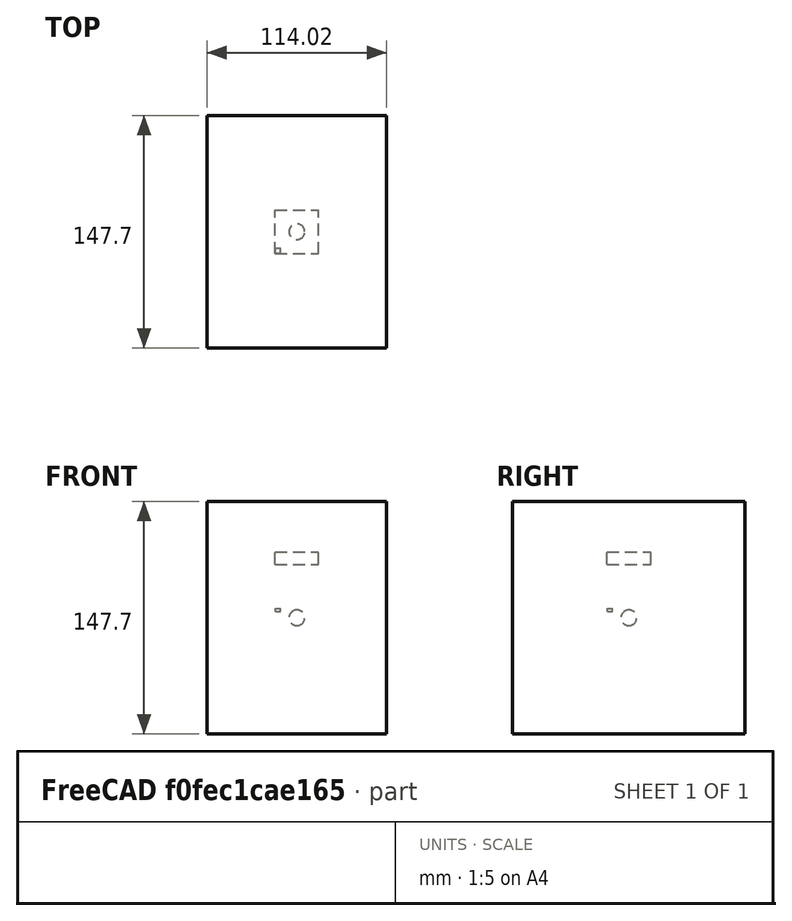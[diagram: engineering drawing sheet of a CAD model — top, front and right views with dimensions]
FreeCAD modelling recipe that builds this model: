
FCSTD DOCUMENT  (FreeCAD 0.20R29177 (Git))
Label: NoArray-borderTest-1
License: All rights reserved
objects: App::DocumentObjectGroupPython×1272, App::Link×77, App::Part×7, Part::FeaturePython×4, App::FeaturePython×1
note: 4 computed .brp shape members not serialized (recipe doc carries the construction recipe); baked Part::Feature solids carry a one-line shape summary decoded from their .brp

FEATURE [App::DocumentObjectGroupPython] HALFPI  # scripted group (container) (typed FeaturePython)
  name = HALFPI
  value = pi/2.
FEATURE [App::DocumentObjectGroupPython] PI  # scripted group (container) (typed FeaturePython)
  name = PI
  value = 1.*pi
FEATURE [App::DocumentObjectGroupPython] TWOPI  # scripted group (container) (typed FeaturePython)
  name = TWOPI
  value = 2.*pi
FEATURE [App::DocumentObjectGroupPython] Constants  # scripted group (container) (typed FeaturePython)
  Group = -> [HALFPI,PI,TWOPI]
FEATURE [App::DocumentObjectGroupPython] Variables  # scripted group (container) (typed FeaturePython)
FEATURE [App::DocumentObjectGroupPython] Quantities  # scripted group (container) (typed FeaturePython)
FEATURE [App::DocumentObjectGroupPython] Isotopes  # scripted group (container) (typed FeaturePython)
FEATURE [App::DocumentObjectGroupPython] Elements  # scripted group (container) (typed FeaturePython)
FEATURE [App::DocumentObjectGroupPython] G4_AIR  label="G4_AIR : 1.000"  # scripted group (container) (typed FeaturePython)
  n = 1
FEATURE [App::DocumentObjectGroupPython] Air  # scripted group (container) (typed FeaturePython)
  Dunit = mg/cm3
  Dvalue = 1.29
  Group = -> [G4_AIR]
  RINDEX = AirRINDEX
  conduct = 2
  density = 1
  expand = 3
  name = Air
  specific = 4
FEATURE [App::DocumentObjectGroupPython] SY  # scripted group (container) (typed FeaturePython)
  coldim = 1
  values = 100000/MeV
FEATURE [App::DocumentObjectGroupPython] RS  # scripted group (container) (typed FeaturePython)
  coldim = 1
  values = 1
FEATURE [App::DocumentObjectGroupPython] FTC  # scripted group (container) (typed FeaturePython)
  coldim = 1
  values = 21.5*ns
FEATURE [App::DocumentObjectGroupPython] STC  # scripted group (container) (typed FeaturePython)
  coldim = 1
  values = 43.8*ns
FEATURE [App::DocumentObjectGroupPython] RY1  # scripted group (container) (typed FeaturePython)
  coldim = 1
  values = 95
FEATURE [App::DocumentObjectGroupPython] RY2  # scripted group (container) (typed FeaturePython)
  coldim = 1
  values = 5
FEATURE [App::DocumentObjectGroupPython] YR  # scripted group (container) (typed FeaturePython)
  coldim = 1
  values = 0.8
FEATURE [App::DocumentObjectGroupPython] SCINTLAR  # scripted group (container) (typed FeaturePython)
  coldim = 2
  values = <blob: 2358 chars omitted>
FEATURE [App::DocumentObjectGroupPython] RINDEXLAR  # scripted group (container) (typed FeaturePython)
  coldim = 2
  values = <blob: 9384 chars omitted>
FEATURE [App::DocumentObjectGroupPython] ABSLENGTHLAR  # scripted group (container) (typed FeaturePython)
  coldim = 2
  values = 7.74901*eV 10.0*m 7.77525*eV 10.0*m 7.80167*eV 10.0*m 7.82827*eV 10.0*m 7.85506*eV 10.0*m 7.88202*eV 10.0*m 7.90917*eV 10.0*m 7.93651*eV 10.0*m 7.96404*eV 10.0*m 7.99176*eV 10.0*m 8.01968*eV 10.0*m 8.04779*eV 10.0*m 8.07609*eV 10.0*m 8.1046*eV 10.0*m 8.13331*eV 10.0*m 8.16222*eV 10.0*m 8.19134*eV 10.0*m 8.22067*eV 10.0*m 8.25021*eV 10.0*m 8.27996*eV 10.0*m 8.30993*eV 10.0*m 8.34012*eV 10.0*m 8.37052*eV 10.0*m 8.40115*eV 10.0*m 8.432*eV 10.0*m 8.46308*eV 10.0*m 8.4944*eV 10.0*m 8.52594*eV 10.0*m 8.55772*eV 10.0*m 8.58973*eV 10.0*m 8.62199*eV 10.0*m 8.65449*eV 10.0*m 8.68723*eV 10.0*m 8.72023*eV 10.0*m 8.75347*eV 10.0*m 8.78697*eV 10.0*m 8.82073*eV 10.0*m 8.85475*eV 10.0*m 8.88903*eV 10.0*m 8.92358*eV 10.0*m 8.9584*eV 10.0*m 8.99349*eV 10.0*m 9.02885*eV 10.0*m 9.0645*eV 10.0*m 9.10043*eV 10.0*m 9.13664*eV 10.0*m 9.17314*eV 10.0*m 9.20994*eV 10.0*m 9.24703*eV 10.0*m 9.28442*eV 10.0*m 9.32212*eV 10.0*m 9.36012*eV 10.0*m 9.39844*eV 10.0*m 9.43707*eV 10.0*m 9.47602*eV 10.0*m 9.51529*eV 10.0*m 9.55489*eV 10.0*m 9.59481*eV 10.0*m 9.63508*eV 10.0*m 9.67568*eV 10.0*m 9.71663*eV 10.0*m 9.75792*eV 10.0*m 9.79957*eV 10.0*m 9.84158*eV 10.0*m 9.88394*eV 10.0*m 9.92668*eV 10.0*m 9.96978*eV 10.0*m 10.0133*eV 10.0*m 10.0571*eV 10.0*m 10.1014*eV 10.0*m 10.146*eV 10.0*m 10.191*eV 10.0*m 10.2365*eV 10.0*m 10.2823*eV 10.0*m 10.3286*eV 10.0*m 10.3752*eV 10.0*m 10.4223*eV 10.0*m 10.4699*eV 10.0*m 10.5178*eV 10.0*m 10.5662*eV 10.0*m 10.6151*eV 10.0*m 10.6644*eV 10.0*m 10.7142*eV 10.0*m 10.7644*eV 10.0*m 10.8151*eV 10.0*m 10.8663*eV 10.0*m 10.9179*eV 10.0*m 10.9701*eV 10.0*m 11.0228*eV 10.0*m 11.076*eV 10.0*m 11.1296*eV 10.0*m 11.1839*eV 10.0*m 11.2386*eV 10.0*m 11.2939*eV 10.0*m 11.3497*eV 10.0*m 11.4061*eV 10.0*m 11.463*eV 10.0*m 11.5206*eV 10.0*m 11.5787*eV 10.0*m 11.6373*eV 10.0*m
FEATURE [App::DocumentObjectGroupPython] RAYLEIGHLAR  # scripted group (container) (typed FeaturePython)
  coldim = 2
  values = 7.74901*eV 90.0*cm 7.77525*eV 90.0*cm 7.80167*eV 90.0*cm 7.82827*eV 90.0*cm 7.85506*eV 90.0*cm 7.88202*eV 90.0*cm 7.90917*eV 90.0*cm 7.93651*eV 90.0*cm 7.96404*eV 90.0*cm 7.99176*eV 90.0*cm 8.01968*eV 90.0*cm 8.04779*eV 90.0*cm 8.07609*eV 90.0*cm 8.1046*eV 90.0*cm 8.13331*eV 90.0*cm 8.16222*eV 90.0*cm 8.19134*eV 90.0*cm 8.22067*eV 90.0*cm 8.25021*eV 90.0*cm 8.27996*eV 90.0*cm 8.30993*eV 90.0*cm 8.34012*eV 90.0*cm 8.37052*eV 90.0*cm 8.40115*eV 90.0*cm 8.432*eV 90.0*cm 8.46308*eV 90.0*cm 8.4944*eV 90.0*cm 8.52594*eV 90.0*cm 8.55772*eV 90.0*cm 8.58973*eV 90.0*cm 8.62199*eV 90.0*cm 8.65449*eV 90.0*cm 8.68723*eV 90.0*cm 8.72023*eV 90.0*cm 8.75347*eV 90.0*cm 8.78697*eV 90.0*cm 8.82073*eV 90.0*cm 8.85475*eV 90.0*cm 8.88903*eV 90.0*cm 8.92358*eV 90.0*cm 8.9584*eV 90.0*cm 8.99349*eV 90.0*cm 9.02885*eV 90.0*cm 9.0645*eV 90.0*cm 9.10043*eV 90.0*cm 9.13664*eV 90.0*cm 9.17314*eV 90.0*cm 9.20994*eV 90.0*cm 9.24703*eV 90.0*cm 9.28442*eV 90.0*cm 9.32212*eV 90.0*cm 9.36012*eV 90.0*cm 9.39844*eV 90.0*cm 9.43707*eV 90.0*cm 9.47602*eV 90.0*cm 9.51529*eV 90.0*cm 9.55489*eV 90.0*cm 9.59481*eV 90.0*cm 9.63508*eV 90.0*cm 9.67568*eV 90.0*cm 9.71663*eV 90.0*cm 9.75792*eV 90.0*cm 9.79957*eV 90.0*cm 9.84158*eV 90.0*cm 9.88394*eV 90.0*cm 9.92668*eV 90.0*cm 9.96978*eV 90.0*cm 10.0133*eV 90.0*cm 10.0571*eV 90.0*cm 10.1014*eV 90.0*cm 10.146*eV 90.0*cm 10.191*eV 90.0*cm 10.2365*eV 90.0*cm 10.2823*eV 90.0*cm 10.3286*eV 90.0*cm 10.3752*eV 90.0*cm 10.4223*eV 90.0*cm 10.4699*eV 90.0*cm 10.5178*eV 90.0*cm 10.5662*eV 90.0*cm 10.6151*eV 90.0*cm 10.6644*eV 90.0*cm 10.7142*eV 90.0*cm 10.7644*eV 90.0*cm 10.8151*eV 90.0*cm 10.8663*eV 90.0*cm 10.9179*eV 90.0*cm 10.9701*eV 90.0*cm 11.0228*eV 90.0*cm 11.076*eV 90.0*cm 11.1296*eV 90.0*cm 11.1839*eV 90.0*cm 11.2386*eV 90.0*cm 11.2939*eV 90.0*cm 11.3497*eV 90.0*cm 11.4061*eV 90.0*cm 11.463*eV 90.0*cm 11.5206*eV 90.0*cm 11.5787*eV 90.0*cm 11.6373*eV 90.0*cm
FEATURE [App::DocumentObjectGroupPython] REFLECTIVITY  # scripted group (container) (typed FeaturePython)
  coldim = 2
  values = 2.034*eV 0.98 2.068*eV 0.98 2.103*eV 0.98 2.139*eV 0.98 2.177*eV 0.98 2.216*eV 0.98 2.256*eV 0.98 2.298*eV 0.98 2.341*eV 0.98 2.386*eV 0.98 2.433*eV 0.98 2.481*eV 0.98 2.532*eV 0.98 2.585*eV 0.98 2.64*eV 0.98 2.697*eV 0.98 2.757*eV 0.98 2.82*eV 0.98 2.885*eV 0.98 2.954*eV 0.98 3.026*eV 0.98 3.102*eV 0.98 3.181*eV 0.98 3.265*eV 0.98 3.353*eV 0.98 3.446*eV 0.98 3.545*eV 0.98 3.649*eV 0.98 3.76*eV 0.98 3.877*eV 0.98 4.002*eV 0.98 4.136*eV 0.98 5.0*eV 0.98 6.0*eV 0.98 7.0*eV 0.98 8.0*eV 0.98 9.0*eV 0.98 9.0*eV 0.98 10.0*eV 0.98 11.0*eV 0.98 11.6*eV 0.98
FEATURE [App::DocumentObjectGroupPython] EFFICIENCY  # scripted group (container) (typed FeaturePython)
  coldim = 2
  values = 2.034*eV 1 2.068*eV 1 2.103*eV 1 2.139*eV 1 2.177*eV 1 2.216*eV 1 2.256*eV 1 2.298*eV 1 2.341*eV 1 2.386*eV 1 2.433*eV 1 2.481*eV 1 2.532*eV 1 2.585*eV 1 2.64*eV 1 2.697*eV 1 2.757*eV 1 2.82*eV 1 2.885*eV 1 2.954*eV 1 3.026*eV 1 3.102*eV 1 3.181*eV  1 3.265*eV 1 3.353*eV 1 3.446*eV 1 3.545*eV 1 3.649*eV 1 3.76*eV 1 3.877*eV 1 4.002*eV 1 4.136*eV 1 5.0*eV 1 6.0*eV 1 7.0*eV 1 8.0*eV 1 9.0*eV 1 9.0*eV 1 10.0*eV 1 11.0*eV 1 11.6*eV 1
FEATURE [App::DocumentObjectGroupPython] AirRINDEX  # scripted group (container) (typed FeaturePython)
  coldim = 2
  values = 2.034*eV 1 2.068*eV 1 2.103*eV 1 2.139*eV 1 2.177*eV 1 2.216*eV 1 2.256*eV 1 2.298*eV 1 2.341*eV 1 2.386*eV 1 2.433*eV 1 2.481*eV 1 2.532*eV 1 2.585*eV 1 2.64*eV 1 2.697*eV 1 2.757*eV 1 2.82*eV 1 2.885*eV 1 2.954*eV 1 3.026*eV 1 3.102*eV 1 3.181*eV 1 3.265*eV 1 3.353*eV 1 3.446*eV 1 3.545*eV 1 3.649*eV 1 3.76*eV 1 3.877*eV 1 4.002*eV 1 4.136*eV 1 5.0*eV 1 6.0*eV 1 7.0*eV 1 8.0*eV 1 9.0*eV 1 10.0*eV 1 11.0*eV 1 11.6*eV 1
FEATURE [App::DocumentObjectGroupPython] Matrix  # scripted group (container) (typed FeaturePython)
  Group = -> [SY,RS,FTC,STC,RY1,RY2,YR,SCINTLAR,RINDEXLAR,ABSLENGTHLAR,RAYLEIGHLAR,REFLECTIVITY,EFFICIENCY,AirRINDEX]
FEATURE [App::DocumentObjectGroupPython] ScintWrap  # scripted group (container) (typed FeaturePython)
  EFFICIENCY = EFFICIENCY
  REFLECTIVITY = REFLECTIVITY
  finish = 39
  model = 0
  type = 2
  value = 1
FEATURE [App::DocumentObjectGroupPython] Surfaces  # scripted group (container) (typed FeaturePython)
  Group = -> [ScintWrap]
FEATURE [App::DocumentObjectGroupPython] Opticals  # scripted group (container) (typed FeaturePython)
  Group = -> [Matrix,Surfaces]
FEATURE [App::DocumentObjectGroupPython] G4Isotopes  # scripted group (container) (typed FeaturePython)
FEATURE [App::DocumentObjectGroupPython] H_element  # scripted group (container) (typed FeaturePython)
  Z = 1
  atom_value = 1.008
  formula = H
  name = H_element
FEATURE [App::DocumentObjectGroupPython] He_element  # scripted group (container) (typed FeaturePython)
  Z = 2
  atom_value = 4.0026
  formula = He
  name = He_element
FEATURE [App::DocumentObjectGroupPython] Li_element  # scripted group (container) (typed FeaturePython)
  Z = 3
  atom_value = 6.94
  formula = Li
  name = Li_element
FEATURE [App::DocumentObjectGroupPython] Be_element  # scripted group (container) (typed FeaturePython)
  Z = 4
  atom_value = 9.01218
  formula = Be
  name = Be_element
FEATURE [App::DocumentObjectGroupPython] B_element  # scripted group (container) (typed FeaturePython)
  Z = 5
  atom_value = 10.81
  formula = B
  name = B_element
FEATURE [App::DocumentObjectGroupPython] C_element  # scripted group (container) (typed FeaturePython)
  Z = 6
  atom_value = 12.011
  formula = C
  name = C_element
FEATURE [App::DocumentObjectGroupPython] N_element  # scripted group (container) (typed FeaturePython)
  Z = 7
  atom_value = 14.007
  formula = N
  name = N_element
FEATURE [App::DocumentObjectGroupPython] O_element  # scripted group (container) (typed FeaturePython)
  Z = 8
  atom_value = 15.999
  formula = O
  name = O_element
FEATURE [App::DocumentObjectGroupPython] F_element  # scripted group (container) (typed FeaturePython)
  Z = 9
  atom_value = 18.9984
  formula = F
  name = F_element
FEATURE [App::DocumentObjectGroupPython] Ne_element  # scripted group (container) (typed FeaturePython)
  Z = 10
  atom_value = 20.1797
  formula = Ne
  name = Ne_element
FEATURE [App::DocumentObjectGroupPython] Na_element  # scripted group (container) (typed FeaturePython)
  Z = 11
  atom_value = 22.9898
  formula = Na
  name = Na_element
FEATURE [App::DocumentObjectGroupPython] Mg_element  # scripted group (container) (typed FeaturePython)
  Z = 12
  atom_value = 24.305
  formula = Mg
  name = Mg_element
FEATURE [App::DocumentObjectGroupPython] Al_element  # scripted group (container) (typed FeaturePython)
  Z = 13
  atom_value = 26.9815
  formula = Al
  name = Al_element
FEATURE [App::DocumentObjectGroupPython] Si_element  # scripted group (container) (typed FeaturePython)
  Z = 14
  atom_value = 28.085
  formula = Si
  name = Si_element
FEATURE [App::DocumentObjectGroupPython] P_element  # scripted group (container) (typed FeaturePython)
  Z = 15
  atom_value = 30.9738
  formula = P
  name = P_element
FEATURE [App::DocumentObjectGroupPython] S_element  # scripted group (container) (typed FeaturePython)
  Z = 16
  atom_value = 32.06
  formula = S
  name = S_element
FEATURE [App::DocumentObjectGroupPython] Cl_element  # scripted group (container) (typed FeaturePython)
  Z = 17
  atom_value = 35.45
  formula = Cl
  name = Cl_element
FEATURE [App::DocumentObjectGroupPython] Ar_element  # scripted group (container) (typed FeaturePython)
  Z = 18
  atom_value = 39.95
  formula = Ar
  name = Ar_element
FEATURE [App::DocumentObjectGroupPython] K_element  # scripted group (container) (typed FeaturePython)
  Z = 19
  atom_value = 39.0983
  formula = K
  name = K_element
FEATURE [App::DocumentObjectGroupPython] Ca_element  # scripted group (container) (typed FeaturePython)
  Z = 20
  atom_value = 40.078
  formula = Ca
  name = Ca_element
FEATURE [App::DocumentObjectGroupPython] Sc_element  # scripted group (container) (typed FeaturePython)
  Z = 21
  atom_value = 44.9559
  formula = Sc
  name = Sc_element
FEATURE [App::DocumentObjectGroupPython] Ti_element  # scripted group (container) (typed FeaturePython)
  Z = 22
  atom_value = 47.867
  formula = Ti
  name = Ti_element
FEATURE [App::DocumentObjectGroupPython] V_element  # scripted group (container) (typed FeaturePython)
  Z = 23
  atom_value = 50.9415
  formula = V
  name = V_element
FEATURE [App::DocumentObjectGroupPython] Cr_element  # scripted group (container) (typed FeaturePython)
  Z = 24
  atom_value = 51.9961
  formula = Cr
  name = Cr_element
FEATURE [App::DocumentObjectGroupPython] Mn_element  # scripted group (container) (typed FeaturePython)
  Z = 25
  atom_value = 54.938
  formula = Mn
  name = Mn_element
FEATURE [App::DocumentObjectGroupPython] Fe_element  # scripted group (container) (typed FeaturePython)
  Z = 26
  atom_value = 55.845
  formula = Fe
  name = Fe_element
FEATURE [App::DocumentObjectGroupPython] Co_element  # scripted group (container) (typed FeaturePython)
  Z = 27
  atom_value = 58.9332
  formula = Co
  name = Co_element
FEATURE [App::DocumentObjectGroupPython] Ni_element  # scripted group (container) (typed FeaturePython)
  Z = 28
  atom_value = 58.6934
  formula = Ni
  name = Ni_element
FEATURE [App::DocumentObjectGroupPython] Cu_element  # scripted group (container) (typed FeaturePython)
  Z = 29
  atom_value = 63.546
  formula = Cu
  name = Cu_element
FEATURE [App::DocumentObjectGroupPython] Zn_element  # scripted group (container) (typed FeaturePython)
  Z = 30
  atom_value = 65.38
  formula = Zn
  name = Zn_element
FEATURE [App::DocumentObjectGroupPython] Ga_element  # scripted group (container) (typed FeaturePython)
  Z = 31
  atom_value = 69.723
  formula = Ga
  name = Ga_element
FEATURE [App::DocumentObjectGroupPython] Ge_element  # scripted group (container) (typed FeaturePython)
  Z = 32
  atom_value = 72.63
  formula = Ge
  name = Ge_element
FEATURE [App::DocumentObjectGroupPython] As_element  # scripted group (container) (typed FeaturePython)
  Z = 33
  atom_value = 74.9216
  formula = As
  name = As_element
FEATURE [App::DocumentObjectGroupPython] Se_element  # scripted group (container) (typed FeaturePython)
  Z = 34
  atom_value = 78.971
  formula = Se
  name = Se_element
FEATURE [App::DocumentObjectGroupPython] Br_element  # scripted group (container) (typed FeaturePython)
  Z = 35
  atom_value = 79.904
  formula = Br
  name = Br_element
FEATURE [App::DocumentObjectGroupPython] Kr_element  # scripted group (container) (typed FeaturePython)
  Z = 36
  atom_value = 83.798
  formula = Kr
  name = Kr_element
FEATURE [App::DocumentObjectGroupPython] Rb_element  # scripted group (container) (typed FeaturePython)
  Z = 37
  atom_value = 85.4678
  formula = Rb
  name = Rb_element
FEATURE [App::DocumentObjectGroupPython] Sr_element  # scripted group (container) (typed FeaturePython)
  Z = 38
  atom_value = 87.62
  formula = Sr
  name = Sr_element
FEATURE [App::DocumentObjectGroupPython] Y_element  # scripted group (container) (typed FeaturePython)
  Z = 39
  atom_value = 88.9058
  formula = Y
  name = Y_element
FEATURE [App::DocumentObjectGroupPython] Zr_element  # scripted group (container) (typed FeaturePython)
  Z = 40
  atom_value = 91.224
  formula = Zr
  name = Zr_element
FEATURE [App::DocumentObjectGroupPython] Nb_element  # scripted group (container) (typed FeaturePython)
  Z = 41
  atom_value = 92.9064
  formula = Nb
  name = Nb_element
FEATURE [App::DocumentObjectGroupPython] Mo_element  # scripted group (container) (typed FeaturePython)
  Z = 42
  atom_value = 95.95
  formula = Mo
  name = Mo_element
FEATURE [App::DocumentObjectGroupPython] Tc_element  # scripted group (container) (typed FeaturePython)
  Z = 43
  atom_value = 97
  formula = Tc
  name = Tc_element
FEATURE [App::DocumentObjectGroupPython] Ru_element  # scripted group (container) (typed FeaturePython)
  Z = 44
  atom_value = 101.07
  formula = Ru
  name = Ru_element
FEATURE [App::DocumentObjectGroupPython] Rh_element  # scripted group (container) (typed FeaturePython)
  Z = 45
  atom_value = 102.905
  formula = Rh
  name = Rh_element
FEATURE [App::DocumentObjectGroupPython] Pd_element  # scripted group (container) (typed FeaturePython)
  Z = 46
  atom_value = 106.42
  formula = Pd
  name = Pd_element
FEATURE [App::DocumentObjectGroupPython] Ag_element  # scripted group (container) (typed FeaturePython)
  Z = 47
  atom_value = 107.868
  formula = Ag
  name = Ag_element
FEATURE [App::DocumentObjectGroupPython] Cd_element  # scripted group (container) (typed FeaturePython)
  Z = 48
  atom_value = 112.414
  formula = Cd
  name = Cd_element
FEATURE [App::DocumentObjectGroupPython] In_element  # scripted group (container) (typed FeaturePython)
  Z = 49
  atom_value = 114.818
  formula = In
  name = In_element
FEATURE [App::DocumentObjectGroupPython] Sn_element  # scripted group (container) (typed FeaturePython)
  Z = 50
  atom_value = 118.71
  formula = Sn
  name = Sn_element
FEATURE [App::DocumentObjectGroupPython] Sb_element  # scripted group (container) (typed FeaturePython)
  Z = 51
  atom_value = 121.76
  formula = Sb
  name = Sb_element
FEATURE [App::DocumentObjectGroupPython] Te_element  # scripted group (container) (typed FeaturePython)
  Z = 52
  atom_value = 127.6
  formula = Te
  name = Te_element
FEATURE [App::DocumentObjectGroupPython] I_element  # scripted group (container) (typed FeaturePython)
  Z = 53
  atom_value = 126.904
  formula = I
  name = I_element
FEATURE [App::DocumentObjectGroupPython] Xe_element  # scripted group (container) (typed FeaturePython)
  Z = 54
  atom_value = 131.293
  formula = Xe
  name = Xe_element
FEATURE [App::DocumentObjectGroupPython] Cs_element  # scripted group (container) (typed FeaturePython)
  Z = 55
  atom_value = 132.905
  formula = Cs
  name = Cs_element
FEATURE [App::DocumentObjectGroupPython] Ba_element  # scripted group (container) (typed FeaturePython)
  Z = 56
  atom_value = 137.327
  formula = Ba
  name = Ba_element
FEATURE [App::DocumentObjectGroupPython] La_element  # scripted group (container) (typed FeaturePython)
  Z = 57
  atom_value = 138.905
  formula = La
  name = La_element
FEATURE [App::DocumentObjectGroupPython] Ce_element  # scripted group (container) (typed FeaturePython)
  Z = 58
  atom_value = 140.116
  formula = Ce
  name = Ce_element
FEATURE [App::DocumentObjectGroupPython] Pr_element  # scripted group (container) (typed FeaturePython)
  Z = 59
  atom_value = 140.908
  formula = Pr
  name = Pr_element
FEATURE [App::DocumentObjectGroupPython] Nd_element  # scripted group (container) (typed FeaturePython)
  Z = 60
  atom_value = 144.242
  formula = Nd
  name = Nd_element
FEATURE [App::DocumentObjectGroupPython] Pm_element  # scripted group (container) (typed FeaturePython)
  Z = 61
  atom_value = 145
  formula = Pm
  name = Pm_element
FEATURE [App::DocumentObjectGroupPython] Sm_element  # scripted group (container) (typed FeaturePython)
  Z = 62
  atom_value = 150.36
  formula = Sm
  name = Sm_element
FEATURE [App::DocumentObjectGroupPython] Eu_element  # scripted group (container) (typed FeaturePython)
  Z = 63
  atom_value = 151.964
  formula = Eu
  name = Eu_element
FEATURE [App::DocumentObjectGroupPython] Gd_element  # scripted group (container) (typed FeaturePython)
  Z = 64
  atom_value = 157.25
  formula = Gd
  name = Gd_element
FEATURE [App::DocumentObjectGroupPython] Tb_element  # scripted group (container) (typed FeaturePython)
  Z = 65
  atom_value = 158.925
  formula = Tb
  name = Tb_element
FEATURE [App::DocumentObjectGroupPython] Dy_element  # scripted group (container) (typed FeaturePython)
  Z = 66
  atom_value = 162.5
  formula = Dy
  name = Dy_element
FEATURE [App::DocumentObjectGroupPython] Ho_element  # scripted group (container) (typed FeaturePython)
  Z = 67
  atom_value = 164.93
  formula = Ho
  name = Ho_element
FEATURE [App::DocumentObjectGroupPython] Er_element  # scripted group (container) (typed FeaturePython)
  Z = 68
  atom_value = 167.259
  formula = Er
  name = Er_element
FEATURE [App::DocumentObjectGroupPython] Tm_element  # scripted group (container) (typed FeaturePython)
  Z = 69
  atom_value = 168.934
  formula = Tm
  name = Tm_element
FEATURE [App::DocumentObjectGroupPython] Yb_element  # scripted group (container) (typed FeaturePython)
  Z = 70
  atom_value = 173.045
  formula = Yb
  name = Yb_element
FEATURE [App::DocumentObjectGroupPython] Lu_element  # scripted group (container) (typed FeaturePython)
  Z = 71
  atom_value = 174.967
  formula = Lu
  name = Lu_element
FEATURE [App::DocumentObjectGroupPython] Hf_element  # scripted group (container) (typed FeaturePython)
  Z = 72
  atom_value = 178.49
  formula = Hf
  name = Hf_element
FEATURE [App::DocumentObjectGroupPython] Ta_element  # scripted group (container) (typed FeaturePython)
  Z = 73
  atom_value = 180.948
  formula = Ta
  name = Ta_element
FEATURE [App::DocumentObjectGroupPython] W_element  # scripted group (container) (typed FeaturePython)
  Z = 74
  atom_value = 183.84
  formula = W
  name = W_element
FEATURE [App::DocumentObjectGroupPython] Re_element  # scripted group (container) (typed FeaturePython)
  Z = 75
  atom_value = 186.207
  formula = Re
  name = Re_element
FEATURE [App::DocumentObjectGroupPython] Os_element  # scripted group (container) (typed FeaturePython)
  Z = 76
  atom_value = 190.23
  formula = Os
  name = Os_element
FEATURE [App::DocumentObjectGroupPython] Ir_element  # scripted group (container) (typed FeaturePython)
  Z = 77
  atom_value = 192.217
  formula = Ir
  name = Ir_element
FEATURE [App::DocumentObjectGroupPython] Pt_element  # scripted group (container) (typed FeaturePython)
  Z = 78
  atom_value = 195.084
  formula = Pt
  name = Pt_element
FEATURE [App::DocumentObjectGroupPython] Au_element  # scripted group (container) (typed FeaturePython)
  Z = 79
  atom_value = 196.967
  formula = Au
  name = Au_element
FEATURE [App::DocumentObjectGroupPython] Hg_element  # scripted group (container) (typed FeaturePython)
  Z = 80
  atom_value = 200.592
  formula = Hg
  name = Hg_element
FEATURE [App::DocumentObjectGroupPython] Tl_element  # scripted group (container) (typed FeaturePython)
  Z = 81
  atom_value = 204.38
  formula = Tl
  name = Tl_element
FEATURE [App::DocumentObjectGroupPython] Pb_element  # scripted group (container) (typed FeaturePython)
  Z = 82
  atom_value = 207.2
  formula = Pb
  name = Pb_element
FEATURE [App::DocumentObjectGroupPython] Bi_element  # scripted group (container) (typed FeaturePython)
  Z = 83
  atom_value = 208.98
  formula = Bi
  name = Bi_element
FEATURE [App::DocumentObjectGroupPython] Po_element  # scripted group (container) (typed FeaturePython)
  Z = 84
  atom_value = 209
  formula = Po
  name = Po_element
FEATURE [App::DocumentObjectGroupPython] At_element  # scripted group (container) (typed FeaturePython)
  Z = 85
  atom_value = 210
  formula = At
  name = At_element
FEATURE [App::DocumentObjectGroupPython] Rn_element  # scripted group (container) (typed FeaturePython)
  Z = 86
  atom_value = 222
  formula = Rn
  name = Rn_element
FEATURE [App::DocumentObjectGroupPython] Fr_element  # scripted group (container) (typed FeaturePython)
  Z = 87
  atom_value = 223
  formula = Fr
  name = Fr_element
FEATURE [App::DocumentObjectGroupPython] Ra_element  # scripted group (container) (typed FeaturePython)
  Z = 88
  atom_value = 226
  formula = Ra
  name = Ra_element
FEATURE [App::DocumentObjectGroupPython] Ac_element  # scripted group (container) (typed FeaturePython)
  Z = 89
  atom_value = 227
  formula = Ac
  name = Ac_element
FEATURE [App::DocumentObjectGroupPython] Th_element  # scripted group (container) (typed FeaturePython)
  Z = 90
  atom_value = 232.038
  formula = Th
  name = Th_element
FEATURE [App::DocumentObjectGroupPython] Pa_element  # scripted group (container) (typed FeaturePython)
  Z = 91
  atom_value = 231.036
  formula = Pa
  name = Pa_element
FEATURE [App::DocumentObjectGroupPython] U_element  # scripted group (container) (typed FeaturePython)
  Z = 92
  atom_value = 238.029
  formula = U
  name = U_element
FEATURE [App::DocumentObjectGroupPython] Np_element  # scripted group (container) (typed FeaturePython)
  Z = 93
  atom_value = 237
  formula = Np
  name = Np_element
FEATURE [App::DocumentObjectGroupPython] Pu_element  # scripted group (container) (typed FeaturePython)
  Z = 94
  atom_value = 244
  formula = Pu
  name = Pu_element
FEATURE [App::DocumentObjectGroupPython] Am_element  # scripted group (container) (typed FeaturePython)
  Z = 95
  atom_value = 243
  formula = Am
  name = Am_element
FEATURE [App::DocumentObjectGroupPython] Cm_element  # scripted group (container) (typed FeaturePython)
  Z = 96
  atom_value = 247
  formula = Cm
  name = Cm_element
FEATURE [App::DocumentObjectGroupPython] Bk_element  # scripted group (container) (typed FeaturePython)
  Z = 97
  atom_value = 247
  formula = Bk
  name = Bk_element
FEATURE [App::DocumentObjectGroupPython] Cf_element  # scripted group (container) (typed FeaturePython)
  Z = 98
  atom_value = 251
  formula = Cf
  name = Cf_element
FEATURE [App::DocumentObjectGroupPython] G4Elements  # scripted group (container) (typed FeaturePython)
  Group = -> [H_element,He_element,Li_element,Be_element,B_element,C_element,N_element,O_element,F_element,Ne_element,Na_element,Mg_element,Al_element,Si_element,P_element,S_element,Cl_element,Ar_element,K_element,Ca_element,Sc_element,Ti_element,V_element,Cr_element,Mn_element,Fe_element,Co_element,Ni_element,Cu_element,Zn_element,Ga_element,Ge_element,As_element,Se_element,Br_element,Kr_element,Rb_element,+61 more]
FEATURE [App::DocumentObjectGroupPython] H_element001  label="H_element : 0.101"  # scripted group (container) (typed FeaturePython)
  n = 0.101327
FEATURE [App::DocumentObjectGroupPython] C_element001  label="C_element : 0.775"  # scripted group (container) (typed FeaturePython)
  n = 0.7755
FEATURE [App::DocumentObjectGroupPython] N_element001  label="N_element : 0.035"  # scripted group (container) (typed FeaturePython)
  n = 0.035057
FEATURE [App::DocumentObjectGroupPython] O_element001  label="O_element : 0.052"  # scripted group (container) (typed FeaturePython)
  n = 0.0523159
FEATURE [App::DocumentObjectGroupPython] F_element001  label="F_element : 0.017"  # scripted group (container) (typed FeaturePython)
  n = 0.017422
FEATURE [App::DocumentObjectGroupPython] Ca_element001  label="Ca_element : 0.018"  # scripted group (container) (typed FeaturePython)
  n = 0.018378
FEATURE [App::DocumentObjectGroupPython] G4_A_150_TISSUE  label="G4_A-150_TISSUE"  # scripted group (container) (typed FeaturePython)
  Dunit = g/cm3
  Dvalue = 1.127
  Group = -> [H_element001,C_element001,N_element001,O_element001,F_element001,Ca_element001]
  conduct = 2
  density = 1
  expand = 3
  formula = G4_A-150_TISSUE
  name = G4_A-150_TISSUE
  specific = 4
FEATURE [App::DocumentObjectGroupPython] C_element002  label="C_element : 3"  # scripted group (container) (typed FeaturePython)
  n = 3
  ref = C_element
FEATURE [App::DocumentObjectGroupPython] H_element002  label="H_element : 6"  # scripted group (container) (typed FeaturePython)
  n = 6
  ref = H_element
FEATURE [App::DocumentObjectGroupPython] O_element002  label="O_element : 1"  # scripted group (container) (typed FeaturePython)
  n = 1
  ref = O_element
FEATURE [App::DocumentObjectGroupPython] G4_ACETONE  # scripted group (container) (typed FeaturePython)
  Dunit = g/cm3
  Dvalue = 0.7899
  Group = -> [C_element002,H_element002,O_element002]
  conduct = 2
  density = 1
  expand = 3
  formula = G4_ACETONE
  name = G4_ACETONE
  specific = 4
FEATURE [App::DocumentObjectGroupPython] C_element003  label="C_element : 2"  # scripted group (container) (typed FeaturePython)
  n = 2
  ref = C_element
FEATURE [App::DocumentObjectGroupPython] H_element003  label="H_element : 2"  # scripted group (container) (typed FeaturePython)
  n = 2
  ref = H_element
FEATURE [App::DocumentObjectGroupPython] G4_ACETYLENE  # scripted group (container) (typed FeaturePython)
  Dunit = g/cm3
  Dvalue = 0.0010967
  Group = -> [C_element003,H_element003]
  conduct = 2
  density = 1
  expand = 3
  formula = G4_ACETYLENE
  name = G4_ACETYLENE
  specific = 4
FEATURE [App::DocumentObjectGroupPython] C_element004  label="C_element : 5"  # scripted group (container) (typed FeaturePython)
  n = 5
  ref = C_element
FEATURE [App::DocumentObjectGroupPython] H_element004  label="H_element : 5"  # scripted group (container) (typed FeaturePython)
  n = 5
  ref = H_element
FEATURE [App::DocumentObjectGroupPython] N_element002  label="N_element : 5"  # scripted group (container) (typed FeaturePython)
  n = 5
  ref = N_element
FEATURE [App::DocumentObjectGroupPython] G4_ADENINE  # scripted group (container) (typed FeaturePython)
  Dunit = g/cm3
  Dvalue = 1.6
  Group = -> [C_element004,H_element004,N_element002]
  conduct = 2
  density = 1
  expand = 3
  formula = G4_ADENINE
  name = G4_ADENINE
  specific = 4
FEATURE [App::DocumentObjectGroupPython] H_element005  label="H_element : 0.114"  # scripted group (container) (typed FeaturePython)
  n = 0.114
FEATURE [App::DocumentObjectGroupPython] C_element005  label="C_element : 0.598"  # scripted group (container) (typed FeaturePython)
  n = 0.598
FEATURE [App::DocumentObjectGroupPython] N_element003  label="N_element : 0.007"  # scripted group (container) (typed FeaturePython)
  n = 0.007
FEATURE [App::DocumentObjectGroupPython] O_element003  label="O_element : 0.278"  # scripted group (container) (typed FeaturePython)
  n = 0.278
FEATURE [App::DocumentObjectGroupPython] Na_element001  label="Na_element : 0.001"  # scripted group (container) (typed FeaturePython)
  n = 0.001
FEATURE [App::DocumentObjectGroupPython] S_element001  label="S_element : 0.001"  # scripted group (container) (typed FeaturePython)
  n = 0.001
FEATURE [App::DocumentObjectGroupPython] Cl_element001  label="Cl_element : 0.001"  # scripted group (container) (typed FeaturePython)
  n = 0.001
FEATURE [App::DocumentObjectGroupPython] G4_ADIPOSE_TISSUE_ICRP  # scripted group (container) (typed FeaturePython)
  Dunit = g/cm3
  Dvalue = 0.95
  Group = -> [H_element005,C_element005,N_element003,O_element003,Na_element001,S_element001,Cl_element001]
  conduct = 2
  density = 1
  expand = 3
  formula = G4_ADIPOSE_TISSUE_ICRP
  name = G4_ADIPOSE_TISSUE_ICRP
  specific = 4
FEATURE [App::DocumentObjectGroupPython] C_element006  label="C_element : 0.000"  # scripted group (container) (typed FeaturePython)
  n = 0.000124
FEATURE [App::DocumentObjectGroupPython] N_element004  label="N_element : 0.755"  # scripted group (container) (typed FeaturePython)
  n = 0.755268
FEATURE [App::DocumentObjectGroupPython] O_element004  label="O_element : 0.232"  # scripted group (container) (typed FeaturePython)
  n = 0.231781
FEATURE [App::DocumentObjectGroupPython] Ar_element001  label="Ar_element : 0.013"  # scripted group (container) (typed FeaturePython)
  n = 0.012827
FEATURE [App::DocumentObjectGroupPython] G4_AIR001  label="G4_AIR"  # scripted group (container) (typed FeaturePython)
  Dunit = g/cm3
  Dvalue = 0.00120479
  Group = -> [C_element006,N_element004,O_element004,Ar_element001]
  conduct = 2
  density = 1
  expand = 3
  formula = G4_AIR
  name = G4_AIR
  specific = 4
FEATURE [App::DocumentObjectGroupPython] C_element007  label="C_element : 006"  # scripted group (container) (typed FeaturePython)
  n = 3
  ref = C_element
FEATURE [App::DocumentObjectGroupPython] H_element006  label="H_element : 7"  # scripted group (container) (typed FeaturePython)
  n = 7
  ref = H_element
FEATURE [App::DocumentObjectGroupPython] N_element005  label="N_element : 1"  # scripted group (container) (typed FeaturePython)
  n = 1
  ref = N_element
FEATURE [App::DocumentObjectGroupPython] O_element005  label="O_element : 2"  # scripted group (container) (typed FeaturePython)
  n = 2
  ref = O_element
FEATURE [App::DocumentObjectGroupPython] G4_ALANINE  # scripted group (container) (typed FeaturePython)
  Dunit = g/cm3
  Dvalue = 1.42
  Group = -> [C_element007,H_element006,N_element005,O_element005]
  conduct = 2
  density = 1
  expand = 3
  formula = G4_ALANINE
  name = G4_ALANINE
  specific = 4
FEATURE [App::DocumentObjectGroupPython] Al_element001  label="Al_element : 2"  # scripted group (container) (typed FeaturePython)
  n = 2
  ref = Al_element
FEATURE [App::DocumentObjectGroupPython] O_element006  label="O_element : 3"  # scripted group (container) (typed FeaturePython)
  n = 3
  ref = O_element
FEATURE [App::DocumentObjectGroupPython] G4_ALUMINUM_OXIDE  # scripted group (container) (typed FeaturePython)
  Dunit = g/cm3
  Dvalue = 3.97
  Group = -> [Al_element001,O_element006]
  conduct = 2
  density = 1
  expand = 3
  formula = G4_ALUMINUM_OXIDE
  name = G4_ALUMINUM_OXIDE
  specific = 4
FEATURE [App::DocumentObjectGroupPython] H_element007  label="H_element : 0.106"  # scripted group (container) (typed FeaturePython)
  n = 0.10593
FEATURE [App::DocumentObjectGroupPython] C_element008  label="C_element : 0.789"  # scripted group (container) (typed FeaturePython)
  n = 0.788974
FEATURE [App::DocumentObjectGroupPython] O_element007  label="O_element : 0.105"  # scripted group (container) (typed FeaturePython)
  n = 0.105096
FEATURE [App::DocumentObjectGroupPython] G4_AMBER  # scripted group (container) (typed FeaturePython)
  Dunit = g/cm3
  Dvalue = 1.1
  Group = -> [H_element007,C_element008,O_element007]
  conduct = 2
  density = 1
  expand = 3
  formula = G4_AMBER
  name = G4_AMBER
  specific = 4
FEATURE [App::DocumentObjectGroupPython] N_element006  label="N_element : 006"  # scripted group (container) (typed FeaturePython)
  n = 1
  ref = N_element
FEATURE [App::DocumentObjectGroupPython] H_element008  label="H_element : 3"  # scripted group (container) (typed FeaturePython)
  n = 3
  ref = H_element
FEATURE [App::DocumentObjectGroupPython] G4_AMMONIA  # scripted group (container) (typed FeaturePython)
  Dunit = g/cm3
  Dvalue = 0.000826019
  Group = -> [N_element006,H_element008]
  conduct = 2
  density = 1
  expand = 3
  formula = G4_AMMONIA
  name = G4_AMMONIA
  specific = 4
FEATURE [App::DocumentObjectGroupPython] C_element009  label="C_element : 6"  # scripted group (container) (typed FeaturePython)
  n = 6
  ref = C_element
FEATURE [App::DocumentObjectGroupPython] H_element009  label="H_element : 008"  # scripted group (container) (typed FeaturePython)
  n = 7
  ref = H_element
FEATURE [App::DocumentObjectGroupPython] N_element007  label="N_element : 007"  # scripted group (container) (typed FeaturePython)
  n = 1
  ref = N_element
FEATURE [App::DocumentObjectGroupPython] G4_ANILINE  # scripted group (container) (typed FeaturePython)
  Dunit = g/cm3
  Dvalue = 1.0235
  Group = -> [C_element009,H_element009,N_element007]
  conduct = 2
  density = 1
  expand = 3
  formula = G4_ANILINE
  name = G4_ANILINE
  specific = 4
FEATURE [App::DocumentObjectGroupPython] C_element010  label="C_element : 14"  # scripted group (container) (typed FeaturePython)
  n = 14
  ref = C_element
FEATURE [App::DocumentObjectGroupPython] H_element010  label="H_element : 10"  # scripted group (container) (typed FeaturePython)
  n = 10
  ref = H_element
FEATURE [App::DocumentObjectGroupPython] G4_ANTHRACENE  # scripted group (container) (typed FeaturePython)
  Dunit = g/cm3
  Dvalue = 1.283
  Group = -> [C_element010,H_element010]
  conduct = 2
  density = 1
  expand = 3
  formula = G4_ANTHRACENE
  name = G4_ANTHRACENE
  specific = 4
FEATURE [App::DocumentObjectGroupPython] H_element011  label="H_element : 0.065"  # scripted group (container) (typed FeaturePython)
  n = 0.0654709
FEATURE [App::DocumentObjectGroupPython] C_element011  label="C_element : 0.537"  # scripted group (container) (typed FeaturePython)
  n = 0.536944
FEATURE [App::DocumentObjectGroupPython] N_element008  label="N_element : 0.021"  # scripted group (container) (typed FeaturePython)
  n = 0.0215
FEATURE [App::DocumentObjectGroupPython] O_element008  label="O_element : 0.032"  # scripted group (container) (typed FeaturePython)
  n = 0.032085
FEATURE [App::DocumentObjectGroupPython] F_element002  label="F_element : 0.167"  # scripted group (container) (typed FeaturePython)
  n = 0.167411
FEATURE [App::DocumentObjectGroupPython] Ca_element002  label="Ca_element : 0.177"  # scripted group (container) (typed FeaturePython)
  n = 0.176589
FEATURE [App::DocumentObjectGroupPython] G4_B_100_BONE  label="G4_B-100_BONE"  # scripted group (container) (typed FeaturePython)
  Dunit = g/cm3
  Dvalue = 1.45
  Group = -> [H_element011,C_element011,N_element008,O_element008,F_element002,Ca_element002]
  conduct = 2
  density = 1
  expand = 3
  formula = G4_B-100_BONE
  name = G4_B-100_BONE
  specific = 4
FEATURE [App::DocumentObjectGroupPython] H_element012  label="H_element : 0.057"  # scripted group (container) (typed FeaturePython)
  n = 0.057441
FEATURE [App::DocumentObjectGroupPython] C_element012  label="C_element : 0.790"  # scripted group (container) (typed FeaturePython)
  n = 0.774591
FEATURE [App::DocumentObjectGroupPython] O_element009  label="O_element : 0.168"  # scripted group (container) (typed FeaturePython)
  n = 0.167968
FEATURE [App::DocumentObjectGroupPython] G4_BAKELITE  # scripted group (container) (typed FeaturePython)
  Dunit = g/cm3
  Dvalue = 1.25
  Group = -> [H_element012,C_element012,O_element009]
  conduct = 2
  density = 1
  expand = 3
  formula = G4_BAKELITE
  name = G4_BAKELITE
  specific = 4
FEATURE [App::DocumentObjectGroupPython] Ba_element001  label="Ba_element : 1"  # scripted group (container) (typed FeaturePython)
  n = 1
  ref = Ba_element
FEATURE [App::DocumentObjectGroupPython] F_element003  label="F_element : 2"  # scripted group (container) (typed FeaturePython)
  n = 2
  ref = F_element
FEATURE [App::DocumentObjectGroupPython] G4_BARIUM_FLUORIDE  # scripted group (container) (typed FeaturePython)
  Dunit = g/cm3
  Dvalue = 4.89
  Group = -> [Ba_element001,F_element003]
  conduct = 2
  density = 1
  expand = 3
  formula = G4_BARIUM_FLUORIDE
  name = G4_BARIUM_FLUORIDE
  specific = 4
FEATURE [App::DocumentObjectGroupPython] Ba_element002  label="Ba_element : 002"  # scripted group (container) (typed FeaturePython)
  n = 1
  ref = Ba_element
FEATURE [App::DocumentObjectGroupPython] S_element002  label="S_element : 1"  # scripted group (container) (typed FeaturePython)
  n = 1
  ref = S_element
FEATURE [App::DocumentObjectGroupPython] O_element010  label="O_element : 4"  # scripted group (container) (typed FeaturePython)
  n = 4
  ref = O_element
FEATURE [App::DocumentObjectGroupPython] G4_BARIUM_SULFATE  # scripted group (container) (typed FeaturePython)
  Dunit = g/cm3
  Dvalue = 4.5
  Group = -> [Ba_element002,S_element002,O_element010]
  conduct = 2
  density = 1
  expand = 3
  formula = G4_BARIUM_SULFATE
  name = G4_BARIUM_SULFATE
  specific = 4
FEATURE [App::DocumentObjectGroupPython] C_element013  label="C_element : 007"  # scripted group (container) (typed FeaturePython)
  n = 6
  ref = C_element
FEATURE [App::DocumentObjectGroupPython] H_element013  label="H_element : 009"  # scripted group (container) (typed FeaturePython)
  n = 6
  ref = H_element
FEATURE [App::DocumentObjectGroupPython] G4_BENZENE  # scripted group (container) (typed FeaturePython)
  Dunit = g/cm3
  Dvalue = 0.87865
  Group = -> [C_element013,H_element013]
  conduct = 2
  density = 1
  expand = 3
  formula = G4_BENZENE
  name = G4_BENZENE
  specific = 4
FEATURE [App::DocumentObjectGroupPython] Be_element001  label="Be_element : 1"  # scripted group (container) (typed FeaturePython)
  n = 1
  ref = Be_element
FEATURE [App::DocumentObjectGroupPython] O_element011  label="O_element : 005"  # scripted group (container) (typed FeaturePython)
  n = 1
  ref = O_element
FEATURE [App::DocumentObjectGroupPython] G4_BERYLLIUM_OXIDE  # scripted group (container) (typed FeaturePython)
  Dunit = g/cm3
  Dvalue = 3.01
  Group = -> [Be_element001,O_element011]
  conduct = 2
  density = 1
  expand = 3
  formula = G4_BERYLLIUM_OXIDE
  name = G4_BERYLLIUM_OXIDE
  specific = 4
FEATURE [App::DocumentObjectGroupPython] Bi_element001  label="Bi_element : 4"  # scripted group (container) (typed FeaturePython)
  n = 4
  ref = Bi_element
FEATURE [App::DocumentObjectGroupPython] Ge_element001  label="Ge_element : 3"  # scripted group (container) (typed FeaturePython)
  n = 3
  ref = Ge_element
FEATURE [App::DocumentObjectGroupPython] O_element012  label="O_element : 12"  # scripted group (container) (typed FeaturePython)
  n = 12
  ref = O_element
FEATURE [App::DocumentObjectGroupPython] G4_BGO  # scripted group (container) (typed FeaturePython)
  Dunit = g/cm3
  Dvalue = 7.13
  Group = -> [Bi_element001,Ge_element001,O_element012]
  conduct = 2
  density = 1
  expand = 3
  formula = G4_BGO
  name = G4_BGO
  specific = 4
FEATURE [App::DocumentObjectGroupPython] H_element014  label="H_element : 0.102"  # scripted group (container) (typed FeaturePython)
  n = 0.102
FEATURE [App::DocumentObjectGroupPython] C_element014  label="C_element : 0.110"  # scripted group (container) (typed FeaturePython)
  n = 0.11
FEATURE [App::DocumentObjectGroupPython] N_element009  label="N_element : 0.033"  # scripted group (container) (typed FeaturePython)
  n = 0.033
FEATURE [App::DocumentObjectGroupPython] O_element013  label="O_element : 0.745"  # scripted group (container) (typed FeaturePython)
  n = 0.745
FEATURE [App::DocumentObjectGroupPython] Na_element002  label="Na_element : 0.002"  # scripted group (container) (typed FeaturePython)
  n = 0.001
FEATURE [App::DocumentObjectGroupPython] P_element001  label="P_element : 0.001"  # scripted group (container) (typed FeaturePython)
  n = 0.001
FEATURE [App::DocumentObjectGroupPython] S_element003  label="S_element : 0.002"  # scripted group (container) (typed FeaturePython)
  n = 0.002
FEATURE [App::DocumentObjectGroupPython] Cl_element002  label="Cl_element : 0.003"  # scripted group (container) (typed FeaturePython)
  n = 0.003
FEATURE [App::DocumentObjectGroupPython] K_element001  label="K_element : 0.002"  # scripted group (container) (typed FeaturePython)
  n = 0.002
FEATURE [App::DocumentObjectGroupPython] Fe_element001  label="Fe_element : 0.001"  # scripted group (container) (typed FeaturePython)
  n = 0.001
FEATURE [App::DocumentObjectGroupPython] G4_BLOOD_ICRP  # scripted group (container) (typed FeaturePython)
  Dunit = g/cm3
  Dvalue = 1.06
  Group = -> [H_element014,C_element014,N_element009,O_element013,Na_element002,P_element001,S_element003,Cl_element002,K_element001,Fe_element001]
  conduct = 2
  density = 1
  expand = 3
  formula = G4_BLOOD_ICRP
  name = G4_BLOOD_ICRP
  specific = 4
FEATURE [App::DocumentObjectGroupPython] H_element015  label="H_element : 0.064"  # scripted group (container) (typed FeaturePython)
  n = 0.064
FEATURE [App::DocumentObjectGroupPython] C_element015  label="C_element : 0.278"  # scripted group (container) (typed FeaturePython)
  n = 0.278
FEATURE [App::DocumentObjectGroupPython] N_element010  label="N_element : 0.027"  # scripted group (container) (typed FeaturePython)
  n = 0.027
FEATURE [App::DocumentObjectGroupPython] O_element014  label="O_element : 0.410"  # scripted group (container) (typed FeaturePython)
  n = 0.41
FEATURE [App::DocumentObjectGroupPython] Mg_element001  label="Mg_element : 0.002"  # scripted group (container) (typed FeaturePython)
  n = 0.002
FEATURE [App::DocumentObjectGroupPython] P_element002  label="P_element : 0.070"  # scripted group (container) (typed FeaturePython)
  n = 0.07
FEATURE [App::DocumentObjectGroupPython] S_element004  label="S_element : 0.003"  # scripted group (container) (typed FeaturePython)
  n = 0.002
FEATURE [App::DocumentObjectGroupPython] Ca_element003  label="Ca_element : 0.147"  # scripted group (container) (typed FeaturePython)
  n = 0.147
FEATURE [App::DocumentObjectGroupPython] G4_BONE_COMPACT_ICRU  # scripted group (container) (typed FeaturePython)
  Dunit = g/cm3
  Dvalue = 1.85
  Group = -> [H_element015,C_element015,N_element010,O_element014,Mg_element001,P_element002,S_element004,Ca_element003]
  conduct = 2
  density = 1
  expand = 3
  formula = G4_BONE_COMPACT_ICRU
  name = G4_BONE_COMPACT_ICRU
  specific = 4
FEATURE [App::DocumentObjectGroupPython] H_element016  label="H_element : 0.034"  # scripted group (container) (typed FeaturePython)
  n = 0.034
FEATURE [App::DocumentObjectGroupPython] C_element016  label="C_element : 0.155"  # scripted group (container) (typed FeaturePython)
  n = 0.155
FEATURE [App::DocumentObjectGroupPython] N_element011  label="N_element : 0.042"  # scripted group (container) (typed FeaturePython)
  n = 0.042
FEATURE [App::DocumentObjectGroupPython] O_element015  label="O_element : 0.435"  # scripted group (container) (typed FeaturePython)
  n = 0.435
FEATURE [App::DocumentObjectGroupPython] Na_element003  label="Na_element : 0.003"  # scripted group (container) (typed FeaturePython)
  n = 0.001
FEATURE [App::DocumentObjectGroupPython] Mg_element002  label="Mg_element : 0.003"  # scripted group (container) (typed FeaturePython)
  n = 0.002
FEATURE [App::DocumentObjectGroupPython] P_element003  label="P_element : 0.103"  # scripted group (container) (typed FeaturePython)
  n = 0.103
FEATURE [App::DocumentObjectGroupPython] S_element005  label="S_element : 0.004"  # scripted group (container) (typed FeaturePython)
  n = 0.003
FEATURE [App::DocumentObjectGroupPython] Ca_element004  label="Ca_element : 0.225"  # scripted group (container) (typed FeaturePython)
  n = 0.225
FEATURE [App::DocumentObjectGroupPython] G4_BONE_CORTICAL_ICRP  # scripted group (container) (typed FeaturePython)
  Dunit = g/cm3
  Dvalue = 1.92
  Group = -> [H_element016,C_element016,N_element011,O_element015,Na_element003,Mg_element002,P_element003,S_element005,Ca_element004]
  conduct = 2
  density = 1
  expand = 3
  formula = G4_BONE_CORTICAL_ICRP
  name = G4_BONE_CORTICAL_ICRP
  specific = 4
FEATURE [App::DocumentObjectGroupPython] B_element001  label="B_element : 4"  # scripted group (container) (typed FeaturePython)
  n = 4
  ref = B_element
FEATURE [App::DocumentObjectGroupPython] C_element017  label="C_element : 1"  # scripted group (container) (typed FeaturePython)
  n = 1
  ref = C_element
FEATURE [App::DocumentObjectGroupPython] G4_BORON_CARBIDE  # scripted group (container) (typed FeaturePython)
  Dunit = g/cm3
  Dvalue = 2.52
  Group = -> [B_element001,C_element017]
  conduct = 2
  density = 1
  expand = 3
  formula = G4_BORON_CARBIDE
  name = G4_BORON_CARBIDE
  specific = 4
FEATURE [App::DocumentObjectGroupPython] B_element002  label="B_element : 2"  # scripted group (container) (typed FeaturePython)
  n = 2
  ref = B_element
FEATURE [App::DocumentObjectGroupPython] O_element016  label="O_element : 006"  # scripted group (container) (typed FeaturePython)
  n = 3
  ref = O_element
FEATURE [App::DocumentObjectGroupPython] G4_BORON_OXIDE  # scripted group (container) (typed FeaturePython)
  Dunit = g/cm3
  Dvalue = 1.812
  Group = -> [B_element002,O_element016]
  conduct = 2
  density = 1
  expand = 3
  formula = G4_BORON_OXIDE
  name = G4_BORON_OXIDE
  specific = 4
FEATURE [App::DocumentObjectGroupPython] H_element017  label="H_element : 0.107"  # scripted group (container) (typed FeaturePython)
  n = 0.107
FEATURE [App::DocumentObjectGroupPython] C_element018  label="C_element : 0.145"  # scripted group (container) (typed FeaturePython)
  n = 0.145
FEATURE [App::DocumentObjectGroupPython] N_element012  label="N_element : 0.022"  # scripted group (container) (typed FeaturePython)
  n = 0.022
FEATURE [App::DocumentObjectGroupPython] O_element017  label="O_element : 0.712"  # scripted group (container) (typed FeaturePython)
  n = 0.712
FEATURE [App::DocumentObjectGroupPython] Na_element004  label="Na_element : 0.004"  # scripted group (container) (typed FeaturePython)
  n = 0.002
FEATURE [App::DocumentObjectGroupPython] P_element004  label="P_element : 0.004"  # scripted group (container) (typed FeaturePython)
  n = 0.004
FEATURE [App::DocumentObjectGroupPython] S_element006  label="S_element : 0.005"  # scripted group (container) (typed FeaturePython)
  n = 0.002
FEATURE [App::DocumentObjectGroupPython] Cl_element003  label="Cl_element : 0.004"  # scripted group (container) (typed FeaturePython)
  n = 0.003
FEATURE [App::DocumentObjectGroupPython] K_element002  label="K_element : 0.003"  # scripted group (container) (typed FeaturePython)
  n = 0.003
FEATURE [App::DocumentObjectGroupPython] G4_BRAIN_ICRP  # scripted group (container) (typed FeaturePython)
  Dunit = g/cm3
  Dvalue = 1.04
  Group = -> [H_element017,C_element018,N_element012,O_element017,Na_element004,P_element004,S_element006,Cl_element003,K_element002]
  conduct = 2
  density = 1
  expand = 3
  formula = G4_BRAIN_ICRP
  name = G4_BRAIN_ICRP
  specific = 4
FEATURE [App::DocumentObjectGroupPython] C_element019  label="C_element : 4"  # scripted group (container) (typed FeaturePython)
  n = 4
  ref = C_element
FEATURE [App::DocumentObjectGroupPython] H_element018  label="H_element : 010"  # scripted group (container) (typed FeaturePython)
  n = 10
  ref = H_element
FEATURE [App::DocumentObjectGroupPython] G4_BUTANE  # scripted group (container) (typed FeaturePython)
  Dunit = g/cm3
  Dvalue = 0.00249343
  Group = -> [C_element019,H_element018]
  conduct = 2
  density = 1
  expand = 3
  formula = G4_BUTANE
  name = G4_BUTANE
  specific = 4
FEATURE [App::DocumentObjectGroupPython] C_element020  label="C_element : 008"  # scripted group (container) (typed FeaturePython)
  n = 4
  ref = C_element
FEATURE [App::DocumentObjectGroupPython] H_element019  label="H_element : 011"  # scripted group (container) (typed FeaturePython)
  n = 10
  ref = H_element
FEATURE [App::DocumentObjectGroupPython] O_element018  label="O_element : 007"  # scripted group (container) (typed FeaturePython)
  n = 1
  ref = O_element
FEATURE [App::DocumentObjectGroupPython] G4_N_BUTYL_ALCOHOL  label="G4_N-BUTYL_ALCOHOL"  # scripted group (container) (typed FeaturePython)
  Dunit = g/cm3
  Dvalue = 0.8098
  Group = -> [C_element020,H_element019,O_element018]
  conduct = 2
  density = 1
  expand = 3
  formula = G4_N-BUTYL_ALCOHOL
  name = G4_N-BUTYL_ALCOHOL
  specific = 4
FEATURE [App::DocumentObjectGroupPython] H_element020  label="H_element : 0.025"  # scripted group (container) (typed FeaturePython)
  n = 0.02468
FEATURE [App::DocumentObjectGroupPython] C_element021  label="C_element : 0.502"  # scripted group (container) (typed FeaturePython)
  n = 0.501611
FEATURE [App::DocumentObjectGroupPython] O_element019  label="O_element : 0.005"  # scripted group (container) (typed FeaturePython)
  n = 0.004527
FEATURE [App::DocumentObjectGroupPython] F_element004  label="F_element : 0.465"  # scripted group (container) (typed FeaturePython)
  n = 0.465209
FEATURE [App::DocumentObjectGroupPython] Si_element001  label="Si_element : 0.004"  # scripted group (container) (typed FeaturePython)
  n = 0.003973
FEATURE [App::DocumentObjectGroupPython] G4_C_552  label="G4_C-552"  # scripted group (container) (typed FeaturePython)
  Dunit = g/cm3
  Dvalue = 1.76
  Group = -> [H_element020,C_element021,O_element019,F_element004,Si_element001]
  conduct = 2
  density = 1
  expand = 3
  formula = G4_C-552
  name = G4_C-552
  specific = 4
FEATURE [App::DocumentObjectGroupPython] Cd_element001  label="Cd_element : 1"  # scripted group (container) (typed FeaturePython)
  n = 1
  ref = Cd_element
FEATURE [App::DocumentObjectGroupPython] Te_element001  label="Te_element : 1"  # scripted group (container) (typed FeaturePython)
  n = 1
  ref = Te_element
FEATURE [App::DocumentObjectGroupPython] G4_CADMIUM_TELLURIDE  # scripted group (container) (typed FeaturePython)
  Dunit = g/cm3
  Dvalue = 6.2
  Group = -> [Cd_element001,Te_element001]
  conduct = 2
  density = 1
  expand = 3
  formula = G4_CADMIUM_TELLURIDE
  name = G4_CADMIUM_TELLURIDE
  specific = 4
FEATURE [App::DocumentObjectGroupPython] Cd_element002  label="Cd_element : 002"  # scripted group (container) (typed FeaturePython)
  n = 1
  ref = Cd_element
FEATURE [App::DocumentObjectGroupPython] W_element001  label="W_element : 1"  # scripted group (container) (typed FeaturePython)
  n = 1
  ref = W_element
FEATURE [App::DocumentObjectGroupPython] O_element020  label="O_element : 008"  # scripted group (container) (typed FeaturePython)
  n = 4
  ref = O_element
FEATURE [App::DocumentObjectGroupPython] G4_CADMIUM_TUNGSTATE  # scripted group (container) (typed FeaturePython)
  Dunit = g/cm3
  Dvalue = 7.9
  Group = -> [Cd_element002,W_element001,O_element020]
  conduct = 2
  density = 1
  expand = 3
  formula = G4_CADMIUM_TUNGSTATE
  name = G4_CADMIUM_TUNGSTATE
  specific = 4
FEATURE [App::DocumentObjectGroupPython] Ca_element005  label="Ca_element : 1"  # scripted group (container) (typed FeaturePython)
  n = 1
  ref = Ca_element
FEATURE [App::DocumentObjectGroupPython] C_element022  label="C_element : 009"  # scripted group (container) (typed FeaturePython)
  n = 1
  ref = C_element
FEATURE [App::DocumentObjectGroupPython] O_element021  label="O_element : 009"  # scripted group (container) (typed FeaturePython)
  n = 3
  ref = O_element
FEATURE [App::DocumentObjectGroupPython] G4_CALCIUM_CARBONATE  # scripted group (container) (typed FeaturePython)
  Dunit = g/cm3
  Dvalue = 2.8
  Group = -> [Ca_element005,C_element022,O_element021]
  conduct = 2
  density = 1
  expand = 3
  formula = G4_CALCIUM_CARBONATE
  name = G4_CALCIUM_CARBONATE
  specific = 4
FEATURE [App::DocumentObjectGroupPython] Ca_element006  label="Ca_element : 002"  # scripted group (container) (typed FeaturePython)
  n = 1
  ref = Ca_element
FEATURE [App::DocumentObjectGroupPython] F_element005  label="F_element : 003"  # scripted group (container) (typed FeaturePython)
  n = 2
  ref = F_element
FEATURE [App::DocumentObjectGroupPython] G4_CALCIUM_FLUORIDE  # scripted group (container) (typed FeaturePython)
  Dunit = g/cm3
  Dvalue = 3.18
  Group = -> [Ca_element006,F_element005]
  conduct = 2
  density = 1
  expand = 3
  formula = G4_CALCIUM_FLUORIDE
  name = G4_CALCIUM_FLUORIDE
  specific = 4
FEATURE [App::DocumentObjectGroupPython] Ca_element007  label="Ca_element : 003"  # scripted group (container) (typed FeaturePython)
  n = 1
  ref = Ca_element
FEATURE [App::DocumentObjectGroupPython] O_element022  label="O_element : 010"  # scripted group (container) (typed FeaturePython)
  n = 1
  ref = O_element
FEATURE [App::DocumentObjectGroupPython] G4_CALCIUM_OXIDE  # scripted group (container) (typed FeaturePython)
  Dunit = g/cm3
  Dvalue = 3.3
  Group = -> [Ca_element007,O_element022]
  conduct = 2
  density = 1
  expand = 3
  formula = G4_CALCIUM_OXIDE
  name = G4_CALCIUM_OXIDE
  specific = 4
FEATURE [App::DocumentObjectGroupPython] Ca_element008  label="Ca_element : 004"  # scripted group (container) (typed FeaturePython)
  n = 1
  ref = Ca_element
FEATURE [App::DocumentObjectGroupPython] S_element007  label="S_element : 002"  # scripted group (container) (typed FeaturePython)
  n = 1
  ref = S_element
FEATURE [App::DocumentObjectGroupPython] O_element023  label="O_element : 011"  # scripted group (container) (typed FeaturePython)
  n = 4
  ref = O_element
FEATURE [App::DocumentObjectGroupPython] G4_CALCIUM_SULFATE  # scripted group (container) (typed FeaturePython)
  Dunit = g/cm3
  Dvalue = 2.96
  Group = -> [Ca_element008,S_element007,O_element023]
  conduct = 2
  density = 1
  expand = 3
  formula = G4_CALCIUM_SULFATE
  name = G4_CALCIUM_SULFATE
  specific = 4
FEATURE [App::DocumentObjectGroupPython] Ca_element009  label="Ca_element : 005"  # scripted group (container) (typed FeaturePython)
  n = 1
  ref = Ca_element
FEATURE [App::DocumentObjectGroupPython] W_element002  label="W_element : 002"  # scripted group (container) (typed FeaturePython)
  n = 1
  ref = W_element
FEATURE [App::DocumentObjectGroupPython] O_element024  label="O_element : 012"  # scripted group (container) (typed FeaturePython)
  n = 4
  ref = O_element
FEATURE [App::DocumentObjectGroupPython] G4_CALCIUM_TUNGSTATE  # scripted group (container) (typed FeaturePython)
  Dunit = g/cm3
  Dvalue = 6.062
  Group = -> [Ca_element009,W_element002,O_element024]
  conduct = 2
  density = 1
  expand = 3
  formula = G4_CALCIUM_TUNGSTATE
  name = G4_CALCIUM_TUNGSTATE
  specific = 4
FEATURE [App::DocumentObjectGroupPython] C_element023  label="C_element : 010"  # scripted group (container) (typed FeaturePython)
  n = 1
  ref = C_element
FEATURE [App::DocumentObjectGroupPython] O_element025  label="O_element : 013"  # scripted group (container) (typed FeaturePython)
  n = 2
  ref = O_element
FEATURE [App::DocumentObjectGroupPython] G4_CARBON_DIOXIDE  # scripted group (container) (typed FeaturePython)
  Dunit = g/cm3
  Dvalue = 0.00184212
  Group = -> [C_element023,O_element025]
  conduct = 2
  density = 1
  expand = 3
  formula = G4_CARBON_DIOXIDE
  name = G4_CARBON_DIOXIDE
  specific = 4
FEATURE [App::DocumentObjectGroupPython] C_element024  label="C_element : 011"  # scripted group (container) (typed FeaturePython)
  n = 1
  ref = C_element
FEATURE [App::DocumentObjectGroupPython] Cl_element004  label="Cl_element : 4"  # scripted group (container) (typed FeaturePython)
  n = 4
  ref = Cl_element
FEATURE [App::DocumentObjectGroupPython] G4_CARBON_TETRACHLORIDE  # scripted group (container) (typed FeaturePython)
  Dunit = g/cm3
  Dvalue = 1.594
  Group = -> [C_element024,Cl_element004]
  conduct = 2
  density = 1
  expand = 3
  formula = G4_CARBON_TETRACHLORIDE
  name = G4_CARBON_TETRACHLORIDE
  specific = 4
FEATURE [App::DocumentObjectGroupPython] C_element025  label="C_element : 012"  # scripted group (container) (typed FeaturePython)
  n = 6
  ref = C_element
FEATURE [App::DocumentObjectGroupPython] H_element021  label="H_element : 012"  # scripted group (container) (typed FeaturePython)
  n = 10
  ref = H_element
FEATURE [App::DocumentObjectGroupPython] O_element026  label="O_element : 5"  # scripted group (container) (typed FeaturePython)
  n = 5
  ref = O_element
FEATURE [App::DocumentObjectGroupPython] G4_CELLULOSE_CELLOPHANE  # scripted group (container) (typed FeaturePython)
  Dunit = g/cm3
  Dvalue = 1.42
  Group = -> [C_element025,H_element021,O_element026]
  conduct = 2
  density = 1
  expand = 3
  formula = G4_CELLULOSE_CELLOPHANE
  name = G4_CELLULOSE_CELLOPHANE
  specific = 4
FEATURE [App::DocumentObjectGroupPython] H_element022  label="H_element : 0.067"  # scripted group (container) (typed FeaturePython)
  n = 0.067125
FEATURE [App::DocumentObjectGroupPython] C_element026  label="C_element : 0.545"  # scripted group (container) (typed FeaturePython)
  n = 0.545403
FEATURE [App::DocumentObjectGroupPython] O_element027  label="O_element : 0.387"  # scripted group (container) (typed FeaturePython)
  n = 0.387472
FEATURE [App::DocumentObjectGroupPython] G4_CELLULOSE_BUTYRATE  # scripted group (container) (typed FeaturePython)
  Dunit = g/cm3
  Dvalue = 1.2
  Group = -> [H_element022,C_element026,O_element027]
  conduct = 2
  density = 1
  expand = 3
  formula = G4_CELLULOSE_BUTYRATE
  name = G4_CELLULOSE_BUTYRATE
  specific = 4
FEATURE [App::DocumentObjectGroupPython] H_element023  label="H_element : 0.029"  # scripted group (container) (typed FeaturePython)
  n = 0.029216
FEATURE [App::DocumentObjectGroupPython] C_element027  label="C_element : 0.271"  # scripted group (container) (typed FeaturePython)
  n = 0.271296
FEATURE [App::DocumentObjectGroupPython] N_element013  label="N_element : 0.121"  # scripted group (container) (typed FeaturePython)
  n = 0.121276
FEATURE [App::DocumentObjectGroupPython] O_element028  label="O_element : 0.578"  # scripted group (container) (typed FeaturePython)
  n = 0.578212
FEATURE [App::DocumentObjectGroupPython] G4_CELLULOSE_NITRATE  # scripted group (container) (typed FeaturePython)
  Dunit = g/cm3
  Dvalue = 1.49
  Group = -> [H_element023,C_element027,N_element013,O_element028]
  conduct = 2
  density = 1
  expand = 3
  formula = G4_CELLULOSE_NITRATE
  name = G4_CELLULOSE_NITRATE
  specific = 4
FEATURE [App::DocumentObjectGroupPython] H_element024  label="H_element : 0.108"  # scripted group (container) (typed FeaturePython)
  n = 0.107596
FEATURE [App::DocumentObjectGroupPython] N_element014  label="N_element : 0.001"  # scripted group (container) (typed FeaturePython)
  n = 0.0008
FEATURE [App::DocumentObjectGroupPython] O_element029  label="O_element : 0.875"  # scripted group (container) (typed FeaturePython)
  n = 0.874976
FEATURE [App::DocumentObjectGroupPython] S_element008  label="S_element : 0.015"  # scripted group (container) (typed FeaturePython)
  n = 0.014627
FEATURE [App::DocumentObjectGroupPython] Ce_element001  label="Ce_element : 0.002"  # scripted group (container) (typed FeaturePython)
  n = 0.002001
FEATURE [App::DocumentObjectGroupPython] G4_CERIC_SULFATE  # scripted group (container) (typed FeaturePython)
  Dunit = g/cm3
  Dvalue = 1.03
  Group = -> [H_element024,N_element014,O_element029,S_element008,Ce_element001]
  conduct = 2
  density = 1
  expand = 3
  formula = G4_CERIC_SULFATE
  name = G4_CERIC_SULFATE
  specific = 4
FEATURE [App::DocumentObjectGroupPython] Cs_element001  label="Cs_element : 1"  # scripted group (container) (typed FeaturePython)
  n = 1
  ref = Cs_element
FEATURE [App::DocumentObjectGroupPython] F_element006  label="F_element : 1"  # scripted group (container) (typed FeaturePython)
  n = 1
  ref = F_element
FEATURE [App::DocumentObjectGroupPython] G4_CESIUM_FLUORIDE  # scripted group (container) (typed FeaturePython)
  Dunit = g/cm3
  Dvalue = 4.115
  Group = -> [Cs_element001,F_element006]
  conduct = 2
  density = 1
  expand = 3
  formula = G4_CESIUM_FLUORIDE
  name = G4_CESIUM_FLUORIDE
  specific = 4
FEATURE [App::DocumentObjectGroupPython] Cs_element002  label="Cs_element : 002"  # scripted group (container) (typed FeaturePython)
  n = 1
  ref = Cs_element
FEATURE [App::DocumentObjectGroupPython] I_element001  label="I_element : 1"  # scripted group (container) (typed FeaturePython)
  n = 1
  ref = I_element
FEATURE [App::DocumentObjectGroupPython] G4_CESIUM_IODIDE001  label="G4_CESIUM_IODIDE"  # scripted group (container) (typed FeaturePython)
  Dunit = g/cm3
  Dvalue = 4.51
  Group = -> [Cs_element002,I_element001]
  conduct = 2
  density = 1
  expand = 3
  formula = G4_CESIUM_IODIDE
  name = G4_CESIUM_IODIDE
  specific = 4
FEATURE [App::DocumentObjectGroupPython] C_element028  label="C_element : 013"  # scripted group (container) (typed FeaturePython)
  n = 6
  ref = C_element
FEATURE [App::DocumentObjectGroupPython] H_element025  label="H_element : 013"  # scripted group (container) (typed FeaturePython)
  n = 5
  ref = H_element
FEATURE [App::DocumentObjectGroupPython] Cl_element005  label="Cl_element : 1"  # scripted group (container) (typed FeaturePython)
  n = 1
  ref = Cl_element
FEATURE [App::DocumentObjectGroupPython] G4_CHLOROBENZENE  # scripted group (container) (typed FeaturePython)
  Dunit = g/cm3
  Dvalue = 1.1058
  Group = -> [C_element028,H_element025,Cl_element005]
  conduct = 2
  density = 1
  expand = 3
  formula = G4_CHLOROBENZENE
  name = G4_CHLOROBENZENE
  specific = 4
FEATURE [App::DocumentObjectGroupPython] C_element029  label="C_element : 014"  # scripted group (container) (typed FeaturePython)
  n = 1
  ref = C_element
FEATURE [App::DocumentObjectGroupPython] H_element026  label="H_element : 1"  # scripted group (container) (typed FeaturePython)
  n = 1
  ref = H_element
FEATURE [App::DocumentObjectGroupPython] Cl_element006  label="Cl_element : 3"  # scripted group (container) (typed FeaturePython)
  n = 3
  ref = Cl_element
FEATURE [App::DocumentObjectGroupPython] G4_CHLOROFORM  # scripted group (container) (typed FeaturePython)
  Dunit = g/cm3
  Dvalue = 1.4832
  Group = -> [C_element029,H_element026,Cl_element006]
  conduct = 2
  density = 1
  expand = 3
  formula = G4_CHLOROFORM
  name = G4_CHLOROFORM
  specific = 4
FEATURE [App::DocumentObjectGroupPython] H_element027  label="H_element : 0.010"  # scripted group (container) (typed FeaturePython)
  n = 0.01
FEATURE [App::DocumentObjectGroupPython] C_element030  label="C_element : 0.001"  # scripted group (container) (typed FeaturePython)
  n = 0.001
FEATURE [App::DocumentObjectGroupPython] O_element030  label="O_element : 0.529"  # scripted group (container) (typed FeaturePython)
  n = 0.529107
FEATURE [App::DocumentObjectGroupPython] Na_element005  label="Na_element : 0.016"  # scripted group (container) (typed FeaturePython)
  n = 0.016
FEATURE [App::DocumentObjectGroupPython] Mg_element003  label="Mg_element : 0.004"  # scripted group (container) (typed FeaturePython)
  n = 0.002
FEATURE [App::DocumentObjectGroupPython] Al_element002  label="Al_element : 0.034"  # scripted group (container) (typed FeaturePython)
  n = 0.033872
FEATURE [App::DocumentObjectGroupPython] Si_element002  label="Si_element : 0.337"  # scripted group (container) (typed FeaturePython)
  n = 0.337021
FEATURE [App::DocumentObjectGroupPython] K_element003  label="K_element : 0.013"  # scripted group (container) (typed FeaturePython)
  n = 0.013
FEATURE [App::DocumentObjectGroupPython] Ca_element010  label="Ca_element : 0.044"  # scripted group (container) (typed FeaturePython)
  n = 0.044
FEATURE [App::DocumentObjectGroupPython] Fe_element002  label="Fe_element : 0.014"  # scripted group (container) (typed FeaturePython)
  n = 0.014
FEATURE [App::DocumentObjectGroupPython] G4_CONCRETE  # scripted group (container) (typed FeaturePython)
  Dunit = g/cm3
  Dvalue = 2.3
  Group = -> [H_element027,C_element030,O_element030,Na_element005,Mg_element003,Al_element002,Si_element002,K_element003,Ca_element010,Fe_element002]
  conduct = 2
  density = 1
  expand = 3
  formula = G4_CONCRETE
  name = G4_CONCRETE
  specific = 4
FEATURE [App::DocumentObjectGroupPython] C_element031  label="C_element : 015"  # scripted group (container) (typed FeaturePython)
  n = 6
  ref = C_element
FEATURE [App::DocumentObjectGroupPython] H_element028  label="H_element : 12"  # scripted group (container) (typed FeaturePython)
  n = 12
  ref = H_element
FEATURE [App::DocumentObjectGroupPython] G4_CYCLOHEXANE  # scripted group (container) (typed FeaturePython)
  Dunit = g/cm3
  Dvalue = 0.779
  Group = -> [C_element031,H_element028]
  conduct = 2
  density = 1
  expand = 3
  formula = G4_CYCLOHEXANE
  name = G4_CYCLOHEXANE
  specific = 4
FEATURE [App::DocumentObjectGroupPython] C_element032  label="C_element : 016"  # scripted group (container) (typed FeaturePython)
  n = 6
  ref = C_element
FEATURE [App::DocumentObjectGroupPython] H_element029  label="H_element : 4"  # scripted group (container) (typed FeaturePython)
  n = 4
  ref = H_element
FEATURE [App::DocumentObjectGroupPython] Cl_element007  label="Cl_element : 2"  # scripted group (container) (typed FeaturePython)
  n = 2
  ref = Cl_element
FEATURE [App::DocumentObjectGroupPython] G4_1_2_DICHLOROBENZENE  label="G4_1.2-DICHLOROBENZENE"  # scripted group (container) (typed FeaturePython)
  Dunit = g/cm3
  Dvalue = 1.3048
  Group = -> [C_element032,H_element029,Cl_element007]
  conduct = 2
  density = 1
  expand = 3
  formula = G4_1.2-DICHLOROBENZENE
  name = G4_1.2-DICHLOROBENZENE
  specific = 4
FEATURE [App::DocumentObjectGroupPython] C_element033  label="C_element : 017"  # scripted group (container) (typed FeaturePython)
  n = 4
  ref = C_element
FEATURE [App::DocumentObjectGroupPython] H_element030  label="H_element : 8"  # scripted group (container) (typed FeaturePython)
  n = 8
  ref = H_element
FEATURE [App::DocumentObjectGroupPython] O_element031  label="O_element : 014"  # scripted group (container) (typed FeaturePython)
  n = 1
  ref = O_element
FEATURE [App::DocumentObjectGroupPython] Cl_element008  label="Cl_element : 005"  # scripted group (container) (typed FeaturePython)
  n = 2
  ref = Cl_element
FEATURE [App::DocumentObjectGroupPython] G4_DICHLORODIETHYL_ETHER  # scripted group (container) (typed FeaturePython)
  Dunit = g/cm3
  Dvalue = 1.2199
  Group = -> [C_element033,H_element030,O_element031,Cl_element008]
  conduct = 2
  density = 1
  expand = 3
  formula = G4_DICHLORODIETHYL_ETHER
  name = G4_DICHLORODIETHYL_ETHER
  specific = 4
FEATURE [App::DocumentObjectGroupPython] C_element034  label="C_element : 018"  # scripted group (container) (typed FeaturePython)
  n = 2
  ref = C_element
FEATURE [App::DocumentObjectGroupPython] H_element031  label="H_element : 014"  # scripted group (container) (typed FeaturePython)
  n = 4
  ref = H_element
FEATURE [App::DocumentObjectGroupPython] Cl_element009  label="Cl_element : 006"  # scripted group (container) (typed FeaturePython)
  n = 2
  ref = Cl_element
FEATURE [App::DocumentObjectGroupPython] G4_1_2_DICHLOROETHANE  label="G4_1.2-DICHLOROETHANE"  # scripted group (container) (typed FeaturePython)
  Dunit = g/cm3
  Dvalue = 1.2351
  Group = -> [C_element034,H_element031,Cl_element009]
  conduct = 2
  density = 1
  expand = 3
  formula = G4_1.2-DICHLOROETHANE
  name = G4_1.2-DICHLOROETHANE
  specific = 4
FEATURE [App::DocumentObjectGroupPython] C_element035  label="C_element : 019"  # scripted group (container) (typed FeaturePython)
  n = 4
  ref = C_element
FEATURE [App::DocumentObjectGroupPython] H_element032  label="H_element : 015"  # scripted group (container) (typed FeaturePython)
  n = 10
  ref = H_element
FEATURE [App::DocumentObjectGroupPython] O_element032  label="O_element : 015"  # scripted group (container) (typed FeaturePython)
  n = 1
  ref = O_element
FEATURE [App::DocumentObjectGroupPython] G4_DIETHYL_ETHER  # scripted group (container) (typed FeaturePython)
  Dunit = g/cm3
  Dvalue = 0.71378
  Group = -> [C_element035,H_element032,O_element032]
  conduct = 2
  density = 1
  expand = 3
  formula = G4_DIETHYL_ETHER
  name = G4_DIETHYL_ETHER
  specific = 4
FEATURE [App::DocumentObjectGroupPython] C_element036  label="C_element : 020"  # scripted group (container) (typed FeaturePython)
  n = 3
  ref = C_element
FEATURE [App::DocumentObjectGroupPython] H_element033  label="H_element : 016"  # scripted group (container) (typed FeaturePython)
  n = 7
  ref = H_element
FEATURE [App::DocumentObjectGroupPython] N_element015  label="N_element : 008"  # scripted group (container) (typed FeaturePython)
  n = 1
  ref = N_element
FEATURE [App::DocumentObjectGroupPython] O_element033  label="O_element : 016"  # scripted group (container) (typed FeaturePython)
  n = 1
  ref = O_element
FEATURE [App::DocumentObjectGroupPython] G4_N_N_DIMETHYL_FORMAMIDE  label="G4_N.N-DIMETHYL_FORMAMIDE"  # scripted group (container) (typed FeaturePython)
  Dunit = g/cm3
  Dvalue = 0.9487
  Group = -> [C_element036,H_element033,N_element015,O_element033]
  conduct = 2
  density = 1
  expand = 3
  formula = G4_N.N-DIMETHYL_FORMAMIDE
  name = G4_N.N-DIMETHYL_FORMAMIDE
  specific = 4
FEATURE [App::DocumentObjectGroupPython] C_element037  label="C_element : 021"  # scripted group (container) (typed FeaturePython)
  n = 2
  ref = C_element
FEATURE [App::DocumentObjectGroupPython] H_element034  label="H_element : 017"  # scripted group (container) (typed FeaturePython)
  n = 6
  ref = H_element
FEATURE [App::DocumentObjectGroupPython] O_element034  label="O_element : 017"  # scripted group (container) (typed FeaturePython)
  n = 1
  ref = O_element
FEATURE [App::DocumentObjectGroupPython] S_element009  label="S_element : 003"  # scripted group (container) (typed FeaturePython)
  n = 1
  ref = S_element
FEATURE [App::DocumentObjectGroupPython] G4_DIMETHYL_SULFOXIDE  # scripted group (container) (typed FeaturePython)
  Dunit = g/cm3
  Dvalue = 1.1014
  Group = -> [C_element037,H_element034,O_element034,S_element009]
  conduct = 2
  density = 1
  expand = 3
  formula = G4_DIMETHYL_SULFOXIDE
  name = G4_DIMETHYL_SULFOXIDE
  specific = 4
FEATURE [App::DocumentObjectGroupPython] C_element038  label="C_element : 022"  # scripted group (container) (typed FeaturePython)
  n = 2
  ref = C_element
FEATURE [App::DocumentObjectGroupPython] H_element035  label="H_element : 018"  # scripted group (container) (typed FeaturePython)
  n = 6
  ref = H_element
FEATURE [App::DocumentObjectGroupPython] G4_ETHANE  # scripted group (container) (typed FeaturePython)
  Dunit = g/cm3
  Dvalue = 0.00125324
  Group = -> [C_element038,H_element035]
  conduct = 2
  density = 1
  expand = 3
  formula = G4_ETHANE
  name = G4_ETHANE
  specific = 4
FEATURE [App::DocumentObjectGroupPython] C_element039  label="C_element : 023"  # scripted group (container) (typed FeaturePython)
  n = 2
  ref = C_element
FEATURE [App::DocumentObjectGroupPython] H_element036  label="H_element : 019"  # scripted group (container) (typed FeaturePython)
  n = 6
  ref = H_element
FEATURE [App::DocumentObjectGroupPython] O_element035  label="O_element : 018"  # scripted group (container) (typed FeaturePython)
  n = 1
  ref = O_element
FEATURE [App::DocumentObjectGroupPython] G4_ETHYL_ALCOHOL  # scripted group (container) (typed FeaturePython)
  Dunit = g/cm3
  Dvalue = 0.7893
  Group = -> [C_element039,H_element036,O_element035]
  conduct = 2
  density = 1
  expand = 3
  formula = G4_ETHYL_ALCOHOL
  name = G4_ETHYL_ALCOHOL
  specific = 4
FEATURE [App::DocumentObjectGroupPython] H_element037  label="H_element : 0.090"  # scripted group (container) (typed FeaturePython)
  n = 0.090027
FEATURE [App::DocumentObjectGroupPython] C_element040  label="C_element : 0.585"  # scripted group (container) (typed FeaturePython)
  n = 0.585182
FEATURE [App::DocumentObjectGroupPython] O_element036  label="O_element : 0.325"  # scripted group (container) (typed FeaturePython)
  n = 0.324791
FEATURE [App::DocumentObjectGroupPython] G4_ETHYL_CELLULOSE  # scripted group (container) (typed FeaturePython)
  Dunit = g/cm3
  Dvalue = 1.13
  Group = -> [H_element037,C_element040,O_element036]
  conduct = 2
  density = 1
  expand = 3
  formula = G4_ETHYL_CELLULOSE
  name = G4_ETHYL_CELLULOSE
  specific = 4
FEATURE [App::DocumentObjectGroupPython] C_element041  label="C_element : 024"  # scripted group (container) (typed FeaturePython)
  n = 2
  ref = C_element
FEATURE [App::DocumentObjectGroupPython] H_element038  label="H_element : 020"  # scripted group (container) (typed FeaturePython)
  n = 4
  ref = H_element
FEATURE [App::DocumentObjectGroupPython] G4_ETHYLENE  # scripted group (container) (typed FeaturePython)
  Dunit = g/cm3
  Dvalue = 0.00117497
  Group = -> [C_element041,H_element038]
  conduct = 2
  density = 1
  expand = 3
  formula = G4_ETHYLENE
  name = G4_ETHYLENE
  specific = 4
FEATURE [App::DocumentObjectGroupPython] H_element039  label="H_element : 0.096"  # scripted group (container) (typed FeaturePython)
  n = 0.096
FEATURE [App::DocumentObjectGroupPython] C_element042  label="C_element : 0.195"  # scripted group (container) (typed FeaturePython)
  n = 0.195
FEATURE [App::DocumentObjectGroupPython] N_element016  label="N_element : 0.057"  # scripted group (container) (typed FeaturePython)
  n = 0.057
FEATURE [App::DocumentObjectGroupPython] O_element037  label="O_element : 0.646"  # scripted group (container) (typed FeaturePython)
  n = 0.646
FEATURE [App::DocumentObjectGroupPython] Na_element006  label="Na_element : 0.017"  # scripted group (container) (typed FeaturePython)
  n = 0.001
FEATURE [App::DocumentObjectGroupPython] P_element005  label="P_element : 0.104"  # scripted group (container) (typed FeaturePython)
  n = 0.001
FEATURE [App::DocumentObjectGroupPython] S_element010  label="S_element : 0.016"  # scripted group (container) (typed FeaturePython)
  n = 0.003
FEATURE [App::DocumentObjectGroupPython] Cl_element010  label="Cl_element : 0.005"  # scripted group (container) (typed FeaturePython)
  n = 0.001
FEATURE [App::DocumentObjectGroupPython] G4_EYE_LENS_ICRP  # scripted group (container) (typed FeaturePython)
  Dunit = g/cm3
  Dvalue = 1.07
  Group = -> [H_element039,C_element042,N_element016,O_element037,Na_element006,P_element005,S_element010,Cl_element010]
  conduct = 2
  density = 1
  expand = 3
  formula = G4_EYE_LENS_ICRP
  name = G4_EYE_LENS_ICRP
  specific = 4
FEATURE [App::DocumentObjectGroupPython] Fe_element003  label="Fe_element : 2"  # scripted group (container) (typed FeaturePython)
  n = 2
  ref = Fe_element
FEATURE [App::DocumentObjectGroupPython] O_element038  label="O_element : 019"  # scripted group (container) (typed FeaturePython)
  n = 3
  ref = O_element
FEATURE [App::DocumentObjectGroupPython] G4_FERRIC_OXIDE  # scripted group (container) (typed FeaturePython)
  Dunit = g/cm3
  Dvalue = 5.2
  Group = -> [Fe_element003,O_element038]
  conduct = 2
  density = 1
  expand = 3
  formula = G4_FERRIC_OXIDE
  name = G4_FERRIC_OXIDE
  specific = 4
FEATURE [App::DocumentObjectGroupPython] Fe_element004  label="Fe_element : 1"  # scripted group (container) (typed FeaturePython)
  n = 1
  ref = Fe_element
FEATURE [App::DocumentObjectGroupPython] B_element003  label="B_element : 1"  # scripted group (container) (typed FeaturePython)
  n = 1
  ref = B_element
FEATURE [App::DocumentObjectGroupPython] G4_FERROBORIDE  # scripted group (container) (typed FeaturePython)
  Dunit = g/cm3
  Dvalue = 7.15
  Group = -> [Fe_element004,B_element003]
  conduct = 2
  density = 1
  expand = 3
  formula = G4_FERROBORIDE
  name = G4_FERROBORIDE
  specific = 4
FEATURE [App::DocumentObjectGroupPython] Fe_element005  label="Fe_element : 003"  # scripted group (container) (typed FeaturePython)
  n = 1
  ref = Fe_element
FEATURE [App::DocumentObjectGroupPython] O_element039  label="O_element : 020"  # scripted group (container) (typed FeaturePython)
  n = 1
  ref = O_element
FEATURE [App::DocumentObjectGroupPython] G4_FERROUS_OXIDE  # scripted group (container) (typed FeaturePython)
  Dunit = g/cm3
  Dvalue = 5.7
  Group = -> [Fe_element005,O_element039]
  conduct = 2
  density = 1
  expand = 3
  formula = G4_FERROUS_OXIDE
  name = G4_FERROUS_OXIDE
  specific = 4
FEATURE [App::DocumentObjectGroupPython] H_element040  label="H_element : 0.115"  # scripted group (container) (typed FeaturePython)
  n = 0.108259
FEATURE [App::DocumentObjectGroupPython] N_element017  label="N_element : 0.000"  # scripted group (container) (typed FeaturePython)
  n = 2.7e-05
FEATURE [App::DocumentObjectGroupPython] O_element040  label="O_element : 0.879"  # scripted group (container) (typed FeaturePython)
  n = 0.878636
FEATURE [App::DocumentObjectGroupPython] Na_element007  label="Na_element : 0.000"  # scripted group (container) (typed FeaturePython)
  n = 2.2e-05
FEATURE [App::DocumentObjectGroupPython] S_element011  label="S_element : 0.013"  # scripted group (container) (typed FeaturePython)
  n = 0.012968
FEATURE [App::DocumentObjectGroupPython] Cl_element011  label="Cl_element : 0.000"  # scripted group (container) (typed FeaturePython)
  n = 3.4e-05
FEATURE [App::DocumentObjectGroupPython] Fe_element006  label="Fe_element : 0.000"  # scripted group (container) (typed FeaturePython)
  n = 5.4e-05
FEATURE [App::DocumentObjectGroupPython] G4_FERROUS_SULFATE  # scripted group (container) (typed FeaturePython)
  Dunit = g/cm3
  Dvalue = 1.024
  Group = -> [H_element040,N_element017,O_element040,Na_element007,S_element011,Cl_element011,Fe_element006]
  conduct = 2
  density = 1
  expand = 3
  formula = G4_FERROUS_SULFATE
  name = G4_FERROUS_SULFATE
  specific = 4
FEATURE [App::DocumentObjectGroupPython] C_element043  label="C_element : 0.099"  # scripted group (container) (typed FeaturePython)
  n = 0.099335
FEATURE [App::DocumentObjectGroupPython] F_element007  label="F_element : 0.314"  # scripted group (container) (typed FeaturePython)
  n = 0.314247
FEATURE [App::DocumentObjectGroupPython] Cl_element012  label="Cl_element : 0.586"  # scripted group (container) (typed FeaturePython)
  n = 0.586418
FEATURE [App::DocumentObjectGroupPython] G4_FREON_12  label="G4_FREON-12"  # scripted group (container) (typed FeaturePython)
  Dunit = g/cm3
  Dvalue = 1.12
  Group = -> [C_element043,F_element007,Cl_element012]
  conduct = 2
  density = 1
  expand = 3
  formula = G4_FREON-12
  name = G4_FREON-12
  specific = 4
FEATURE [App::DocumentObjectGroupPython] C_element044  label="C_element : 0.057"  # scripted group (container) (typed FeaturePython)
  n = 0.057245
FEATURE [App::DocumentObjectGroupPython] F_element008  label="F_element : 0.181"  # scripted group (container) (typed FeaturePython)
  n = 0.181096
FEATURE [App::DocumentObjectGroupPython] Br_element001  label="Br_element : 0.762"  # scripted group (container) (typed FeaturePython)
  n = 0.761659
FEATURE [App::DocumentObjectGroupPython] G4_FREON_12B2  label="G4_FREON-12B2"  # scripted group (container) (typed FeaturePython)
  Dunit = g/cm3
  Dvalue = 1.8
  Group = -> [C_element044,F_element008,Br_element001]
  conduct = 2
  density = 1
  expand = 3
  formula = G4_FREON-12B2
  name = G4_FREON-12B2
  specific = 4
FEATURE [App::DocumentObjectGroupPython] C_element045  label="C_element : 0.115"  # scripted group (container) (typed FeaturePython)
  n = 0.114983
FEATURE [App::DocumentObjectGroupPython] F_element009  label="F_element : 0.546"  # scripted group (container) (typed FeaturePython)
  n = 0.545621
FEATURE [App::DocumentObjectGroupPython] Cl_element013  label="Cl_element : 0.339"  # scripted group (container) (typed FeaturePython)
  n = 0.339396
FEATURE [App::DocumentObjectGroupPython] G4_FREON_13  label="G4_FREON-13"  # scripted group (container) (typed FeaturePython)
  Dunit = g/cm3
  Dvalue = 0.95
  Group = -> [C_element045,F_element009,Cl_element013]
  conduct = 2
  density = 1
  expand = 3
  formula = G4_FREON-13
  name = G4_FREON-13
  specific = 4
FEATURE [App::DocumentObjectGroupPython] C_element046  label="C_element : 025"  # scripted group (container) (typed FeaturePython)
  n = 1
  ref = C_element
FEATURE [App::DocumentObjectGroupPython] F_element010  label="F_element : 3"  # scripted group (container) (typed FeaturePython)
  n = 3
  ref = F_element
FEATURE [App::DocumentObjectGroupPython] Br_element002  label="Br_element : 1"  # scripted group (container) (typed FeaturePython)
  n = 1
  ref = Br_element
FEATURE [App::DocumentObjectGroupPython] G4_FREON_13B1  label="G4_FREON-13B1"  # scripted group (container) (typed FeaturePython)
  Dunit = g/cm3
  Dvalue = 1.5
  Group = -> [C_element046,F_element010,Br_element002]
  conduct = 2
  density = 1
  expand = 3
  formula = G4_FREON-13B1
  name = G4_FREON-13B1
  specific = 4
FEATURE [App::DocumentObjectGroupPython] C_element047  label="C_element : 0.061"  # scripted group (container) (typed FeaturePython)
  n = 0.061309
FEATURE [App::DocumentObjectGroupPython] F_element011  label="F_element : 0.291"  # scripted group (container) (typed FeaturePython)
  n = 0.290924
FEATURE [App::DocumentObjectGroupPython] I_element002  label="I_element : 0.648"  # scripted group (container) (typed FeaturePython)
  n = 0.647767
FEATURE [App::DocumentObjectGroupPython] G4_FREON_13I1  label="G4_FREON-13I1"  # scripted group (container) (typed FeaturePython)
  Dunit = g/cm3
  Dvalue = 1.8
  Group = -> [C_element047,F_element011,I_element002]
  conduct = 2
  density = 1
  expand = 3
  formula = G4_FREON-13I1
  name = G4_FREON-13I1
  specific = 4
FEATURE [App::DocumentObjectGroupPython] Gd_element001  label="Gd_element : 2"  # scripted group (container) (typed FeaturePython)
  n = 2
  ref = Gd_element
FEATURE [App::DocumentObjectGroupPython] O_element041  label="O_element : 021"  # scripted group (container) (typed FeaturePython)
  n = 2
  ref = O_element
FEATURE [App::DocumentObjectGroupPython] S_element012  label="S_element : 004"  # scripted group (container) (typed FeaturePython)
  n = 1
  ref = S_element
FEATURE [App::DocumentObjectGroupPython] G4_GADOLINIUM_OXYSULFIDE  # scripted group (container) (typed FeaturePython)
  Dunit = g/cm3
  Dvalue = 7.44
  Group = -> [Gd_element001,O_element041,S_element012]
  conduct = 2
  density = 1
  expand = 3
  formula = G4_GADOLINIUM_OXYSULFIDE
  name = G4_GADOLINIUM_OXYSULFIDE
  specific = 4
FEATURE [App::DocumentObjectGroupPython] Ga_element001  label="Ga_element : 1"  # scripted group (container) (typed FeaturePython)
  n = 1
  ref = Ga_element
FEATURE [App::DocumentObjectGroupPython] As_element001  label="As_element : 1"  # scripted group (container) (typed FeaturePython)
  n = 1
  ref = As_element
FEATURE [App::DocumentObjectGroupPython] G4_GALLIUM_ARSENIDE  # scripted group (container) (typed FeaturePython)
  Dunit = g/cm3
  Dvalue = 5.31
  Group = -> [Ga_element001,As_element001]
  conduct = 2
  density = 1
  expand = 3
  formula = G4_GALLIUM_ARSENIDE
  name = G4_GALLIUM_ARSENIDE
  specific = 4
FEATURE [App::DocumentObjectGroupPython] H_element041  label="H_element : 0.081"  # scripted group (container) (typed FeaturePython)
  n = 0.08118
FEATURE [App::DocumentObjectGroupPython] C_element048  label="C_element : 0.416"  # scripted group (container) (typed FeaturePython)
  n = 0.41606
FEATURE [App::DocumentObjectGroupPython] N_element018  label="N_element : 0.111"  # scripted group (container) (typed FeaturePython)
  n = 0.11124
FEATURE [App::DocumentObjectGroupPython] O_element042  label="O_element : 0.381"  # scripted group (container) (typed FeaturePython)
  n = 0.38064
FEATURE [App::DocumentObjectGroupPython] S_element013  label="S_element : 0.011"  # scripted group (container) (typed FeaturePython)
  n = 0.01088
FEATURE [App::DocumentObjectGroupPython] G4_GEL_PHOTO_EMULSION  # scripted group (container) (typed FeaturePython)
  Dunit = g/cm3
  Dvalue = 1.2914
  Group = -> [H_element041,C_element048,N_element018,O_element042,S_element013]
  conduct = 2
  density = 1
  expand = 3
  formula = G4_GEL_PHOTO_EMULSION
  name = G4_GEL_PHOTO_EMULSION
  specific = 4
FEATURE [App::DocumentObjectGroupPython] B_element004  label="B_element : 0.040"  # scripted group (container) (typed FeaturePython)
  n = 0.0400639
FEATURE [App::DocumentObjectGroupPython] O_element043  label="O_element : 0.540"  # scripted group (container) (typed FeaturePython)
  n = 0.539561
FEATURE [App::DocumentObjectGroupPython] Na_element008  label="Na_element : 0.028"  # scripted group (container) (typed FeaturePython)
  n = 0.0281909
FEATURE [App::DocumentObjectGroupPython] Al_element003  label="Al_element : 0.012"  # scripted group (container) (typed FeaturePython)
  n = 0.011644
FEATURE [App::DocumentObjectGroupPython] Si_element003  label="Si_element : 0.377"  # scripted group (container) (typed FeaturePython)
  n = 0.377219
FEATURE [App::DocumentObjectGroupPython] K_element004  label="K_element : 0.014"  # scripted group (container) (typed FeaturePython)
  n = 0.00332099
FEATURE [App::DocumentObjectGroupPython] G4_Pyrex_Glass  # scripted group (container) (typed FeaturePython)
  Dunit = g/cm3
  Dvalue = 2.23
  Group = -> [B_element004,O_element043,Na_element008,Al_element003,Si_element003,K_element004]
  conduct = 2
  density = 1
  expand = 3
  formula = G4_Pyrex_Glass
  name = G4_Pyrex_Glass
  specific = 4
FEATURE [App::DocumentObjectGroupPython] O_element044  label="O_element : 0.156"  # scripted group (container) (typed FeaturePython)
  n = 0.156453
FEATURE [App::DocumentObjectGroupPython] Si_element004  label="Si_element : 0.081"  # scripted group (container) (typed FeaturePython)
  n = 0.080866
FEATURE [App::DocumentObjectGroupPython] Ti_element001  label="Ti_element : 0.008"  # scripted group (container) (typed FeaturePython)
  n = 0.008092
FEATURE [App::DocumentObjectGroupPython] As_element002  label="As_element : 0.003"  # scripted group (container) (typed FeaturePython)
  n = 0.002651
FEATURE [App::DocumentObjectGroupPython] Pb_element001  label="Pb_element : 0.752"  # scripted group (container) (typed FeaturePython)
  n = 0.751938
FEATURE [App::DocumentObjectGroupPython] G4_GLASS_LEAD  # scripted group (container) (typed FeaturePython)
  Dunit = g/cm3
  Dvalue = 6.22
  Group = -> [O_element044,Si_element004,Ti_element001,As_element002,Pb_element001]
  conduct = 2
  density = 1
  expand = 3
  formula = G4_GLASS_LEAD
  name = G4_GLASS_LEAD
  specific = 4
FEATURE [App::DocumentObjectGroupPython] O_element045  label="O_element : 0.460"  # scripted group (container) (typed FeaturePython)
  n = 0.4598
FEATURE [App::DocumentObjectGroupPython] Na_element009  label="Na_element : 0.096"  # scripted group (container) (typed FeaturePython)
  n = 0.0964411
FEATURE [App::DocumentObjectGroupPython] Si_element005  label="Si_element : 0.378"  # scripted group (container) (typed FeaturePython)
  n = 0.336553
FEATURE [App::DocumentObjectGroupPython] Ca_element011  label="Ca_element : 0.107"  # scripted group (container) (typed FeaturePython)
  n = 0.107205
FEATURE [App::DocumentObjectGroupPython] G4_GLASS_PLATE  # scripted group (container) (typed FeaturePython)
  Dunit = g/cm3
  Dvalue = 2.4
  Group = -> [O_element045,Na_element009,Si_element005,Ca_element011]
  conduct = 2
  density = 1
  expand = 3
  formula = G4_GLASS_PLATE
  name = G4_GLASS_PLATE
  specific = 4
FEATURE [App::DocumentObjectGroupPython] C_element049  label="C_element : 026"  # scripted group (container) (typed FeaturePython)
  n = 5
  ref = C_element
FEATURE [App::DocumentObjectGroupPython] H_element042  label="H_element : 021"  # scripted group (container) (typed FeaturePython)
  n = 10
  ref = H_element
FEATURE [App::DocumentObjectGroupPython] N_element019  label="N_element : 2"  # scripted group (container) (typed FeaturePython)
  n = 2
  ref = N_element
FEATURE [App::DocumentObjectGroupPython] O_element046  label="O_element : 022"  # scripted group (container) (typed FeaturePython)
  n = 3
  ref = O_element
FEATURE [App::DocumentObjectGroupPython] G4_GLUTAMINE  # scripted group (container) (typed FeaturePython)
  Dunit = g/cm3
  Dvalue = 1.46
  Group = -> [C_element049,H_element042,N_element019,O_element046]
  conduct = 2
  density = 1
  expand = 3
  formula = G4_GLUTAMINE
  name = G4_GLUTAMINE
  specific = 4
FEATURE [App::DocumentObjectGroupPython] C_element050  label="C_element : 027"  # scripted group (container) (typed FeaturePython)
  n = 3
  ref = C_element
FEATURE [App::DocumentObjectGroupPython] H_element043  label="H_element : 022"  # scripted group (container) (typed FeaturePython)
  n = 8
  ref = H_element
FEATURE [App::DocumentObjectGroupPython] O_element047  label="O_element : 023"  # scripted group (container) (typed FeaturePython)
  n = 3
  ref = O_element
FEATURE [App::DocumentObjectGroupPython] G4_GLYCEROL  # scripted group (container) (typed FeaturePython)
  Dunit = g/cm3
  Dvalue = 1.2613
  Group = -> [C_element050,H_element043,O_element047]
  conduct = 2
  density = 1
  expand = 3
  formula = G4_GLYCEROL
  name = G4_GLYCEROL
  specific = 4
FEATURE [App::DocumentObjectGroupPython] C_element051  label="C_element : 028"  # scripted group (container) (typed FeaturePython)
  n = 5
  ref = C_element
FEATURE [App::DocumentObjectGroupPython] H_element044  label="H_element : 023"  # scripted group (container) (typed FeaturePython)
  n = 5
  ref = H_element
FEATURE [App::DocumentObjectGroupPython] N_element020  label="N_element : 009"  # scripted group (container) (typed FeaturePython)
  n = 5
  ref = N_element
FEATURE [App::DocumentObjectGroupPython] O_element048  label="O_element : 024"  # scripted group (container) (typed FeaturePython)
  n = 1
  ref = O_element
FEATURE [App::DocumentObjectGroupPython] G4_GUANINE  # scripted group (container) (typed FeaturePython)
  Dunit = g/cm3
  Dvalue = 2.2
  Group = -> [C_element051,H_element044,N_element020,O_element048]
  conduct = 2
  density = 1
  expand = 3
  formula = G4_GUANINE
  name = G4_GUANINE
  specific = 4
FEATURE [App::DocumentObjectGroupPython] Ca_element012  label="Ca_element : 006"  # scripted group (container) (typed FeaturePython)
  n = 1
  ref = Ca_element
FEATURE [App::DocumentObjectGroupPython] S_element014  label="S_element : 005"  # scripted group (container) (typed FeaturePython)
  n = 1
  ref = S_element
FEATURE [App::DocumentObjectGroupPython] O_element049  label="O_element : 6"  # scripted group (container) (typed FeaturePython)
  n = 6
  ref = O_element
FEATURE [App::DocumentObjectGroupPython] H_element045  label="H_element : 024"  # scripted group (container) (typed FeaturePython)
  n = 4
  ref = H_element
FEATURE [App::DocumentObjectGroupPython] G4_GYPSUM  # scripted group (container) (typed FeaturePython)
  Dunit = g/cm3
  Dvalue = 2.32
  Group = -> [Ca_element012,S_element014,O_element049,H_element045]
  conduct = 2
  density = 1
  expand = 3
  formula = G4_GYPSUM
  name = G4_GYPSUM
  specific = 4
FEATURE [App::DocumentObjectGroupPython] C_element052  label="C_element : 7"  # scripted group (container) (typed FeaturePython)
  n = 7
  ref = C_element
FEATURE [App::DocumentObjectGroupPython] H_element046  label="H_element : 16"  # scripted group (container) (typed FeaturePython)
  n = 16
  ref = H_element
FEATURE [App::DocumentObjectGroupPython] G4_N_HEPTANE  label="G4_N-HEPTANE"  # scripted group (container) (typed FeaturePython)
  Dunit = g/cm3
  Dvalue = 0.68376
  Group = -> [C_element052,H_element046]
  conduct = 2
  density = 1
  expand = 3
  formula = G4_N-HEPTANE
  name = G4_N-HEPTANE
  specific = 4
FEATURE [App::DocumentObjectGroupPython] C_element053  label="C_element : 029"  # scripted group (container) (typed FeaturePython)
  n = 6
  ref = C_element
FEATURE [App::DocumentObjectGroupPython] H_element047  label="H_element : 14"  # scripted group (container) (typed FeaturePython)
  n = 14
  ref = H_element
FEATURE [App::DocumentObjectGroupPython] G4_N_HEXANE  label="G4_N-HEXANE"  # scripted group (container) (typed FeaturePython)
  Dunit = g/cm3
  Dvalue = 0.6603
  Group = -> [C_element053,H_element047]
  conduct = 2
  density = 1
  expand = 3
  formula = G4_N-HEXANE
  name = G4_N-HEXANE
  specific = 4
FEATURE [App::DocumentObjectGroupPython] C_element054  label="C_element : 22"  # scripted group (container) (typed FeaturePython)
  n = 22
  ref = C_element
FEATURE [App::DocumentObjectGroupPython] H_element048  label="H_element : 025"  # scripted group (container) (typed FeaturePython)
  n = 10
  ref = H_element
FEATURE [App::DocumentObjectGroupPython] N_element021  label="N_element : 010"  # scripted group (container) (typed FeaturePython)
  n = 2
  ref = N_element
FEATURE [App::DocumentObjectGroupPython] O_element050  label="O_element : 025"  # scripted group (container) (typed FeaturePython)
  n = 5
  ref = O_element
FEATURE [App::DocumentObjectGroupPython] G4_KAPTON  # scripted group (container) (typed FeaturePython)
  Dunit = g/cm3
  Dvalue = 1.42
  Group = -> [C_element054,H_element048,N_element021,O_element050]
  conduct = 2
  density = 1
  expand = 3
  formula = G4_KAPTON
  name = G4_KAPTON
  specific = 4
FEATURE [App::DocumentObjectGroupPython] La_element001  label="La_element : 1"  # scripted group (container) (typed FeaturePython)
  n = 1
  ref = La_element
FEATURE [App::DocumentObjectGroupPython] Br_element003  label="Br_element : 002"  # scripted group (container) (typed FeaturePython)
  n = 1
  ref = Br_element
FEATURE [App::DocumentObjectGroupPython] O_element051  label="O_element : 026"  # scripted group (container) (typed FeaturePython)
  n = 1
  ref = O_element
FEATURE [App::DocumentObjectGroupPython] G4_LANTHANUM_OXYBROMIDE  # scripted group (container) (typed FeaturePython)
  Dunit = g/cm3
  Dvalue = 6.28
  Group = -> [La_element001,Br_element003,O_element051]
  conduct = 2
  density = 1
  expand = 3
  formula = G4_LANTHANUM_OXYBROMIDE
  name = G4_LANTHANUM_OXYBROMIDE
  specific = 4
FEATURE [App::DocumentObjectGroupPython] La_element002  label="La_element : 2"  # scripted group (container) (typed FeaturePython)
  n = 2
  ref = La_element
FEATURE [App::DocumentObjectGroupPython] O_element052  label="O_element : 027"  # scripted group (container) (typed FeaturePython)
  n = 2
  ref = O_element
FEATURE [App::DocumentObjectGroupPython] S_element015  label="S_element : 006"  # scripted group (container) (typed FeaturePython)
  n = 1
  ref = S_element
FEATURE [App::DocumentObjectGroupPython] G4_LANTHANUM_OXYSULFIDE  # scripted group (container) (typed FeaturePython)
  Dunit = g/cm3
  Dvalue = 5.86
  Group = -> [La_element002,O_element052,S_element015]
  conduct = 2
  density = 1
  expand = 3
  formula = G4_LANTHANUM_OXYSULFIDE
  name = G4_LANTHANUM_OXYSULFIDE
  specific = 4
FEATURE [App::DocumentObjectGroupPython] O_element053  label="O_element : 0.072"  # scripted group (container) (typed FeaturePython)
  n = 0.071682
FEATURE [App::DocumentObjectGroupPython] Pb_element002  label="Pb_element : 0.928"  # scripted group (container) (typed FeaturePython)
  n = 0.928318
FEATURE [App::DocumentObjectGroupPython] G4_LEAD_OXIDE  # scripted group (container) (typed FeaturePython)
  Dunit = g/cm3
  Dvalue = 9.53
  Group = -> [O_element053,Pb_element002]
  conduct = 2
  density = 1
  expand = 3
  formula = G4_LEAD_OXIDE
  name = G4_LEAD_OXIDE
  specific = 4
FEATURE [App::DocumentObjectGroupPython] Li_element001  label="Li_element : 1"  # scripted group (container) (typed FeaturePython)
  n = 1
  ref = Li_element
FEATURE [App::DocumentObjectGroupPython] N_element022  label="N_element : 011"  # scripted group (container) (typed FeaturePython)
  n = 1
  ref = N_element
FEATURE [App::DocumentObjectGroupPython] H_element049  label="H_element : 026"  # scripted group (container) (typed FeaturePython)
  n = 2
  ref = H_element
FEATURE [App::DocumentObjectGroupPython] G4_LITHIUM_AMIDE  # scripted group (container) (typed FeaturePython)
  Dunit = g/cm3
  Dvalue = 1.178
  Group = -> [Li_element001,N_element022,H_element049]
  conduct = 2
  density = 1
  expand = 3
  formula = G4_LITHIUM_AMIDE
  name = G4_LITHIUM_AMIDE
  specific = 4
FEATURE [App::DocumentObjectGroupPython] Li_element002  label="Li_element : 2"  # scripted group (container) (typed FeaturePython)
  n = 2
  ref = Li_element
FEATURE [App::DocumentObjectGroupPython] C_element055  label="C_element : 030"  # scripted group (container) (typed FeaturePython)
  n = 1
  ref = C_element
FEATURE [App::DocumentObjectGroupPython] O_element054  label="O_element : 028"  # scripted group (container) (typed FeaturePython)
  n = 3
  ref = O_element
FEATURE [App::DocumentObjectGroupPython] G4_LITHIUM_CARBONATE  # scripted group (container) (typed FeaturePython)
  Dunit = g/cm3
  Dvalue = 2.11
  Group = -> [Li_element002,C_element055,O_element054]
  conduct = 2
  density = 1
  expand = 3
  formula = G4_LITHIUM_CARBONATE
  name = G4_LITHIUM_CARBONATE
  specific = 4
FEATURE [App::DocumentObjectGroupPython] Li_element003  label="Li_element : 003"  # scripted group (container) (typed FeaturePython)
  n = 1
  ref = Li_element
FEATURE [App::DocumentObjectGroupPython] F_element012  label="F_element : 004"  # scripted group (container) (typed FeaturePython)
  n = 1
  ref = F_element
FEATURE [App::DocumentObjectGroupPython] G4_LITHIUM_FLUORIDE  # scripted group (container) (typed FeaturePython)
  Dunit = g/cm3
  Dvalue = 2.635
  Group = -> [Li_element003,F_element012]
  conduct = 2
  density = 1
  expand = 3
  formula = G4_LITHIUM_FLUORIDE
  name = G4_LITHIUM_FLUORIDE
  specific = 4
FEATURE [App::DocumentObjectGroupPython] Li_element004  label="Li_element : 004"  # scripted group (container) (typed FeaturePython)
  n = 1
  ref = Li_element
FEATURE [App::DocumentObjectGroupPython] H_element050  label="H_element : 027"  # scripted group (container) (typed FeaturePython)
  n = 1
  ref = H_element
FEATURE [App::DocumentObjectGroupPython] G4_LITHIUM_HYDRIDE  # scripted group (container) (typed FeaturePython)
  Dunit = g/cm3
  Dvalue = 0.82
  Group = -> [Li_element004,H_element050]
  conduct = 2
  density = 1
  expand = 3
  formula = G4_LITHIUM_HYDRIDE
  name = G4_LITHIUM_HYDRIDE
  specific = 4
FEATURE [App::DocumentObjectGroupPython] Li_element005  label="Li_element : 005"  # scripted group (container) (typed FeaturePython)
  n = 1
  ref = Li_element
FEATURE [App::DocumentObjectGroupPython] I_element003  label="I_element : 002"  # scripted group (container) (typed FeaturePython)
  n = 1
  ref = I_element
FEATURE [App::DocumentObjectGroupPython] G4_LITHIUM_IODIDE  # scripted group (container) (typed FeaturePython)
  Dunit = g/cm3
  Dvalue = 3.494
  Group = -> [Li_element005,I_element003]
  conduct = 2
  density = 1
  expand = 3
  formula = G4_LITHIUM_IODIDE
  name = G4_LITHIUM_IODIDE
  specific = 4
FEATURE [App::DocumentObjectGroupPython] Li_element006  label="Li_element : 006"  # scripted group (container) (typed FeaturePython)
  n = 2
  ref = Li_element
FEATURE [App::DocumentObjectGroupPython] O_element055  label="O_element : 029"  # scripted group (container) (typed FeaturePython)
  n = 1
  ref = O_element
FEATURE [App::DocumentObjectGroupPython] G4_LITHIUM_OXIDE  # scripted group (container) (typed FeaturePython)
  Dunit = g/cm3
  Dvalue = 2.013
  Group = -> [Li_element006,O_element055]
  conduct = 2
  density = 1
  expand = 3
  formula = G4_LITHIUM_OXIDE
  name = G4_LITHIUM_OXIDE
  specific = 4
FEATURE [App::DocumentObjectGroupPython] Li_element007  label="Li_element : 007"  # scripted group (container) (typed FeaturePython)
  n = 2
  ref = Li_element
FEATURE [App::DocumentObjectGroupPython] B_element005  label="B_element : 005"  # scripted group (container) (typed FeaturePython)
  n = 4
  ref = B_element
FEATURE [App::DocumentObjectGroupPython] O_element056  label="O_element : 7"  # scripted group (container) (typed FeaturePython)
  n = 7
  ref = O_element
FEATURE [App::DocumentObjectGroupPython] G4_LITHIUM_TETRABORATE  # scripted group (container) (typed FeaturePython)
  Dunit = g/cm3
  Dvalue = 2.44
  Group = -> [Li_element007,B_element005,O_element056]
  conduct = 2
  density = 1
  expand = 3
  formula = G4_LITHIUM_TETRABORATE
  name = G4_LITHIUM_TETRABORATE
  specific = 4
FEATURE [App::DocumentObjectGroupPython] H_element051  label="H_element : 0.105"  # scripted group (container) (typed FeaturePython)
  n = 0.105
FEATURE [App::DocumentObjectGroupPython] C_element056  label="C_element : 0.083"  # scripted group (container) (typed FeaturePython)
  n = 0.083
FEATURE [App::DocumentObjectGroupPython] N_element023  label="N_element : 0.023"  # scripted group (container) (typed FeaturePython)
  n = 0.023
FEATURE [App::DocumentObjectGroupPython] O_element057  label="O_element : 0.779"  # scripted group (container) (typed FeaturePython)
  n = 0.779
FEATURE [App::DocumentObjectGroupPython] Na_element010  label="Na_element : 0.097"  # scripted group (container) (typed FeaturePython)
  n = 0.002
FEATURE [App::DocumentObjectGroupPython] P_element006  label="P_element : 0.105"  # scripted group (container) (typed FeaturePython)
  n = 0.001
FEATURE [App::DocumentObjectGroupPython] S_element016  label="S_element : 0.017"  # scripted group (container) (typed FeaturePython)
  n = 0.002
FEATURE [App::DocumentObjectGroupPython] Cl_element014  label="Cl_element : 0.587"  # scripted group (container) (typed FeaturePython)
  n = 0.003
FEATURE [App::DocumentObjectGroupPython] K_element005  label="K_element : 0.015"  # scripted group (container) (typed FeaturePython)
  n = 0.002
FEATURE [App::DocumentObjectGroupPython] G4_LUNG_ICRP  # scripted group (container) (typed FeaturePython)
  Dunit = g/cm3
  Dvalue = 1.04
  Group = -> [H_element051,C_element056,N_element023,O_element057,Na_element010,P_element006,S_element016,Cl_element014,K_element005]
  conduct = 2
  density = 1
  expand = 3
  formula = G4_LUNG_ICRP
  name = G4_LUNG_ICRP
  specific = 4
FEATURE [App::DocumentObjectGroupPython] H_element052  label="H_element : 0.116"  # scripted group (container) (typed FeaturePython)
  n = 0.114318
FEATURE [App::DocumentObjectGroupPython] C_element057  label="C_element : 0.656"  # scripted group (container) (typed FeaturePython)
  n = 0.655824
FEATURE [App::DocumentObjectGroupPython] O_element058  label="O_element : 0.092"  # scripted group (container) (typed FeaturePython)
  n = 0.0921831
FEATURE [App::DocumentObjectGroupPython] Mg_element004  label="Mg_element : 0.135"  # scripted group (container) (typed FeaturePython)
  n = 0.134792
FEATURE [App::DocumentObjectGroupPython] Ca_element013  label="Ca_element : 0.003"  # scripted group (container) (typed FeaturePython)
  n = 0.002883
FEATURE [App::DocumentObjectGroupPython] G4_M3_WAX  # scripted group (container) (typed FeaturePython)
  Dunit = g/cm3
  Dvalue = 1.05
  Group = -> [H_element052,C_element057,O_element058,Mg_element004,Ca_element013]
  conduct = 2
  density = 1
  expand = 3
  formula = G4_M3_WAX
  name = G4_M3_WAX
  specific = 4
FEATURE [App::DocumentObjectGroupPython] Mg_element005  label="Mg_element : 1"  # scripted group (container) (typed FeaturePython)
  n = 1
  ref = Mg_element
FEATURE [App::DocumentObjectGroupPython] C_element058  label="C_element : 031"  # scripted group (container) (typed FeaturePython)
  n = 1
  ref = C_element
FEATURE [App::DocumentObjectGroupPython] O_element059  label="O_element : 030"  # scripted group (container) (typed FeaturePython)
  n = 3
  ref = O_element
FEATURE [App::DocumentObjectGroupPython] G4_MAGNESIUM_CARBONATE  # scripted group (container) (typed FeaturePython)
  Dunit = g/cm3
  Dvalue = 2.958
  Group = -> [Mg_element005,C_element058,O_element059]
  conduct = 2
  density = 1
  expand = 3
  formula = G4_MAGNESIUM_CARBONATE
  name = G4_MAGNESIUM_CARBONATE
  specific = 4
FEATURE [App::DocumentObjectGroupPython] Mg_element006  label="Mg_element : 002"  # scripted group (container) (typed FeaturePython)
  n = 1
  ref = Mg_element
FEATURE [App::DocumentObjectGroupPython] F_element013  label="F_element : 005"  # scripted group (container) (typed FeaturePython)
  n = 2
  ref = F_element
FEATURE [App::DocumentObjectGroupPython] G4_MAGNESIUM_FLUORIDE  # scripted group (container) (typed FeaturePython)
  Dunit = g/cm3
  Dvalue = 3
  Group = -> [Mg_element006,F_element013]
  conduct = 2
  density = 1
  expand = 3
  formula = G4_MAGNESIUM_FLUORIDE
  name = G4_MAGNESIUM_FLUORIDE
  specific = 4
FEATURE [App::DocumentObjectGroupPython] Mg_element007  label="Mg_element : 003"  # scripted group (container) (typed FeaturePython)
  n = 1
  ref = Mg_element
FEATURE [App::DocumentObjectGroupPython] O_element060  label="O_element : 031"  # scripted group (container) (typed FeaturePython)
  n = 1
  ref = O_element
FEATURE [App::DocumentObjectGroupPython] G4_MAGNESIUM_OXIDE  # scripted group (container) (typed FeaturePython)
  Dunit = g/cm3
  Dvalue = 3.58
  Group = -> [Mg_element007,O_element060]
  conduct = 2
  density = 1
  expand = 3
  formula = G4_MAGNESIUM_OXIDE
  name = G4_MAGNESIUM_OXIDE
  specific = 4
FEATURE [App::DocumentObjectGroupPython] Mg_element008  label="Mg_element : 004"  # scripted group (container) (typed FeaturePython)
  n = 1
  ref = Mg_element
FEATURE [App::DocumentObjectGroupPython] B_element006  label="B_element : 006"  # scripted group (container) (typed FeaturePython)
  n = 4
  ref = B_element
FEATURE [App::DocumentObjectGroupPython] O_element061  label="O_element : 032"  # scripted group (container) (typed FeaturePython)
  n = 7
  ref = O_element
FEATURE [App::DocumentObjectGroupPython] G4_MAGNESIUM_TETRABORATE  # scripted group (container) (typed FeaturePython)
  Dunit = g/cm3
  Dvalue = 2.53
  Group = -> [Mg_element008,B_element006,O_element061]
  conduct = 2
  density = 1
  expand = 3
  formula = G4_MAGNESIUM_TETRABORATE
  name = G4_MAGNESIUM_TETRABORATE
  specific = 4
FEATURE [App::DocumentObjectGroupPython] Hg_element001  label="Hg_element : 1"  # scripted group (container) (typed FeaturePython)
  n = 1
  ref = Hg_element
FEATURE [App::DocumentObjectGroupPython] I_element004  label="I_element : 2"  # scripted group (container) (typed FeaturePython)
  n = 2
  ref = I_element
FEATURE [App::DocumentObjectGroupPython] G4_MERCURIC_IODIDE  # scripted group (container) (typed FeaturePython)
  Dunit = g/cm3
  Dvalue = 6.36
  Group = -> [Hg_element001,I_element004]
  conduct = 2
  density = 1
  expand = 3
  formula = G4_MERCURIC_IODIDE
  name = G4_MERCURIC_IODIDE
  specific = 4
FEATURE [App::DocumentObjectGroupPython] C_element059  label="C_element : 032"  # scripted group (container) (typed FeaturePython)
  n = 1
  ref = C_element
FEATURE [App::DocumentObjectGroupPython] H_element053  label="H_element : 028"  # scripted group (container) (typed FeaturePython)
  n = 4
  ref = H_element
FEATURE [App::DocumentObjectGroupPython] G4_METHANE  # scripted group (container) (typed FeaturePython)
  Dunit = g/cm3
  Dvalue = 0.000667151
  Group = -> [C_element059,H_element053]
  conduct = 2
  density = 1
  expand = 3
  formula = G4_METHANE
  name = G4_METHANE
  specific = 4
FEATURE [App::DocumentObjectGroupPython] C_element060  label="C_element : 033"  # scripted group (container) (typed FeaturePython)
  n = 1
  ref = C_element
FEATURE [App::DocumentObjectGroupPython] H_element054  label="H_element : 029"  # scripted group (container) (typed FeaturePython)
  n = 4
  ref = H_element
FEATURE [App::DocumentObjectGroupPython] O_element062  label="O_element : 033"  # scripted group (container) (typed FeaturePython)
  n = 1
  ref = O_element
FEATURE [App::DocumentObjectGroupPython] G4_METHANOL  # scripted group (container) (typed FeaturePython)
  Dunit = g/cm3
  Dvalue = 0.7914
  Group = -> [C_element060,H_element054,O_element062]
  conduct = 2
  density = 1
  expand = 3
  formula = G4_METHANOL
  name = G4_METHANOL
  specific = 4
FEATURE [App::DocumentObjectGroupPython] H_element055  label="H_element : 0.134"  # scripted group (container) (typed FeaturePython)
  n = 0.13404
FEATURE [App::DocumentObjectGroupPython] C_element061  label="C_element : 0.778"  # scripted group (container) (typed FeaturePython)
  n = 0.77796
FEATURE [App::DocumentObjectGroupPython] O_element063  label="O_element : 0.035"  # scripted group (container) (typed FeaturePython)
  n = 0.03502
FEATURE [App::DocumentObjectGroupPython] Mg_element009  label="Mg_element : 0.039"  # scripted group (container) (typed FeaturePython)
  n = 0.038594
FEATURE [App::DocumentObjectGroupPython] Ti_element002  label="Ti_element : 0.014"  # scripted group (container) (typed FeaturePython)
  n = 0.014386
FEATURE [App::DocumentObjectGroupPython] G4_MIX_D_WAX  # scripted group (container) (typed FeaturePython)
  Dunit = g/cm3
  Dvalue = 0.99
  Group = -> [H_element055,C_element061,O_element063,Mg_element009,Ti_element002]
  conduct = 2
  density = 1
  expand = 3
  formula = G4_MIX_D_WAX
  name = G4_MIX_D_WAX
  specific = 4
FEATURE [App::DocumentObjectGroupPython] H_element056  label="H_element : 0.135"  # scripted group (container) (typed FeaturePython)
  n = 0.081192
FEATURE [App::DocumentObjectGroupPython] C_element062  label="C_element : 0.583"  # scripted group (container) (typed FeaturePython)
  n = 0.583442
FEATURE [App::DocumentObjectGroupPython] N_element024  label="N_element : 0.018"  # scripted group (container) (typed FeaturePython)
  n = 0.017798
FEATURE [App::DocumentObjectGroupPython] O_element064  label="O_element : 0.186"  # scripted group (container) (typed FeaturePython)
  n = 0.186381
FEATURE [App::DocumentObjectGroupPython] Mg_element010  label="Mg_element : 0.130"  # scripted group (container) (typed FeaturePython)
  n = 0.130287
FEATURE [App::DocumentObjectGroupPython] Cl_element015  label="Cl_element : 0.588"  # scripted group (container) (typed FeaturePython)
  n = 0.0009
FEATURE [App::DocumentObjectGroupPython] G4_MS20_TISSUE  # scripted group (container) (typed FeaturePython)
  Dunit = g/cm3
  Dvalue = 1
  Group = -> [H_element056,C_element062,N_element024,O_element064,Mg_element010,Cl_element015]
  conduct = 2
  density = 1
  expand = 3
  formula = G4_MS20_TISSUE
  name = G4_MS20_TISSUE
  specific = 4
FEATURE [App::DocumentObjectGroupPython] H_element057  label="H_element : 0.136"  # scripted group (container) (typed FeaturePython)
  n = 0.102
FEATURE [App::DocumentObjectGroupPython] C_element063  label="C_element : 0.143"  # scripted group (container) (typed FeaturePython)
  n = 0.143
FEATURE [App::DocumentObjectGroupPython] N_element025  label="N_element : 0.034"  # scripted group (container) (typed FeaturePython)
  n = 0.034
FEATURE [App::DocumentObjectGroupPython] O_element065  label="O_element : 0.710"  # scripted group (container) (typed FeaturePython)
  n = 0.71
FEATURE [App::DocumentObjectGroupPython] Na_element011  label="Na_element : 0.098"  # scripted group (container) (typed FeaturePython)
  n = 0.001
FEATURE [App::DocumentObjectGroupPython] P_element007  label="P_element : 0.002"  # scripted group (container) (typed FeaturePython)
  n = 0.002
FEATURE [App::DocumentObjectGroupPython] S_element017  label="S_element : 0.018"  # scripted group (container) (typed FeaturePython)
  n = 0.003
FEATURE [App::DocumentObjectGroupPython] Cl_element016  label="Cl_element : 0.589"  # scripted group (container) (typed FeaturePython)
  n = 0.001
FEATURE [App::DocumentObjectGroupPython] K_element006  label="K_element : 0.004"  # scripted group (container) (typed FeaturePython)
  n = 0.004
FEATURE [App::DocumentObjectGroupPython] G4_MUSCLE_SKELETAL_ICRP  # scripted group (container) (typed FeaturePython)
  Dunit = g/cm3
  Dvalue = 1.05
  Group = -> [H_element057,C_element063,N_element025,O_element065,Na_element011,P_element007,S_element017,Cl_element016,K_element006]
  conduct = 2
  density = 1
  expand = 3
  formula = G4_MUSCLE_SKELETAL_ICRP
  name = G4_MUSCLE_SKELETAL_ICRP
  specific = 4
FEATURE [App::DocumentObjectGroupPython] H_element058  label="H_element : 0.137"  # scripted group (container) (typed FeaturePython)
  n = 0.102102
FEATURE [App::DocumentObjectGroupPython] C_element064  label="C_element : 0.123"  # scripted group (container) (typed FeaturePython)
  n = 0.123123
FEATURE [App::DocumentObjectGroupPython] N_element026  label="N_element : 0.756"  # scripted group (container) (typed FeaturePython)
  n = 0.035035
FEATURE [App::DocumentObjectGroupPython] O_element066  label="O_element : 0.730"  # scripted group (container) (typed FeaturePython)
  n = 0.72973
FEATURE [App::DocumentObjectGroupPython] Na_element012  label="Na_element : 0.099"  # scripted group (container) (typed FeaturePython)
  n = 0.001001
FEATURE [App::DocumentObjectGroupPython] P_element008  label="P_element : 0.106"  # scripted group (container) (typed FeaturePython)
  n = 0.002002
FEATURE [App::DocumentObjectGroupPython] S_element018  label="S_element : 0.019"  # scripted group (container) (typed FeaturePython)
  n = 0.004004
FEATURE [App::DocumentObjectGroupPython] K_element007  label="K_element : 0.016"  # scripted group (container) (typed FeaturePython)
  n = 0.003003
FEATURE [App::DocumentObjectGroupPython] G4_MUSCLE_STRIATED_ICRU  # scripted group (container) (typed FeaturePython)
  Dunit = g/cm3
  Dvalue = 1.04
  Group = -> [H_element058,C_element064,N_element026,O_element066,Na_element012,P_element008,S_element018,K_element007]
  conduct = 2
  density = 1
  expand = 3
  formula = G4_MUSCLE_STRIATED_ICRU
  name = G4_MUSCLE_STRIATED_ICRU
  specific = 4
FEATURE [App::DocumentObjectGroupPython] H_element059  label="H_element : 0.098"  # scripted group (container) (typed FeaturePython)
  n = 0.0982341
FEATURE [App::DocumentObjectGroupPython] C_element065  label="C_element : 0.156"  # scripted group (container) (typed FeaturePython)
  n = 0.156214
FEATURE [App::DocumentObjectGroupPython] N_element027  label="N_element : 0.757"  # scripted group (container) (typed FeaturePython)
  n = 0.035451
FEATURE [App::DocumentObjectGroupPython] O_element067  label="O_element : 0.880"  # scripted group (container) (typed FeaturePython)
  n = 0.710101
FEATURE [App::DocumentObjectGroupPython] G4_MUSCLE_WITH_SUCROSE  # scripted group (container) (typed FeaturePython)
  Dunit = g/cm3
  Dvalue = 1.11
  Group = -> [H_element059,C_element065,N_element027,O_element067]
  conduct = 2
  density = 1
  expand = 3
  formula = G4_MUSCLE_WITH_SUCROSE
  name = G4_MUSCLE_WITH_SUCROSE
  specific = 4
FEATURE [App::DocumentObjectGroupPython] H_element060  label="H_element : 0.138"  # scripted group (container) (typed FeaturePython)
  n = 0.101969
FEATURE [App::DocumentObjectGroupPython] C_element066  label="C_element : 0.120"  # scripted group (container) (typed FeaturePython)
  n = 0.120058
FEATURE [App::DocumentObjectGroupPython] N_element028  label="N_element : 0.758"  # scripted group (container) (typed FeaturePython)
  n = 0.035451
FEATURE [App::DocumentObjectGroupPython] O_element068  label="O_element : 0.743"  # scripted group (container) (typed FeaturePython)
  n = 0.742522
FEATURE [App::DocumentObjectGroupPython] G4_MUSCLE_WITHOUT_SUCROSE  # scripted group (container) (typed FeaturePython)
  Dunit = g/cm3
  Dvalue = 1.07
  Group = -> [H_element060,C_element066,N_element028,O_element068]
  conduct = 2
  density = 1
  expand = 3
  formula = G4_MUSCLE_WITHOUT_SUCROSE
  name = G4_MUSCLE_WITHOUT_SUCROSE
  specific = 4
FEATURE [App::DocumentObjectGroupPython] C_element067  label="C_element : 10"  # scripted group (container) (typed FeaturePython)
  n = 10
  ref = C_element
FEATURE [App::DocumentObjectGroupPython] H_element061  label="H_element : 030"  # scripted group (container) (typed FeaturePython)
  n = 8
  ref = H_element
FEATURE [App::DocumentObjectGroupPython] G4_NAPHTHALENE  # scripted group (container) (typed FeaturePython)
  Dunit = g/cm3
  Dvalue = 1.145
  Group = -> [C_element067,H_element061]
  conduct = 2
  density = 1
  expand = 3
  formula = G4_NAPHTHALENE
  name = G4_NAPHTHALENE
  specific = 4
FEATURE [App::DocumentObjectGroupPython] C_element068  label="C_element : 034"  # scripted group (container) (typed FeaturePython)
  n = 6
  ref = C_element
FEATURE [App::DocumentObjectGroupPython] H_element062  label="H_element : 031"  # scripted group (container) (typed FeaturePython)
  n = 5
  ref = H_element
FEATURE [App::DocumentObjectGroupPython] N_element029  label="N_element : 012"  # scripted group (container) (typed FeaturePython)
  n = 1
  ref = N_element
FEATURE [App::DocumentObjectGroupPython] O_element069  label="O_element : 034"  # scripted group (container) (typed FeaturePython)
  n = 2
  ref = O_element
FEATURE [App::DocumentObjectGroupPython] G4_NITROBENZENE  # scripted group (container) (typed FeaturePython)
  Dunit = g/cm3
  Dvalue = 1.19867
  Group = -> [C_element068,H_element062,N_element029,O_element069]
  conduct = 2
  density = 1
  expand = 3
  formula = G4_NITROBENZENE
  name = G4_NITROBENZENE
  specific = 4
FEATURE [App::DocumentObjectGroupPython] N_element030  label="N_element : 013"  # scripted group (container) (typed FeaturePython)
  n = 2
  ref = N_element
FEATURE [App::DocumentObjectGroupPython] O_element070  label="O_element : 035"  # scripted group (container) (typed FeaturePython)
  n = 1
  ref = O_element
FEATURE [App::DocumentObjectGroupPython] G4_NITROUS_OXIDE  # scripted group (container) (typed FeaturePython)
  Dunit = g/cm3
  Dvalue = 0.00183094
  Group = -> [N_element030,O_element070]
  conduct = 2
  density = 1
  expand = 3
  formula = G4_NITROUS_OXIDE
  name = G4_NITROUS_OXIDE
  specific = 4
FEATURE [App::DocumentObjectGroupPython] H_element063  label="H_element : 0.104"  # scripted group (container) (typed FeaturePython)
  n = 0.103509
FEATURE [App::DocumentObjectGroupPython] C_element069  label="C_element : 0.648"  # scripted group (container) (typed FeaturePython)
  n = 0.648416
FEATURE [App::DocumentObjectGroupPython] N_element031  label="N_element : 0.100"  # scripted group (container) (typed FeaturePython)
  n = 0.0995361
FEATURE [App::DocumentObjectGroupPython] O_element071  label="O_element : 0.149"  # scripted group (container) (typed FeaturePython)
  n = 0.148539
FEATURE [App::DocumentObjectGroupPython] G4_NYLON_8062  label="G4_NYLON-8062"  # scripted group (container) (typed FeaturePython)
  Dunit = g/cm3
  Dvalue = 1.08
  Group = -> [H_element063,C_element069,N_element031,O_element071]
  conduct = 2
  density = 1
  expand = 3
  formula = G4_NYLON-8062
  name = G4_NYLON-8062
  specific = 4
FEATURE [App::DocumentObjectGroupPython] C_element070  label="C_element : 035"  # scripted group (container) (typed FeaturePython)
  n = 6
  ref = C_element
FEATURE [App::DocumentObjectGroupPython] H_element064  label="H_element : 11"  # scripted group (container) (typed FeaturePython)
  n = 11
  ref = H_element
FEATURE [App::DocumentObjectGroupPython] N_element032  label="N_element : 014"  # scripted group (container) (typed FeaturePython)
  n = 1
  ref = N_element
FEATURE [App::DocumentObjectGroupPython] O_element072  label="O_element : 036"  # scripted group (container) (typed FeaturePython)
  n = 1
  ref = O_element
FEATURE [App::DocumentObjectGroupPython] G4_NYLON_6_6  label="G4_NYLON-6-6"  # scripted group (container) (typed FeaturePython)
  Dunit = g/cm3
  Dvalue = 1.14
  Group = -> [C_element070,H_element064,N_element032,O_element072]
  conduct = 2
  density = 1
  expand = 3
  formula = G4_NYLON-6-6
  name = G4_NYLON-6-6
  specific = 4
FEATURE [App::DocumentObjectGroupPython] H_element065  label="H_element : 0.139"  # scripted group (container) (typed FeaturePython)
  n = 0.107062
FEATURE [App::DocumentObjectGroupPython] C_element071  label="C_element : 0.680"  # scripted group (container) (typed FeaturePython)
  n = 0.680449
FEATURE [App::DocumentObjectGroupPython] N_element033  label="N_element : 0.099"  # scripted group (container) (typed FeaturePython)
  n = 0.099189
FEATURE [App::DocumentObjectGroupPython] O_element073  label="O_element : 0.113"  # scripted group (container) (typed FeaturePython)
  n = 0.1133
FEATURE [App::DocumentObjectGroupPython] G4_NYLON_6_10  label="G4_NYLON-6-10"  # scripted group (container) (typed FeaturePython)
  Dunit = g/cm3
  Dvalue = 1.14
  Group = -> [H_element065,C_element071,N_element033,O_element073]
  conduct = 2
  density = 1
  expand = 3
  formula = G4_NYLON-6-10
  name = G4_NYLON-6-10
  specific = 4
FEATURE [App::DocumentObjectGroupPython] H_element066  label="H_element : 0.140"  # scripted group (container) (typed FeaturePython)
  n = 0.115476
FEATURE [App::DocumentObjectGroupPython] C_element072  label="C_element : 0.721"  # scripted group (container) (typed FeaturePython)
  n = 0.720818
FEATURE [App::DocumentObjectGroupPython] N_element034  label="N_element : 0.076"  # scripted group (container) (typed FeaturePython)
  n = 0.0764169
FEATURE [App::DocumentObjectGroupPython] O_element074  label="O_element : 0.087"  # scripted group (container) (typed FeaturePython)
  n = 0.0872889
FEATURE [App::DocumentObjectGroupPython] G4_NYLON_11_RILSAN  label="G4_NYLON-11_RILSAN"  # scripted group (container) (typed FeaturePython)
  Dunit = g/cm3
  Dvalue = 1.425
  Group = -> [H_element066,C_element072,N_element034,O_element074]
  conduct = 2
  density = 1
  expand = 3
  formula = G4_NYLON-11_RILSAN
  name = G4_NYLON-11_RILSAN
  specific = 4
FEATURE [App::DocumentObjectGroupPython] C_element073  label="C_element : 8"  # scripted group (container) (typed FeaturePython)
  n = 8
  ref = C_element
FEATURE [App::DocumentObjectGroupPython] H_element067  label="H_element : 18"  # scripted group (container) (typed FeaturePython)
  n = 18
  ref = H_element
FEATURE [App::DocumentObjectGroupPython] G4_OCTANE  # scripted group (container) (typed FeaturePython)
  Dunit = g/cm3
  Dvalue = 0.7026
  Group = -> [C_element073,H_element067]
  conduct = 2
  density = 1
  expand = 3
  formula = G4_OCTANE
  name = G4_OCTANE
  specific = 4
FEATURE [App::DocumentObjectGroupPython] C_element074  label="C_element : 25"  # scripted group (container) (typed FeaturePython)
  n = 25
  ref = C_element
FEATURE [App::DocumentObjectGroupPython] H_element068  label="H_element : 52"  # scripted group (container) (typed FeaturePython)
  n = 52
  ref = H_element
FEATURE [App::DocumentObjectGroupPython] G4_PARAFFIN  # scripted group (container) (typed FeaturePython)
  Dunit = g/cm3
  Dvalue = 0.93
  Group = -> [C_element074,H_element068]
  conduct = 2
  density = 1
  expand = 3
  formula = G4_PARAFFIN
  name = G4_PARAFFIN
  specific = 4
FEATURE [App::DocumentObjectGroupPython] C_element075  label="C_element : 036"  # scripted group (container) (typed FeaturePython)
  n = 5
  ref = C_element
FEATURE [App::DocumentObjectGroupPython] H_element069  label="H_element : 032"  # scripted group (container) (typed FeaturePython)
  n = 12
  ref = H_element
FEATURE [App::DocumentObjectGroupPython] G4_N_PENTANE  label="G4_N-PENTANE"  # scripted group (container) (typed FeaturePython)
  Dunit = g/cm3
  Dvalue = 0.6262
  Group = -> [C_element075,H_element069]
  conduct = 2
  density = 1
  expand = 3
  formula = G4_N-PENTANE
  name = G4_N-PENTANE
  specific = 4
FEATURE [App::DocumentObjectGroupPython] H_element070  label="H_element : 0.014"  # scripted group (container) (typed FeaturePython)
  n = 0.0141
FEATURE [App::DocumentObjectGroupPython] C_element076  label="C_element : 0.072"  # scripted group (container) (typed FeaturePython)
  n = 0.072261
FEATURE [App::DocumentObjectGroupPython] N_element035  label="N_element : 0.019"  # scripted group (container) (typed FeaturePython)
  n = 0.01932
FEATURE [App::DocumentObjectGroupPython] O_element075  label="O_element : 0.066"  # scripted group (container) (typed FeaturePython)
  n = 0.066101
FEATURE [App::DocumentObjectGroupPython] S_element019  label="S_element : 0.020"  # scripted group (container) (typed FeaturePython)
  n = 0.00189
FEATURE [App::DocumentObjectGroupPython] Br_element004  label="Br_element : 0.349"  # scripted group (container) (typed FeaturePython)
  n = 0.349103
FEATURE [App::DocumentObjectGroupPython] Ag_element001  label="Ag_element : 0.474"  # scripted group (container) (typed FeaturePython)
  n = 0.474105
FEATURE [App::DocumentObjectGroupPython] I_element005  label="I_element : 0.003"  # scripted group (container) (typed FeaturePython)
  n = 0.00312
FEATURE [App::DocumentObjectGroupPython] G4_PHOTO_EMULSION  # scripted group (container) (typed FeaturePython)
  Dunit = g/cm3
  Dvalue = 3.815
  Group = -> [H_element070,C_element076,N_element035,O_element075,S_element019,Br_element004,Ag_element001,I_element005]
  conduct = 2
  density = 1
  expand = 3
  formula = G4_PHOTO_EMULSION
  name = G4_PHOTO_EMULSION
  specific = 4
FEATURE [App::DocumentObjectGroupPython] C_element077  label="C_element : 9"  # scripted group (container) (typed FeaturePython)
  n = 9
  ref = C_element
FEATURE [App::DocumentObjectGroupPython] H_element071  label="H_element : 033"  # scripted group (container) (typed FeaturePython)
  n = 10
  ref = H_element
FEATURE [App::DocumentObjectGroupPython] G4_PLASTIC_SC_VINYLTOLUENE  # scripted group (container) (typed FeaturePython)
  Dunit = g/cm3
  Dvalue = 1.032
  Group = -> [C_element077,H_element071]
  conduct = 2
  density = 1
  expand = 3
  formula = G4_PLASTIC_SC_VINYLTOLUENE
  name = G4_PLASTIC_SC_VINYLTOLUENE
  specific = 4
FEATURE [App::DocumentObjectGroupPython] Pu_element001  label="Pu_element : 1"  # scripted group (container) (typed FeaturePython)
  n = 1
  ref = Pu_element
FEATURE [App::DocumentObjectGroupPython] O_element076  label="O_element : 037"  # scripted group (container) (typed FeaturePython)
  n = 2
  ref = O_element
FEATURE [App::DocumentObjectGroupPython] G4_PLUTONIUM_DIOXIDE  # scripted group (container) (typed FeaturePython)
  Dunit = g/cm3
  Dvalue = 11.46
  Group = -> [Pu_element001,O_element076]
  conduct = 2
  density = 1
  expand = 3
  formula = G4_PLUTONIUM_DIOXIDE
  name = G4_PLUTONIUM_DIOXIDE
  specific = 4
FEATURE [App::DocumentObjectGroupPython] C_element078  label="C_element : 037"  # scripted group (container) (typed FeaturePython)
  n = 3
  ref = C_element
FEATURE [App::DocumentObjectGroupPython] H_element072  label="H_element : 034"  # scripted group (container) (typed FeaturePython)
  n = 3
  ref = H_element
FEATURE [App::DocumentObjectGroupPython] N_element036  label="N_element : 015"  # scripted group (container) (typed FeaturePython)
  n = 1
  ref = N_element
FEATURE [App::DocumentObjectGroupPython] G4_POLYACRYLONITRILE  # scripted group (container) (typed FeaturePython)
  Dunit = g/cm3
  Dvalue = 1.17
  Group = -> [C_element078,H_element072,N_element036]
  conduct = 2
  density = 1
  expand = 3
  formula = G4_POLYACRYLONITRILE
  name = G4_POLYACRYLONITRILE
  specific = 4
FEATURE [App::DocumentObjectGroupPython] C_element079  label="C_element : 16"  # scripted group (container) (typed FeaturePython)
  n = 16
  ref = C_element
FEATURE [App::DocumentObjectGroupPython] H_element073  label="H_element : 035"  # scripted group (container) (typed FeaturePython)
  n = 14
  ref = H_element
FEATURE [App::DocumentObjectGroupPython] O_element077  label="O_element : 038"  # scripted group (container) (typed FeaturePython)
  n = 3
  ref = O_element
FEATURE [App::DocumentObjectGroupPython] G4_POLYCARBONATE  # scripted group (container) (typed FeaturePython)
  Dunit = g/cm3
  Dvalue = 1.2
  Group = -> [C_element079,H_element073,O_element077]
  conduct = 2
  density = 1
  expand = 3
  formula = G4_POLYCARBONATE
  name = G4_POLYCARBONATE
  specific = 4
FEATURE [App::DocumentObjectGroupPython] C_element080  label="C_element : 038"  # scripted group (container) (typed FeaturePython)
  n = 8
  ref = C_element
FEATURE [App::DocumentObjectGroupPython] H_element074  label="H_element : 036"  # scripted group (container) (typed FeaturePython)
  n = 7
  ref = H_element
FEATURE [App::DocumentObjectGroupPython] Cl_element017  label="Cl_element : 007"  # scripted group (container) (typed FeaturePython)
  n = 1
  ref = Cl_element
FEATURE [App::DocumentObjectGroupPython] G4_POLYCHLOROSTYRENE  # scripted group (container) (typed FeaturePython)
  Dunit = g/cm3
  Dvalue = 1.3
  Group = -> [C_element080,H_element074,Cl_element017]
  conduct = 2
  density = 1
  expand = 3
  formula = G4_POLYCHLOROSTYRENE
  name = G4_POLYCHLOROSTYRENE
  specific = 4
FEATURE [App::DocumentObjectGroupPython] C_element081  label="C_element : 039"  # scripted group (container) (typed FeaturePython)
  n = 1
  ref = C_element
FEATURE [App::DocumentObjectGroupPython] H_element075  label="H_element : 037"  # scripted group (container) (typed FeaturePython)
  n = 2
  ref = H_element
FEATURE [App::DocumentObjectGroupPython] G4_POLYETHYLENE  # scripted group (container) (typed FeaturePython)
  Dunit = g/cm3
  Dvalue = 0.94
  Group = -> [C_element081,H_element075]
  conduct = 2
  density = 1
  expand = 3
  formula = G4_POLYETHYLENE
  name = G4_POLYETHYLENE
  specific = 4
FEATURE [App::DocumentObjectGroupPython] C_element082  label="C_element : 040"  # scripted group (container) (typed FeaturePython)
  n = 10
  ref = C_element
FEATURE [App::DocumentObjectGroupPython] H_element076  label="H_element : 038"  # scripted group (container) (typed FeaturePython)
  n = 8
  ref = H_element
FEATURE [App::DocumentObjectGroupPython] O_element078  label="O_element : 039"  # scripted group (container) (typed FeaturePython)
  n = 4
  ref = O_element
FEATURE [App::DocumentObjectGroupPython] G4_MYLAR  # scripted group (container) (typed FeaturePython)
  Dunit = g/cm3
  Dvalue = 1.4
  Group = -> [C_element082,H_element076,O_element078]
  conduct = 2
  density = 1
  expand = 3
  formula = G4_MYLAR
  name = G4_MYLAR
  specific = 4
FEATURE [App::DocumentObjectGroupPython] C_element083  label="C_element : 041"  # scripted group (container) (typed FeaturePython)
  n = 5
  ref = C_element
FEATURE [App::DocumentObjectGroupPython] H_element077  label="H_element : 039"  # scripted group (container) (typed FeaturePython)
  n = 8
  ref = H_element
FEATURE [App::DocumentObjectGroupPython] O_element079  label="O_element : 040"  # scripted group (container) (typed FeaturePython)
  n = 2
  ref = O_element
FEATURE [App::DocumentObjectGroupPython] G4_PLEXIGLASS  # scripted group (container) (typed FeaturePython)
  Dunit = g/cm3
  Dvalue = 1.19
  Group = -> [C_element083,H_element077,O_element079]
  conduct = 2
  density = 1
  expand = 3
  formula = G4_PLEXIGLASS
  name = G4_PLEXIGLASS
  specific = 4
FEATURE [App::DocumentObjectGroupPython] C_element084  label="C_element : 042"  # scripted group (container) (typed FeaturePython)
  n = 1
  ref = C_element
FEATURE [App::DocumentObjectGroupPython] H_element078  label="H_element : 040"  # scripted group (container) (typed FeaturePython)
  n = 2
  ref = H_element
FEATURE [App::DocumentObjectGroupPython] O_element080  label="O_element : 041"  # scripted group (container) (typed FeaturePython)
  n = 1
  ref = O_element
FEATURE [App::DocumentObjectGroupPython] G4_POLYOXYMETHYLENE  # scripted group (container) (typed FeaturePython)
  Dunit = g/cm3
  Dvalue = 1.425
  Group = -> [C_element084,H_element078,O_element080]
  conduct = 2
  density = 1
  expand = 3
  formula = G4_POLYOXYMETHYLENE
  name = G4_POLYOXYMETHYLENE
  specific = 4
FEATURE [App::DocumentObjectGroupPython] C_element085  label="C_element : 043"  # scripted group (container) (typed FeaturePython)
  n = 2
  ref = C_element
FEATURE [App::DocumentObjectGroupPython] H_element079  label="H_element : 041"  # scripted group (container) (typed FeaturePython)
  n = 4
  ref = H_element
FEATURE [App::DocumentObjectGroupPython] G4_POLYPROPYLENE  # scripted group (container) (typed FeaturePython)
  Dunit = g/cm3
  Dvalue = 0.9
  Group = -> [C_element085,H_element079]
  conduct = 2
  density = 1
  expand = 3
  formula = G4_POLYPROPYLENE
  name = G4_POLYPROPYLENE
  specific = 4
FEATURE [App::DocumentObjectGroupPython] C_element086  label="C_element : 044"  # scripted group (container) (typed FeaturePython)
  n = 8
  ref = C_element
FEATURE [App::DocumentObjectGroupPython] H_element080  label="H_element : 042"  # scripted group (container) (typed FeaturePython)
  n = 8
  ref = H_element
FEATURE [App::DocumentObjectGroupPython] G4_POLYSTYRENE  # scripted group (container) (typed FeaturePython)
  Dunit = g/cm3
  Dvalue = 1.06
  Group = -> [C_element086,H_element080]
  conduct = 2
  density = 1
  expand = 3
  formula = G4_POLYSTYRENE
  name = G4_POLYSTYRENE
  specific = 4
FEATURE [App::DocumentObjectGroupPython] C_element087  label="C_element : 045"  # scripted group (container) (typed FeaturePython)
  n = 2
  ref = C_element
FEATURE [App::DocumentObjectGroupPython] F_element014  label="F_element : 4"  # scripted group (container) (typed FeaturePython)
  n = 4
  ref = F_element
FEATURE [App::DocumentObjectGroupPython] G4_TEFLON  # scripted group (container) (typed FeaturePython)
  Dunit = g/cm3
  Dvalue = 2.2
  Group = -> [C_element087,F_element014]
  conduct = 2
  density = 1
  expand = 3
  formula = G4_TEFLON
  name = G4_TEFLON
  specific = 4
FEATURE [App::DocumentObjectGroupPython] C_element088  label="C_element : 046"  # scripted group (container) (typed FeaturePython)
  n = 2
  ref = C_element
FEATURE [App::DocumentObjectGroupPython] F_element015  label="F_element : 006"  # scripted group (container) (typed FeaturePython)
  n = 3
  ref = F_element
FEATURE [App::DocumentObjectGroupPython] Cl_element018  label="Cl_element : 008"  # scripted group (container) (typed FeaturePython)
  n = 1
  ref = Cl_element
FEATURE [App::DocumentObjectGroupPython] G4_POLYTRIFLUOROCHLOROETHYLENE  # scripted group (container) (typed FeaturePython)
  Dunit = g/cm3
  Dvalue = 2.1
  Group = -> [C_element088,F_element015,Cl_element018]
  conduct = 2
  density = 1
  expand = 3
  formula = G4_POLYTRIFLUOROCHLOROETHYLENE
  name = G4_POLYTRIFLUOROCHLOROETHYLENE
  specific = 4
FEATURE [App::DocumentObjectGroupPython] C_element089  label="C_element : 047"  # scripted group (container) (typed FeaturePython)
  n = 4
  ref = C_element
FEATURE [App::DocumentObjectGroupPython] H_element081  label="H_element : 043"  # scripted group (container) (typed FeaturePython)
  n = 6
  ref = H_element
FEATURE [App::DocumentObjectGroupPython] O_element081  label="O_element : 042"  # scripted group (container) (typed FeaturePython)
  n = 2
  ref = O_element
FEATURE [App::DocumentObjectGroupPython] G4_POLYVINYL_ACETATE  # scripted group (container) (typed FeaturePython)
  Dunit = g/cm3
  Dvalue = 1.19
  Group = -> [C_element089,H_element081,O_element081]
  conduct = 2
  density = 1
  expand = 3
  formula = G4_POLYVINYL_ACETATE
  name = G4_POLYVINYL_ACETATE
  specific = 4
FEATURE [App::DocumentObjectGroupPython] C_element090  label="C_element : 048"  # scripted group (container) (typed FeaturePython)
  n = 2
  ref = C_element
FEATURE [App::DocumentObjectGroupPython] H_element082  label="H_element : 044"  # scripted group (container) (typed FeaturePython)
  n = 4
  ref = H_element
FEATURE [App::DocumentObjectGroupPython] O_element082  label="O_element : 043"  # scripted group (container) (typed FeaturePython)
  n = 1
  ref = O_element
FEATURE [App::DocumentObjectGroupPython] G4_POLYVINYL_ALCOHOL  # scripted group (container) (typed FeaturePython)
  Dunit = g/cm3
  Dvalue = 1.3
  Group = -> [C_element090,H_element082,O_element082]
  conduct = 2
  density = 1
  expand = 3
  formula = G4_POLYVINYL_ALCOHOL
  name = G4_POLYVINYL_ALCOHOL
  specific = 4
FEATURE [App::DocumentObjectGroupPython] C_element091  label="C_element : 049"  # scripted group (container) (typed FeaturePython)
  n = 8
  ref = C_element
FEATURE [App::DocumentObjectGroupPython] H_element083  label="H_element : 045"  # scripted group (container) (typed FeaturePython)
  n = 14
  ref = H_element
FEATURE [App::DocumentObjectGroupPython] O_element083  label="O_element : 044"  # scripted group (container) (typed FeaturePython)
  n = 2
  ref = O_element
FEATURE [App::DocumentObjectGroupPython] G4_POLYVINYL_BUTYRAL  # scripted group (container) (typed FeaturePython)
  Dunit = g/cm3
  Dvalue = 1.12
  Group = -> [C_element091,H_element083,O_element083]
  conduct = 2
  density = 1
  expand = 3
  formula = G4_POLYVINYL_BUTYRAL
  name = G4_POLYVINYL_BUTYRAL
  specific = 4
FEATURE [App::DocumentObjectGroupPython] C_element092  label="C_element : 050"  # scripted group (container) (typed FeaturePython)
  n = 2
  ref = C_element
FEATURE [App::DocumentObjectGroupPython] H_element084  label="H_element : 046"  # scripted group (container) (typed FeaturePython)
  n = 3
  ref = H_element
FEATURE [App::DocumentObjectGroupPython] Cl_element019  label="Cl_element : 009"  # scripted group (container) (typed FeaturePython)
  n = 1
  ref = Cl_element
FEATURE [App::DocumentObjectGroupPython] G4_POLYVINYL_CHLORIDE  # scripted group (container) (typed FeaturePython)
  Dunit = g/cm3
  Dvalue = 1.3
  Group = -> [C_element092,H_element084,Cl_element019]
  conduct = 2
  density = 1
  expand = 3
  formula = G4_POLYVINYL_CHLORIDE
  name = G4_POLYVINYL_CHLORIDE
  specific = 4
FEATURE [App::DocumentObjectGroupPython] C_element093  label="C_element : 051"  # scripted group (container) (typed FeaturePython)
  n = 2
  ref = C_element
FEATURE [App::DocumentObjectGroupPython] H_element085  label="H_element : 047"  # scripted group (container) (typed FeaturePython)
  n = 2
  ref = H_element
FEATURE [App::DocumentObjectGroupPython] Cl_element020  label="Cl_element : 010"  # scripted group (container) (typed FeaturePython)
  n = 2
  ref = Cl_element
FEATURE [App::DocumentObjectGroupPython] G4_POLYVINYLIDENE_CHLORIDE  # scripted group (container) (typed FeaturePython)
  Dunit = g/cm3
  Dvalue = 1.7
  Group = -> [C_element093,H_element085,Cl_element020]
  conduct = 2
  density = 1
  expand = 3
  formula = G4_POLYVINYLIDENE_CHLORIDE
  name = G4_POLYVINYLIDENE_CHLORIDE
  specific = 4
FEATURE [App::DocumentObjectGroupPython] C_element094  label="C_element : 052"  # scripted group (container) (typed FeaturePython)
  n = 2
  ref = C_element
FEATURE [App::DocumentObjectGroupPython] H_element086  label="H_element : 048"  # scripted group (container) (typed FeaturePython)
  n = 2
  ref = H_element
FEATURE [App::DocumentObjectGroupPython] F_element016  label="F_element : 007"  # scripted group (container) (typed FeaturePython)
  n = 2
  ref = F_element
FEATURE [App::DocumentObjectGroupPython] G4_POLYVINYLIDENE_FLUORIDE  # scripted group (container) (typed FeaturePython)
  Dunit = g/cm3
  Dvalue = 1.76
  Group = -> [C_element094,H_element086,F_element016]
  conduct = 2
  density = 1
  expand = 3
  formula = G4_POLYVINYLIDENE_FLUORIDE
  name = G4_POLYVINYLIDENE_FLUORIDE
  specific = 4
FEATURE [App::DocumentObjectGroupPython] C_element095  label="C_element : 053"  # scripted group (container) (typed FeaturePython)
  n = 6
  ref = C_element
FEATURE [App::DocumentObjectGroupPython] H_element087  label="H_element : 9"  # scripted group (container) (typed FeaturePython)
  n = 9
  ref = H_element
FEATURE [App::DocumentObjectGroupPython] N_element037  label="N_element : 016"  # scripted group (container) (typed FeaturePython)
  n = 1
  ref = N_element
FEATURE [App::DocumentObjectGroupPython] O_element084  label="O_element : 045"  # scripted group (container) (typed FeaturePython)
  n = 1
  ref = O_element
FEATURE [App::DocumentObjectGroupPython] G4_POLYVINYL_PYRROLIDONE  # scripted group (container) (typed FeaturePython)
  Dunit = g/cm3
  Dvalue = 1.25
  Group = -> [C_element095,H_element087,N_element037,O_element084]
  conduct = 2
  density = 1
  expand = 3
  formula = G4_POLYVINYL_PYRROLIDONE
  name = G4_POLYVINYL_PYRROLIDONE
  specific = 4
FEATURE [App::DocumentObjectGroupPython] K_element008  label="K_element : 1"  # scripted group (container) (typed FeaturePython)
  n = 1
  ref = K_element
FEATURE [App::DocumentObjectGroupPython] I_element006  label="I_element : 003"  # scripted group (container) (typed FeaturePython)
  n = 1
  ref = I_element
FEATURE [App::DocumentObjectGroupPython] G4_POTASSIUM_IODIDE  # scripted group (container) (typed FeaturePython)
  Dunit = g/cm3
  Dvalue = 3.13
  Group = -> [K_element008,I_element006]
  conduct = 2
  density = 1
  expand = 3
  formula = G4_POTASSIUM_IODIDE
  name = G4_POTASSIUM_IODIDE
  specific = 4
FEATURE [App::DocumentObjectGroupPython] K_element009  label="K_element : 2"  # scripted group (container) (typed FeaturePython)
  n = 2
  ref = K_element
FEATURE [App::DocumentObjectGroupPython] O_element085  label="O_element : 046"  # scripted group (container) (typed FeaturePython)
  n = 1
  ref = O_element
FEATURE [App::DocumentObjectGroupPython] G4_POTASSIUM_OXIDE  # scripted group (container) (typed FeaturePython)
  Dunit = g/cm3
  Dvalue = 2.32
  Group = -> [K_element009,O_element085]
  conduct = 2
  density = 1
  expand = 3
  formula = G4_POTASSIUM_OXIDE
  name = G4_POTASSIUM_OXIDE
  specific = 4
FEATURE [App::DocumentObjectGroupPython] C_element096  label="C_element : 054"  # scripted group (container) (typed FeaturePython)
  n = 3
  ref = C_element
FEATURE [App::DocumentObjectGroupPython] H_element088  label="H_element : 049"  # scripted group (container) (typed FeaturePython)
  n = 8
  ref = H_element
FEATURE [App::DocumentObjectGroupPython] G4_PROPANE  # scripted group (container) (typed FeaturePython)
  Dunit = g/cm3
  Dvalue = 0.00187939
  Group = -> [C_element096,H_element088]
  conduct = 2
  density = 1
  expand = 3
  formula = G4_PROPANE
  name = G4_PROPANE
  specific = 4
FEATURE [App::DocumentObjectGroupPython] C_element097  label="C_element : 055"  # scripted group (container) (typed FeaturePython)
  n = 3
  ref = C_element
FEATURE [App::DocumentObjectGroupPython] H_element089  label="H_element : 050"  # scripted group (container) (typed FeaturePython)
  n = 8
  ref = H_element
FEATURE [App::DocumentObjectGroupPython] G4_lPROPANE  # scripted group (container) (typed FeaturePython)
  Dunit = g/cm3
  Dvalue = 0.43
  Group = -> [C_element097,H_element089]
  conduct = 2
  density = 1
  expand = 3
  formula = G4_lPROPANE
  name = G4_lPROPANE
  specific = 4
FEATURE [App::DocumentObjectGroupPython] C_element098  label="C_element : 056"  # scripted group (container) (typed FeaturePython)
  n = 3
  ref = C_element
FEATURE [App::DocumentObjectGroupPython] H_element090  label="H_element : 051"  # scripted group (container) (typed FeaturePython)
  n = 8
  ref = H_element
FEATURE [App::DocumentObjectGroupPython] O_element086  label="O_element : 047"  # scripted group (container) (typed FeaturePython)
  n = 1
  ref = O_element
FEATURE [App::DocumentObjectGroupPython] G4_N_PROPYL_ALCOHOL  label="G4_N-PROPYL_ALCOHOL"  # scripted group (container) (typed FeaturePython)
  Dunit = g/cm3
  Dvalue = 0.8035
  Group = -> [C_element098,H_element090,O_element086]
  conduct = 2
  density = 1
  expand = 3
  formula = G4_N-PROPYL_ALCOHOL
  name = G4_N-PROPYL_ALCOHOL
  specific = 4
FEATURE [App::DocumentObjectGroupPython] C_element099  label="C_element : 057"  # scripted group (container) (typed FeaturePython)
  n = 5
  ref = C_element
FEATURE [App::DocumentObjectGroupPython] H_element091  label="H_element : 052"  # scripted group (container) (typed FeaturePython)
  n = 5
  ref = H_element
FEATURE [App::DocumentObjectGroupPython] N_element038  label="N_element : 017"  # scripted group (container) (typed FeaturePython)
  n = 1
  ref = N_element
FEATURE [App::DocumentObjectGroupPython] G4_PYRIDINE  # scripted group (container) (typed FeaturePython)
  Dunit = g/cm3
  Dvalue = 0.9819
  Group = -> [C_element099,H_element091,N_element038]
  conduct = 2
  density = 1
  expand = 3
  formula = G4_PYRIDINE
  name = G4_PYRIDINE
  specific = 4
FEATURE [App::DocumentObjectGroupPython] H_element092  label="H_element : 0.144"  # scripted group (container) (typed FeaturePython)
  n = 0.143711
FEATURE [App::DocumentObjectGroupPython] C_element100  label="C_element : 0.856"  # scripted group (container) (typed FeaturePython)
  n = 0.856289
FEATURE [App::DocumentObjectGroupPython] G4_RUBBER_BUTYL  # scripted group (container) (typed FeaturePython)
  Dunit = g/cm3
  Dvalue = 0.92
  Group = -> [H_element092,C_element100]
  conduct = 2
  density = 1
  expand = 3
  formula = G4_RUBBER_BUTYL
  name = G4_RUBBER_BUTYL
  specific = 4
FEATURE [App::DocumentObjectGroupPython] H_element093  label="H_element : 0.118"  # scripted group (container) (typed FeaturePython)
  n = 0.118371
FEATURE [App::DocumentObjectGroupPython] C_element101  label="C_element : 0.882"  # scripted group (container) (typed FeaturePython)
  n = 0.881629
FEATURE [App::DocumentObjectGroupPython] G4_RUBBER_NATURAL  # scripted group (container) (typed FeaturePython)
  Dunit = g/cm3
  Dvalue = 0.92
  Group = -> [H_element093,C_element101]
  conduct = 2
  density = 1
  expand = 3
  formula = G4_RUBBER_NATURAL
  name = G4_RUBBER_NATURAL
  specific = 4
FEATURE [App::DocumentObjectGroupPython] H_element094  label="H_element : 0.145"  # scripted group (container) (typed FeaturePython)
  n = 0.05692
FEATURE [App::DocumentObjectGroupPython] C_element102  label="C_element : 0.543"  # scripted group (container) (typed FeaturePython)
  n = 0.542646
FEATURE [App::DocumentObjectGroupPython] Cl_element021  label="Cl_element : 0.400"  # scripted group (container) (typed FeaturePython)
  n = 0.400434
FEATURE [App::DocumentObjectGroupPython] G4_RUBBER_NEOPRENE  # scripted group (container) (typed FeaturePython)
  Dunit = g/cm3
  Dvalue = 1.23
  Group = -> [H_element094,C_element102,Cl_element021]
  conduct = 2
  density = 1
  expand = 3
  formula = G4_RUBBER_NEOPRENE
  name = G4_RUBBER_NEOPRENE
  specific = 4
FEATURE [App::DocumentObjectGroupPython] Si_element006  label="Si_element : 1"  # scripted group (container) (typed FeaturePython)
  n = 1
  ref = Si_element
FEATURE [App::DocumentObjectGroupPython] O_element087  label="O_element : 048"  # scripted group (container) (typed FeaturePython)
  n = 2
  ref = O_element
FEATURE [App::DocumentObjectGroupPython] G4_SILICON_DIOXIDE002  label="G4_SILICON_DIOXIDE"  # scripted group (container) (typed FeaturePython)
  Dunit = g/cm3
  Dvalue = 2.32
  Group = -> [Si_element006,O_element087]
  conduct = 2
  density = 1
  expand = 3
  formula = G4_SILICON_DIOXIDE
  name = G4_SILICON_DIOXIDE
  specific = 4
FEATURE [App::DocumentObjectGroupPython] Ag_element002  label="Ag_element : 1"  # scripted group (container) (typed FeaturePython)
  n = 1
  ref = Ag_element
FEATURE [App::DocumentObjectGroupPython] Br_element005  label="Br_element : 003"  # scripted group (container) (typed FeaturePython)
  n = 1
  ref = Br_element
FEATURE [App::DocumentObjectGroupPython] G4_SILVER_BROMIDE  # scripted group (container) (typed FeaturePython)
  Dunit = g/cm3
  Dvalue = 6.473
  Group = -> [Ag_element002,Br_element005]
  conduct = 2
  density = 1
  expand = 3
  formula = G4_SILVER_BROMIDE
  name = G4_SILVER_BROMIDE
  specific = 4
FEATURE [App::DocumentObjectGroupPython] Ag_element003  label="Ag_element : 002"  # scripted group (container) (typed FeaturePython)
  n = 1
  ref = Ag_element
FEATURE [App::DocumentObjectGroupPython] Cl_element022  label="Cl_element : 011"  # scripted group (container) (typed FeaturePython)
  n = 1
  ref = Cl_element
FEATURE [App::DocumentObjectGroupPython] G4_SILVER_CHLORIDE  # scripted group (container) (typed FeaturePython)
  Dunit = g/cm3
  Dvalue = 5.56
  Group = -> [Ag_element003,Cl_element022]
  conduct = 2
  density = 1
  expand = 3
  formula = G4_SILVER_CHLORIDE
  name = G4_SILVER_CHLORIDE
  specific = 4
FEATURE [App::DocumentObjectGroupPython] Br_element006  label="Br_element : 0.423"  # scripted group (container) (typed FeaturePython)
  n = 0.422895
FEATURE [App::DocumentObjectGroupPython] Ag_element004  label="Ag_element : 0.574"  # scripted group (container) (typed FeaturePython)
  n = 0.573748
FEATURE [App::DocumentObjectGroupPython] I_element007  label="I_element : 0.649"  # scripted group (container) (typed FeaturePython)
  n = 0.003357
FEATURE [App::DocumentObjectGroupPython] G4_SILVER_HALIDES  # scripted group (container) (typed FeaturePython)
  Dunit = g/cm3
  Dvalue = 6.47
  Group = -> [Br_element006,Ag_element004,I_element007]
  conduct = 2
  density = 1
  expand = 3
  formula = G4_SILVER_HALIDES
  name = G4_SILVER_HALIDES
  specific = 4
FEATURE [App::DocumentObjectGroupPython] Ag_element005  label="Ag_element : 003"  # scripted group (container) (typed FeaturePython)
  n = 1
  ref = Ag_element
FEATURE [App::DocumentObjectGroupPython] I_element008  label="I_element : 004"  # scripted group (container) (typed FeaturePython)
  n = 1
  ref = I_element
FEATURE [App::DocumentObjectGroupPython] G4_SILVER_IODIDE  # scripted group (container) (typed FeaturePython)
  Dunit = g/cm3
  Dvalue = 6.01
  Group = -> [Ag_element005,I_element008]
  conduct = 2
  density = 1
  expand = 3
  formula = G4_SILVER_IODIDE
  name = G4_SILVER_IODIDE
  specific = 4
FEATURE [App::DocumentObjectGroupPython] H_element095  label="H_element : 0.100"  # scripted group (container) (typed FeaturePython)
  n = 0.1
FEATURE [App::DocumentObjectGroupPython] C_element103  label="C_element : 0.204"  # scripted group (container) (typed FeaturePython)
  n = 0.204
FEATURE [App::DocumentObjectGroupPython] N_element039  label="N_element : 0.759"  # scripted group (container) (typed FeaturePython)
  n = 0.042
FEATURE [App::DocumentObjectGroupPython] O_element088  label="O_element : 0.645"  # scripted group (container) (typed FeaturePython)
  n = 0.645
FEATURE [App::DocumentObjectGroupPython] Na_element013  label="Na_element : 0.100"  # scripted group (container) (typed FeaturePython)
  n = 0.002
FEATURE [App::DocumentObjectGroupPython] P_element009  label="P_element : 0.107"  # scripted group (container) (typed FeaturePython)
  n = 0.001
FEATURE [App::DocumentObjectGroupPython] S_element020  label="S_element : 0.021"  # scripted group (container) (typed FeaturePython)
  n = 0.002
FEATURE [App::DocumentObjectGroupPython] Cl_element023  label="Cl_element : 0.590"  # scripted group (container) (typed FeaturePython)
  n = 0.003
FEATURE [App::DocumentObjectGroupPython] K_element010  label="K_element : 0.001"  # scripted group (container) (typed FeaturePython)
  n = 0.001
FEATURE [App::DocumentObjectGroupPython] G4_SKIN_ICRP  # scripted group (container) (typed FeaturePython)
  Dunit = g/cm3
  Dvalue = 1.09
  Group = -> [H_element095,C_element103,N_element039,O_element088,Na_element013,P_element009,S_element020,Cl_element023,K_element010]
  conduct = 2
  density = 1
  expand = 3
  formula = G4_SKIN_ICRP
  name = G4_SKIN_ICRP
  specific = 4
FEATURE [App::DocumentObjectGroupPython] Na_element014  label="Na_element : 2"  # scripted group (container) (typed FeaturePython)
  n = 2
  ref = Na_element
FEATURE [App::DocumentObjectGroupPython] C_element104  label="C_element : 058"  # scripted group (container) (typed FeaturePython)
  n = 1
  ref = C_element
FEATURE [App::DocumentObjectGroupPython] O_element089  label="O_element : 049"  # scripted group (container) (typed FeaturePython)
  n = 3
  ref = O_element
FEATURE [App::DocumentObjectGroupPython] G4_SODIUM_CARBONATE  # scripted group (container) (typed FeaturePython)
  Dunit = g/cm3
  Dvalue = 2.532
  Group = -> [Na_element014,C_element104,O_element089]
  conduct = 2
  density = 1
  expand = 3
  formula = G4_SODIUM_CARBONATE
  name = G4_SODIUM_CARBONATE
  specific = 4
FEATURE [App::DocumentObjectGroupPython] Na_element015  label="Na_element : 1"  # scripted group (container) (typed FeaturePython)
  n = 1
  ref = Na_element
FEATURE [App::DocumentObjectGroupPython] I_element009  label="I_element : 005"  # scripted group (container) (typed FeaturePython)
  n = 1
  ref = I_element
FEATURE [App::DocumentObjectGroupPython] G4_SODIUM_IODIDE  # scripted group (container) (typed FeaturePython)
  Dunit = g/cm3
  Dvalue = 3.667
  Group = -> [Na_element015,I_element009]
  conduct = 2
  density = 1
  expand = 3
  formula = G4_SODIUM_IODIDE
  name = G4_SODIUM_IODIDE
  specific = 4
FEATURE [App::DocumentObjectGroupPython] Na_element016  label="Na_element : 003"  # scripted group (container) (typed FeaturePython)
  n = 2
  ref = Na_element
FEATURE [App::DocumentObjectGroupPython] O_element090  label="O_element : 050"  # scripted group (container) (typed FeaturePython)
  n = 1
  ref = O_element
FEATURE [App::DocumentObjectGroupPython] G4_SODIUM_MONOXIDE  # scripted group (container) (typed FeaturePython)
  Dunit = g/cm3
  Dvalue = 2.27
  Group = -> [Na_element016,O_element090]
  conduct = 2
  density = 1
  expand = 3
  formula = G4_SODIUM_MONOXIDE
  name = G4_SODIUM_MONOXIDE
  specific = 4
FEATURE [App::DocumentObjectGroupPython] Na_element017  label="Na_element : 004"  # scripted group (container) (typed FeaturePython)
  n = 1
  ref = Na_element
FEATURE [App::DocumentObjectGroupPython] N_element040  label="N_element : 018"  # scripted group (container) (typed FeaturePython)
  n = 1
  ref = N_element
FEATURE [App::DocumentObjectGroupPython] O_element091  label="O_element : 051"  # scripted group (container) (typed FeaturePython)
  n = 3
  ref = O_element
FEATURE [App::DocumentObjectGroupPython] G4_SODIUM_NITRATE  # scripted group (container) (typed FeaturePython)
  Dunit = g/cm3
  Dvalue = 2.261
  Group = -> [Na_element017,N_element040,O_element091]
  conduct = 2
  density = 1
  expand = 3
  formula = G4_SODIUM_NITRATE
  name = G4_SODIUM_NITRATE
  specific = 4
FEATURE [App::DocumentObjectGroupPython] C_element105  label="C_element : 059"  # scripted group (container) (typed FeaturePython)
  n = 14
  ref = C_element
FEATURE [App::DocumentObjectGroupPython] H_element096  label="H_element : 053"  # scripted group (container) (typed FeaturePython)
  n = 12
  ref = H_element
FEATURE [App::DocumentObjectGroupPython] G4_STILBENE  # scripted group (container) (typed FeaturePython)
  Dunit = g/cm3
  Dvalue = 0.9707
  Group = -> [C_element105,H_element096]
  conduct = 2
  density = 1
  expand = 3
  formula = G4_STILBENE
  name = G4_STILBENE
  specific = 4
FEATURE [App::DocumentObjectGroupPython] C_element106  label="C_element : 12"  # scripted group (container) (typed FeaturePython)
  n = 12
  ref = C_element
FEATURE [App::DocumentObjectGroupPython] H_element097  label="H_element : 22"  # scripted group (container) (typed FeaturePython)
  n = 22
  ref = H_element
FEATURE [App::DocumentObjectGroupPython] O_element092  label="O_element : 11"  # scripted group (container) (typed FeaturePython)
  n = 11
  ref = O_element
FEATURE [App::DocumentObjectGroupPython] G4_SUCROSE  # scripted group (container) (typed FeaturePython)
  Dunit = g/cm3
  Dvalue = 1.5805
  Group = -> [C_element106,H_element097,O_element092]
  conduct = 2
  density = 1
  expand = 3
  formula = G4_SUCROSE
  name = G4_SUCROSE
  specific = 4
FEATURE [App::DocumentObjectGroupPython] C_element107  label="C_element : 18"  # scripted group (container) (typed FeaturePython)
  n = 18
  ref = C_element
FEATURE [App::DocumentObjectGroupPython] H_element098  label="H_element : 054"  # scripted group (container) (typed FeaturePython)
  n = 14
  ref = H_element
FEATURE [App::DocumentObjectGroupPython] G4_TERPHENYL  # scripted group (container) (typed FeaturePython)
  Dunit = g/cm3
  Dvalue = 1.24
  Group = -> [C_element107,H_element098]
  conduct = 2
  density = 1
  expand = 3
  formula = G4_TERPHENYL
  name = G4_TERPHENYL
  specific = 4
FEATURE [App::DocumentObjectGroupPython] H_element099  label="H_element : 0.146"  # scripted group (container) (typed FeaturePython)
  n = 0.106
FEATURE [App::DocumentObjectGroupPython] C_element108  label="C_element : 0.883"  # scripted group (container) (typed FeaturePython)
  n = 0.099
FEATURE [App::DocumentObjectGroupPython] N_element041  label="N_element : 0.020"  # scripted group (container) (typed FeaturePython)
  n = 0.02
FEATURE [App::DocumentObjectGroupPython] O_element093  label="O_element : 0.766"  # scripted group (container) (typed FeaturePython)
  n = 0.766
FEATURE [App::DocumentObjectGroupPython] Na_element018  label="Na_element : 0.101"  # scripted group (container) (typed FeaturePython)
  n = 0.002
FEATURE [App::DocumentObjectGroupPython] P_element010  label="P_element : 0.108"  # scripted group (container) (typed FeaturePython)
  n = 0.001
FEATURE [App::DocumentObjectGroupPython] S_element021  label="S_element : 0.022"  # scripted group (container) (typed FeaturePython)
  n = 0.002
FEATURE [App::DocumentObjectGroupPython] Cl_element024  label="Cl_element : 0.002"  # scripted group (container) (typed FeaturePython)
  n = 0.002
FEATURE [App::DocumentObjectGroupPython] K_element011  label="K_element : 0.017"  # scripted group (container) (typed FeaturePython)
  n = 0.002
FEATURE [App::DocumentObjectGroupPython] G4_TESTIS_ICRP  # scripted group (container) (typed FeaturePython)
  Dunit = g/cm3
  Dvalue = 1.04
  Group = -> [H_element099,C_element108,N_element041,O_element093,Na_element018,P_element010,S_element021,Cl_element024,K_element011]
  conduct = 2
  density = 1
  expand = 3
  formula = G4_TESTIS_ICRP
  name = G4_TESTIS_ICRP
  specific = 4
FEATURE [App::DocumentObjectGroupPython] C_element109  label="C_element : 060"  # scripted group (container) (typed FeaturePython)
  n = 2
  ref = C_element
FEATURE [App::DocumentObjectGroupPython] Cl_element025  label="Cl_element : 012"  # scripted group (container) (typed FeaturePython)
  n = 4
  ref = Cl_element
FEATURE [App::DocumentObjectGroupPython] G4_TETRACHLOROETHYLENE  # scripted group (container) (typed FeaturePython)
  Dunit = g/cm3
  Dvalue = 1.625
  Group = -> [C_element109,Cl_element025]
  conduct = 2
  density = 1
  expand = 3
  formula = G4_TETRACHLOROETHYLENE
  name = G4_TETRACHLOROETHYLENE
  specific = 4
FEATURE [App::DocumentObjectGroupPython] Tl_element001  label="Tl_element : 1"  # scripted group (container) (typed FeaturePython)
  n = 1
  ref = Tl_element
FEATURE [App::DocumentObjectGroupPython] Cl_element026  label="Cl_element : 013"  # scripted group (container) (typed FeaturePython)
  n = 1
  ref = Cl_element
FEATURE [App::DocumentObjectGroupPython] G4_THALLIUM_CHLORIDE  # scripted group (container) (typed FeaturePython)
  Dunit = g/cm3
  Dvalue = 7.004
  Group = -> [Tl_element001,Cl_element026]
  conduct = 2
  density = 1
  expand = 3
  formula = G4_THALLIUM_CHLORIDE
  name = G4_THALLIUM_CHLORIDE
  specific = 4
FEATURE [App::DocumentObjectGroupPython] H_element100  label="H_element : 0.147"  # scripted group (container) (typed FeaturePython)
  n = 0.105
FEATURE [App::DocumentObjectGroupPython] C_element110  label="C_element : 0.256"  # scripted group (container) (typed FeaturePython)
  n = 0.256
FEATURE [App::DocumentObjectGroupPython] N_element042  label="N_element : 0.760"  # scripted group (container) (typed FeaturePython)
  n = 0.027
FEATURE [App::DocumentObjectGroupPython] O_element094  label="O_element : 0.602"  # scripted group (container) (typed FeaturePython)
  n = 0.602
FEATURE [App::DocumentObjectGroupPython] Na_element019  label="Na_element : 0.102"  # scripted group (container) (typed FeaturePython)
  n = 0.001
FEATURE [App::DocumentObjectGroupPython] P_element011  label="P_element : 0.109"  # scripted group (container) (typed FeaturePython)
  n = 0.002
FEATURE [App::DocumentObjectGroupPython] S_element022  label="S_element : 0.023"  # scripted group (container) (typed FeaturePython)
  n = 0.003
FEATURE [App::DocumentObjectGroupPython] Cl_element027  label="Cl_element : 0.591"  # scripted group (container) (typed FeaturePython)
  n = 0.002
FEATURE [App::DocumentObjectGroupPython] K_element012  label="K_element : 0.018"  # scripted group (container) (typed FeaturePython)
  n = 0.002
FEATURE [App::DocumentObjectGroupPython] G4_TISSUE_SOFT_ICRP  # scripted group (container) (typed FeaturePython)
  Dunit = g/cm3
  Dvalue = 1.03
  Group = -> [H_element100,C_element110,N_element042,O_element094,Na_element019,P_element011,S_element022,Cl_element027,K_element012]
  conduct = 2
  density = 1
  expand = 3
  formula = G4_TISSUE_SOFT_ICRP
  name = G4_TISSUE_SOFT_ICRP
  specific = 4
FEATURE [App::DocumentObjectGroupPython] H_element101  label="H_element : 0.148"  # scripted group (container) (typed FeaturePython)
  n = 0.101
FEATURE [App::DocumentObjectGroupPython] C_element111  label="C_element : 0.111"  # scripted group (container) (typed FeaturePython)
  n = 0.111
FEATURE [App::DocumentObjectGroupPython] N_element043  label="N_element : 0.026"  # scripted group (container) (typed FeaturePython)
  n = 0.026
FEATURE [App::DocumentObjectGroupPython] O_element095  label="O_element : 0.762"  # scripted group (container) (typed FeaturePython)
  n = 0.762
FEATURE [App::DocumentObjectGroupPython] G4_TISSUE_SOFT_ICRU_4  label="G4_TISSUE_SOFT_ICRU-4"  # scripted group (container) (typed FeaturePython)
  Dunit = g/cm3
  Dvalue = 1
  Group = -> [H_element101,C_element111,N_element043,O_element095]
  conduct = 2
  density = 1
  expand = 3
  formula = G4_TISSUE_SOFT_ICRU-4
  name = G4_TISSUE_SOFT_ICRU-4
  specific = 4
FEATURE [App::DocumentObjectGroupPython] H_element102  label="H_element : 0.149"  # scripted group (container) (typed FeaturePython)
  n = 0.101869
FEATURE [App::DocumentObjectGroupPython] C_element112  label="C_element : 0.456"  # scripted group (container) (typed FeaturePython)
  n = 0.456179
FEATURE [App::DocumentObjectGroupPython] N_element044  label="N_element : 0.761"  # scripted group (container) (typed FeaturePython)
  n = 0.035172
FEATURE [App::DocumentObjectGroupPython] O_element096  label="O_element : 0.407"  # scripted group (container) (typed FeaturePython)
  n = 0.40678
FEATURE [App::DocumentObjectGroupPython] G4_TISSUE_METHANE  label="G4_TISSUE-METHANE"  # scripted group (container) (typed FeaturePython)
  Dunit = g/cm3
  Dvalue = 0.00106409
  Group = -> [H_element102,C_element112,N_element044,O_element096]
  conduct = 2
  density = 1
  expand = 3
  formula = G4_TISSUE-METHANE
  name = G4_TISSUE-METHANE
  specific = 4
FEATURE [App::DocumentObjectGroupPython] H_element103  label="H_element : 0.103"  # scripted group (container) (typed FeaturePython)
  n = 0.102672
FEATURE [App::DocumentObjectGroupPython] C_element113  label="C_element : 0.569"  # scripted group (container) (typed FeaturePython)
  n = 0.56894
FEATURE [App::DocumentObjectGroupPython] N_element045  label="N_element : 0.762"  # scripted group (container) (typed FeaturePython)
  n = 0.035022
FEATURE [App::DocumentObjectGroupPython] O_element097  label="O_element : 0.293"  # scripted group (container) (typed FeaturePython)
  n = 0.293366
FEATURE [App::DocumentObjectGroupPython] G4_TISSUE_PROPANE  label="G4_TISSUE-PROPANE"  # scripted group (container) (typed FeaturePython)
  Dunit = g/cm3
  Dvalue = 0.00182628
  Group = -> [H_element103,C_element113,N_element045,O_element097]
  conduct = 2
  density = 1
  expand = 3
  formula = G4_TISSUE-PROPANE
  name = G4_TISSUE-PROPANE
  specific = 4
FEATURE [App::DocumentObjectGroupPython] Ti_element003  label="Ti_element : 1"  # scripted group (container) (typed FeaturePython)
  n = 1
  ref = Ti_element
FEATURE [App::DocumentObjectGroupPython] O_element098  label="O_element : 052"  # scripted group (container) (typed FeaturePython)
  n = 2
  ref = O_element
FEATURE [App::DocumentObjectGroupPython] G4_TITANIUM_DIOXIDE  # scripted group (container) (typed FeaturePython)
  Dunit = g/cm3
  Dvalue = 4.26
  Group = -> [Ti_element003,O_element098]
  conduct = 2
  density = 1
  expand = 3
  formula = G4_TITANIUM_DIOXIDE
  name = G4_TITANIUM_DIOXIDE
  specific = 4
FEATURE [App::DocumentObjectGroupPython] C_element114  label="C_element : 061"  # scripted group (container) (typed FeaturePython)
  n = 7
  ref = C_element
FEATURE [App::DocumentObjectGroupPython] H_element104  label="H_element : 055"  # scripted group (container) (typed FeaturePython)
  n = 8
  ref = H_element
FEATURE [App::DocumentObjectGroupPython] G4_TOLUENE  # scripted group (container) (typed FeaturePython)
  Dunit = g/cm3
  Dvalue = 0.8669
  Group = -> [C_element114,H_element104]
  conduct = 2
  density = 1
  expand = 3
  formula = G4_TOLUENE
  name = G4_TOLUENE
  specific = 4
FEATURE [App::DocumentObjectGroupPython] C_element115  label="C_element : 062"  # scripted group (container) (typed FeaturePython)
  n = 2
  ref = C_element
FEATURE [App::DocumentObjectGroupPython] H_element105  label="H_element : 056"  # scripted group (container) (typed FeaturePython)
  n = 1
  ref = H_element
FEATURE [App::DocumentObjectGroupPython] Cl_element028  label="Cl_element : 014"  # scripted group (container) (typed FeaturePython)
  n = 3
  ref = Cl_element
FEATURE [App::DocumentObjectGroupPython] G4_TRICHLOROETHYLENE  # scripted group (container) (typed FeaturePython)
  Dunit = g/cm3
  Dvalue = 1.46
  Group = -> [C_element115,H_element105,Cl_element028]
  conduct = 2
  density = 1
  expand = 3
  formula = G4_TRICHLOROETHYLENE
  name = G4_TRICHLOROETHYLENE
  specific = 4
FEATURE [App::DocumentObjectGroupPython] C_element116  label="C_element : 063"  # scripted group (container) (typed FeaturePython)
  n = 6
  ref = C_element
FEATURE [App::DocumentObjectGroupPython] H_element106  label="H_element : 15"  # scripted group (container) (typed FeaturePython)
  n = 15
  ref = H_element
FEATURE [App::DocumentObjectGroupPython] O_element099  label="O_element : 053"  # scripted group (container) (typed FeaturePython)
  n = 4
  ref = O_element
FEATURE [App::DocumentObjectGroupPython] P_element012  label="P_element : 1"  # scripted group (container) (typed FeaturePython)
  n = 1
  ref = P_element
FEATURE [App::DocumentObjectGroupPython] G4_TRIETHYL_PHOSPHATE  # scripted group (container) (typed FeaturePython)
  Dunit = g/cm3
  Dvalue = 1.07
  Group = -> [C_element116,H_element106,O_element099,P_element012]
  conduct = 2
  density = 1
  expand = 3
  formula = G4_TRIETHYL_PHOSPHATE
  name = G4_TRIETHYL_PHOSPHATE
  specific = 4
FEATURE [App::DocumentObjectGroupPython] W_element003  label="W_element : 003"  # scripted group (container) (typed FeaturePython)
  n = 1
  ref = W_element
FEATURE [App::DocumentObjectGroupPython] F_element017  label="F_element : 6"  # scripted group (container) (typed FeaturePython)
  n = 6
  ref = F_element
FEATURE [App::DocumentObjectGroupPython] G4_TUNGSTEN_HEXAFLUORIDE  # scripted group (container) (typed FeaturePython)
  Dunit = g/cm3
  Dvalue = 2.4
  Group = -> [W_element003,F_element017]
  conduct = 2
  density = 1
  expand = 3
  formula = G4_TUNGSTEN_HEXAFLUORIDE
  name = G4_TUNGSTEN_HEXAFLUORIDE
  specific = 4
FEATURE [App::DocumentObjectGroupPython] U_element001  label="U_element : 1"  # scripted group (container) (typed FeaturePython)
  n = 1
  ref = U_element
FEATURE [App::DocumentObjectGroupPython] C_element117  label="C_element : 064"  # scripted group (container) (typed FeaturePython)
  n = 2
  ref = C_element
FEATURE [App::DocumentObjectGroupPython] G4_URANIUM_DICARBIDE  # scripted group (container) (typed FeaturePython)
  Dunit = g/cm3
  Dvalue = 11.28
  Group = -> [U_element001,C_element117]
  conduct = 2
  density = 1
  expand = 3
  formula = G4_URANIUM_DICARBIDE
  name = G4_URANIUM_DICARBIDE
  specific = 4
FEATURE [App::DocumentObjectGroupPython] U_element002  label="U_element : 002"  # scripted group (container) (typed FeaturePython)
  n = 1
  ref = U_element
FEATURE [App::DocumentObjectGroupPython] C_element118  label="C_element : 065"  # scripted group (container) (typed FeaturePython)
  n = 1
  ref = C_element
FEATURE [App::DocumentObjectGroupPython] G4_URANIUM_MONOCARBIDE  # scripted group (container) (typed FeaturePython)
  Dunit = g/cm3
  Dvalue = 13.63
  Group = -> [U_element002,C_element118]
  conduct = 2
  density = 1
  expand = 3
  formula = G4_URANIUM_MONOCARBIDE
  name = G4_URANIUM_MONOCARBIDE
  specific = 4
FEATURE [App::DocumentObjectGroupPython] U_element003  label="U_element : 003"  # scripted group (container) (typed FeaturePython)
  n = 1
  ref = U_element
FEATURE [App::DocumentObjectGroupPython] O_element100  label="O_element : 054"  # scripted group (container) (typed FeaturePython)
  n = 2
  ref = O_element
FEATURE [App::DocumentObjectGroupPython] G4_URANIUM_OXIDE  # scripted group (container) (typed FeaturePython)
  Dunit = g/cm3
  Dvalue = 10.96
  Group = -> [U_element003,O_element100]
  conduct = 2
  density = 1
  expand = 3
  formula = G4_URANIUM_OXIDE
  name = G4_URANIUM_OXIDE
  specific = 4
FEATURE [App::DocumentObjectGroupPython] C_element119  label="C_element : 066"  # scripted group (container) (typed FeaturePython)
  n = 1
  ref = C_element
FEATURE [App::DocumentObjectGroupPython] H_element107  label="H_element : 057"  # scripted group (container) (typed FeaturePython)
  n = 4
  ref = H_element
FEATURE [App::DocumentObjectGroupPython] N_element046  label="N_element : 019"  # scripted group (container) (typed FeaturePython)
  n = 2
  ref = N_element
FEATURE [App::DocumentObjectGroupPython] O_element101  label="O_element : 055"  # scripted group (container) (typed FeaturePython)
  n = 1
  ref = O_element
FEATURE [App::DocumentObjectGroupPython] G4_UREA  # scripted group (container) (typed FeaturePython)
  Dunit = g/cm3
  Dvalue = 1.323
  Group = -> [C_element119,H_element107,N_element046,O_element101]
  conduct = 2
  density = 1
  expand = 3
  formula = G4_UREA
  name = G4_UREA
  specific = 4
FEATURE [App::DocumentObjectGroupPython] C_element120  label="C_element : 067"  # scripted group (container) (typed FeaturePython)
  n = 5
  ref = C_element
FEATURE [App::DocumentObjectGroupPython] H_element108  label="H_element : 058"  # scripted group (container) (typed FeaturePython)
  n = 11
  ref = H_element
FEATURE [App::DocumentObjectGroupPython] N_element047  label="N_element : 020"  # scripted group (container) (typed FeaturePython)
  n = 1
  ref = N_element
FEATURE [App::DocumentObjectGroupPython] O_element102  label="O_element : 056"  # scripted group (container) (typed FeaturePython)
  n = 2
  ref = O_element
FEATURE [App::DocumentObjectGroupPython] G4_VALINE  # scripted group (container) (typed FeaturePython)
  Dunit = g/cm3
  Dvalue = 1.23
  Group = -> [C_element120,H_element108,N_element047,O_element102]
  conduct = 2
  density = 1
  expand = 3
  formula = G4_VALINE
  name = G4_VALINE
  specific = 4
FEATURE [App::DocumentObjectGroupPython] H_element109  label="H_element : 0.009"  # scripted group (container) (typed FeaturePython)
  n = 0.009417
FEATURE [App::DocumentObjectGroupPython] C_element121  label="C_element : 0.281"  # scripted group (container) (typed FeaturePython)
  n = 0.280555
FEATURE [App::DocumentObjectGroupPython] F_element018  label="F_element : 0.710"  # scripted group (container) (typed FeaturePython)
  n = 0.710028
FEATURE [App::DocumentObjectGroupPython] G4_VITON  # scripted group (container) (typed FeaturePython)
  Dunit = g/cm3
  Dvalue = 1.8
  Group = -> [H_element109,C_element121,F_element018]
  conduct = 2
  density = 1
  expand = 3
  formula = G4_VITON
  name = G4_VITON
  specific = 4
FEATURE [App::DocumentObjectGroupPython] H_element110  label="H_element : 059"  # scripted group (container) (typed FeaturePython)
  n = 2
  ref = H_element
FEATURE [App::DocumentObjectGroupPython] O_element103  label="O_element : 057"  # scripted group (container) (typed FeaturePython)
  n = 1
  ref = O_element
FEATURE [App::DocumentObjectGroupPython] G4_WATER  # scripted group (container) (typed FeaturePython)
  Dunit = g/cm3
  Dvalue = 1
  Group = -> [H_element110,O_element103]
  conduct = 2
  density = 1
  expand = 3
  formula = G4_WATER
  name = G4_WATER
  specific = 4
FEATURE [App::DocumentObjectGroupPython] H_element111  label="H_element : 060"  # scripted group (container) (typed FeaturePython)
  n = 2
  ref = H_element
FEATURE [App::DocumentObjectGroupPython] O_element104  label="O_element : 058"  # scripted group (container) (typed FeaturePython)
  n = 1
  ref = O_element
FEATURE [App::DocumentObjectGroupPython] G4_WATER_VAPOR  # scripted group (container) (typed FeaturePython)
  Dunit = g/cm3
  Dvalue = 0.000756182
  Group = -> [H_element111,O_element104]
  conduct = 2
  density = 1
  expand = 3
  formula = G4_WATER_VAPOR
  name = G4_WATER_VAPOR
  specific = 4
FEATURE [App::DocumentObjectGroupPython] C_element122  label="C_element : 068"  # scripted group (container) (typed FeaturePython)
  n = 8
  ref = C_element
FEATURE [App::DocumentObjectGroupPython] H_element112  label="H_element : 061"  # scripted group (container) (typed FeaturePython)
  n = 10
  ref = H_element
FEATURE [App::DocumentObjectGroupPython] G4_XYLENE  # scripted group (container) (typed FeaturePython)
  Dunit = g/cm3
  Dvalue = 0.87
  Group = -> [C_element122,H_element112]
  conduct = 2
  density = 1
  expand = 3
  formula = G4_XYLENE
  name = G4_XYLENE
  specific = 4
FEATURE [App::DocumentObjectGroupPython] C_element123  label="C_element : 069"  # scripted group (container) (typed FeaturePython)
  n = 1
  ref = C_element
FEATURE [App::DocumentObjectGroupPython] G4_GRAPHITE  # scripted group (container) (typed FeaturePython)
  Dunit = g/cm3
  Dvalue = 2.21
  Group = -> [C_element123]
  conduct = 2
  density = 1
  expand = 3
  formula = G4_GRAPHITE
  name = G4_GRAPHITE
  specific = 4
FEATURE [App::DocumentObjectGroupPython] NIST  # scripted group (container) (typed FeaturePython)
  Group = -> [G4_A_150_TISSUE,G4_ACETONE,G4_ACETYLENE,G4_ADENINE,G4_ADIPOSE_TISSUE_ICRP,G4_AIR001,G4_ALANINE,G4_ALUMINUM_OXIDE,G4_AMBER,G4_AMMONIA,G4_ANILINE,G4_ANTHRACENE,G4_B_100_BONE,G4_BAKELITE,G4_BARIUM_FLUORIDE,G4_BARIUM_SULFATE,G4_BENZENE,G4_BERYLLIUM_OXIDE,G4_BGO,G4_BLOOD_ICRP,G4_BONE_COMPACT_ICRU,G4_BONE_CORTICAL_ICRP,G4_BORON_CARBIDE,G4_BORON_OXIDE,G4_BRAIN_ICRP,G4_BUTANE,G4_N_BUTYL_ALCOHOL,G4_C_552,+152 more]
FEATURE [App::DocumentObjectGroupPython] H_element113  label="H_element : 062"  # scripted group (container) (typed FeaturePython)
  n = 1
  ref = H_element
FEATURE [App::DocumentObjectGroupPython] G4_H  # scripted group (container) (typed FeaturePython)
  Dunit = g/cm3
  Dvalue = 8.3748e-05
  Group = -> [H_element113]
  conduct = 2
  density = 1
  expand = 3
  formula = H
  name = G4_H
  specific = 4
FEATURE [App::DocumentObjectGroupPython] He_element001  label="He_element : 1"  # scripted group (container) (typed FeaturePython)
  n = 1
  ref = He_element
FEATURE [App::DocumentObjectGroupPython] G4_He  # scripted group (container) (typed FeaturePython)
  Dunit = g/cm3
  Dvalue = 0.000166322
  Group = -> [He_element001]
  conduct = 2
  density = 1
  expand = 3
  formula = He
  name = G4_He
  specific = 4
FEATURE [App::DocumentObjectGroupPython] Li_element008  label="Li_element : 008"  # scripted group (container) (typed FeaturePython)
  n = 1
  ref = Li_element
FEATURE [App::DocumentObjectGroupPython] G4_Li  # scripted group (container) (typed FeaturePython)
  Dunit = g/cm3
  Dvalue = 0.534
  Group = -> [Li_element008]
  conduct = 2
  density = 1
  expand = 3
  formula = Li
  name = G4_Li
  specific = 4
FEATURE [App::DocumentObjectGroupPython] Be_element002  label="Be_element : 002"  # scripted group (container) (typed FeaturePython)
  n = 1
  ref = Be_element
FEATURE [App::DocumentObjectGroupPython] G4_Be  # scripted group (container) (typed FeaturePython)
  Dunit = g/cm3
  Dvalue = 1.848
  Group = -> [Be_element002]
  conduct = 2
  density = 1
  expand = 3
  formula = Be
  name = G4_Be
  specific = 4
FEATURE [App::DocumentObjectGroupPython] B_element007  label="B_element : 007"  # scripted group (container) (typed FeaturePython)
  n = 1
  ref = B_element
FEATURE [App::DocumentObjectGroupPython] G4_B  # scripted group (container) (typed FeaturePython)
  Dunit = g/cm3
  Dvalue = 2.37
  Group = -> [B_element007]
  conduct = 2
  density = 1
  expand = 3
  formula = B
  name = G4_B
  specific = 4
FEATURE [App::DocumentObjectGroupPython] C_element124  label="C_element : 070"  # scripted group (container) (typed FeaturePython)
  n = 1
  ref = C_element
FEATURE [App::DocumentObjectGroupPython] G4_C  # scripted group (container) (typed FeaturePython)
  Dunit = g/cm3
  Dvalue = 2
  Group = -> [C_element124]
  conduct = 2
  density = 1
  expand = 3
  formula = C
  name = G4_C
  specific = 4
FEATURE [App::DocumentObjectGroupPython] N_element048  label="N_element : 021"  # scripted group (container) (typed FeaturePython)
  n = 1
  ref = N_element
FEATURE [App::DocumentObjectGroupPython] G4_N  # scripted group (container) (typed FeaturePython)
  Dunit = g/cm3
  Dvalue = 0.0011652
  Group = -> [N_element048]
  conduct = 2
  density = 1
  expand = 3
  formula = N
  name = G4_N
  specific = 4
FEATURE [App::DocumentObjectGroupPython] O_element105  label="O_element : 059"  # scripted group (container) (typed FeaturePython)
  n = 1
  ref = O_element
FEATURE [App::DocumentObjectGroupPython] G4_O  # scripted group (container) (typed FeaturePython)
  Dunit = g/cm3
  Dvalue = 0.00133151
  Group = -> [O_element105]
  conduct = 2
  density = 1
  expand = 3
  formula = O
  name = G4_O
  specific = 4
FEATURE [App::DocumentObjectGroupPython] F_element019  label="F_element : 008"  # scripted group (container) (typed FeaturePython)
  n = 1
  ref = F_element
FEATURE [App::DocumentObjectGroupPython] G4_F  # scripted group (container) (typed FeaturePython)
  Dunit = g/cm3
  Dvalue = 0.00158029
  Group = -> [F_element019]
  conduct = 2
  density = 1
  expand = 3
  formula = F
  name = G4_F
  specific = 4
FEATURE [App::DocumentObjectGroupPython] Ne_element001  label="Ne_element : 1"  # scripted group (container) (typed FeaturePython)
  n = 1
  ref = Ne_element
FEATURE [App::DocumentObjectGroupPython] G4_Ne  # scripted group (container) (typed FeaturePython)
  Dunit = g/cm3
  Dvalue = 0.000838505
  Group = -> [Ne_element001]
  conduct = 2
  density = 1
  expand = 3
  formula = Ne
  name = G4_Ne
  specific = 4
FEATURE [App::DocumentObjectGroupPython] Na_element020  label="Na_element : 005"  # scripted group (container) (typed FeaturePython)
  n = 1
  ref = Na_element
FEATURE [App::DocumentObjectGroupPython] G4_Na  # scripted group (container) (typed FeaturePython)
  Dunit = g/cm3
  Dvalue = 0.971
  Group = -> [Na_element020]
  conduct = 2
  density = 1
  expand = 3
  formula = Na
  name = G4_Na
  specific = 4
FEATURE [App::DocumentObjectGroupPython] Mg_element011  label="Mg_element : 005"  # scripted group (container) (typed FeaturePython)
  n = 1
  ref = Mg_element
FEATURE [App::DocumentObjectGroupPython] G4_Mg  # scripted group (container) (typed FeaturePython)
  Dunit = g/cm3
  Dvalue = 1.74
  Group = -> [Mg_element011]
  conduct = 2
  density = 1
  expand = 3
  formula = Mg
  name = G4_Mg
  specific = 4
FEATURE [App::DocumentObjectGroupPython] Al_element004  label="Al_element : 1"  # scripted group (container) (typed FeaturePython)
  n = 1
  ref = Al_element
FEATURE [App::DocumentObjectGroupPython] G4_Al  # scripted group (container) (typed FeaturePython)
  Dunit = g/cm3
  Dvalue = 2.699
  Group = -> [Al_element004]
  conduct = 2
  density = 1
  expand = 3
  formula = Al
  name = G4_Al
  specific = 4
FEATURE [App::DocumentObjectGroupPython] Si_element007  label="Si_element : 002"  # scripted group (container) (typed FeaturePython)
  n = 1
  ref = Si_element
FEATURE [App::DocumentObjectGroupPython] G4_Si  # scripted group (container) (typed FeaturePython)
  Dunit = g/cm3
  Dvalue = 2.33
  Group = -> [Si_element007]
  conduct = 2
  density = 1
  expand = 3
  formula = Si
  name = G4_Si
  specific = 4
FEATURE [App::DocumentObjectGroupPython] P_element013  label="P_element : 002"  # scripted group (container) (typed FeaturePython)
  n = 1
  ref = P_element
FEATURE [App::DocumentObjectGroupPython] G4_P  # scripted group (container) (typed FeaturePython)
  Dunit = g/cm3
  Dvalue = 2.2
  Group = -> [P_element013]
  conduct = 2
  density = 1
  expand = 3
  formula = P
  name = G4_P
  specific = 4
FEATURE [App::DocumentObjectGroupPython] S_element023  label="S_element : 007"  # scripted group (container) (typed FeaturePython)
  n = 1
  ref = S_element
FEATURE [App::DocumentObjectGroupPython] G4_S  # scripted group (container) (typed FeaturePython)
  Dunit = g/cm3
  Dvalue = 2
  Group = -> [S_element023]
  conduct = 2
  density = 1
  expand = 3
  formula = S
  name = G4_S
  specific = 4
FEATURE [App::DocumentObjectGroupPython] Cl_element029  label="Cl_element : 015"  # scripted group (container) (typed FeaturePython)
  n = 1
  ref = Cl_element
FEATURE [App::DocumentObjectGroupPython] G4_Cl  # scripted group (container) (typed FeaturePython)
  Dunit = g/cm3
  Dvalue = 0.00299473
  Group = -> [Cl_element029]
  conduct = 2
  density = 1
  expand = 3
  formula = Cl
  name = G4_Cl
  specific = 4
FEATURE [App::DocumentObjectGroupPython] Ar_element002  label="Ar_element : 1"  # scripted group (container) (typed FeaturePython)
  n = 1
  ref = Ar_element
FEATURE [App::DocumentObjectGroupPython] G4_Ar  # scripted group (container) (typed FeaturePython)
  Dunit = g/cm3
  Dvalue = 0.00166201
  Group = -> [Ar_element002]
  conduct = 2
  density = 1
  expand = 3
  formula = Ar
  name = G4_Ar
  specific = 4
FEATURE [App::DocumentObjectGroupPython] K_element013  label="K_element : 003"  # scripted group (container) (typed FeaturePython)
  n = 1
  ref = K_element
FEATURE [App::DocumentObjectGroupPython] G4_K  # scripted group (container) (typed FeaturePython)
  Dunit = g/cm3
  Dvalue = 0.862
  Group = -> [K_element013]
  conduct = 2
  density = 1
  expand = 3
  formula = K
  name = G4_K
  specific = 4
FEATURE [App::DocumentObjectGroupPython] Ca_element014  label="Ca_element : 007"  # scripted group (container) (typed FeaturePython)
  n = 1
  ref = Ca_element
FEATURE [App::DocumentObjectGroupPython] G4_Ca  # scripted group (container) (typed FeaturePython)
  Dunit = g/cm3
  Dvalue = 1.55
  Group = -> [Ca_element014]
  conduct = 2
  density = 1
  expand = 3
  formula = Ca
  name = G4_Ca
  specific = 4
FEATURE [App::DocumentObjectGroupPython] Sc_element001  label="Sc_element : 1"  # scripted group (container) (typed FeaturePython)
  n = 1
  ref = Sc_element
FEATURE [App::DocumentObjectGroupPython] G4_Sc  # scripted group (container) (typed FeaturePython)
  Dunit = g/cm3
  Dvalue = 2.989
  Group = -> [Sc_element001]
  conduct = 2
  density = 1
  expand = 3
  formula = Sc
  name = G4_Sc
  specific = 4
FEATURE [App::DocumentObjectGroupPython] Ti_element004  label="Ti_element : 002"  # scripted group (container) (typed FeaturePython)
  n = 1
  ref = Ti_element
FEATURE [App::DocumentObjectGroupPython] G4_Ti  # scripted group (container) (typed FeaturePython)
  Dunit = g/cm3
  Dvalue = 4.54
  Group = -> [Ti_element004]
  conduct = 2
  density = 1
  expand = 3
  formula = Ti
  name = G4_Ti
  specific = 4
FEATURE [App::DocumentObjectGroupPython] V_element001  label="V_element : 1"  # scripted group (container) (typed FeaturePython)
  n = 1
  ref = V_element
FEATURE [App::DocumentObjectGroupPython] G4_V  # scripted group (container) (typed FeaturePython)
  Dunit = g/cm3
  Dvalue = 6.11
  Group = -> [V_element001]
  conduct = 2
  density = 1
  expand = 3
  formula = V
  name = G4_V
  specific = 4
FEATURE [App::DocumentObjectGroupPython] Cr_element001  label="Cr_element : 1"  # scripted group (container) (typed FeaturePython)
  n = 1
  ref = Cr_element
FEATURE [App::DocumentObjectGroupPython] G4_Cr  # scripted group (container) (typed FeaturePython)
  Dunit = g/cm3
  Dvalue = 7.18
  Group = -> [Cr_element001]
  conduct = 2
  density = 1
  expand = 3
  formula = Cr
  name = G4_Cr
  specific = 4
FEATURE [App::DocumentObjectGroupPython] Mn_element001  label="Mn_element : 1"  # scripted group (container) (typed FeaturePython)
  n = 1
  ref = Mn_element
FEATURE [App::DocumentObjectGroupPython] G4_Mn  # scripted group (container) (typed FeaturePython)
  Dunit = g/cm3
  Dvalue = 7.44
  Group = -> [Mn_element001]
  conduct = 2
  density = 1
  expand = 3
  formula = Mn
  name = G4_Mn
  specific = 4
FEATURE [App::DocumentObjectGroupPython] Fe_element007  label="Fe_element : 004"  # scripted group (container) (typed FeaturePython)
  n = 1
  ref = Fe_element
FEATURE [App::DocumentObjectGroupPython] G4_Fe  # scripted group (container) (typed FeaturePython)
  Dunit = g/cm3
  Dvalue = 7.874
  Group = -> [Fe_element007]
  conduct = 2
  density = 1
  expand = 3
  formula = Fe
  name = G4_Fe
  specific = 4
FEATURE [App::DocumentObjectGroupPython] Co_element001  label="Co_element : 1"  # scripted group (container) (typed FeaturePython)
  n = 1
  ref = Co_element
FEATURE [App::DocumentObjectGroupPython] G4_Co  # scripted group (container) (typed FeaturePython)
  Dunit = g/cm3
  Dvalue = 8.9
  Group = -> [Co_element001]
  conduct = 2
  density = 1
  expand = 3
  formula = Co
  name = G4_Co
  specific = 4
FEATURE [App::DocumentObjectGroupPython] Ni_element001  label="Ni_element : 1"  # scripted group (container) (typed FeaturePython)
  n = 1
  ref = Ni_element
FEATURE [App::DocumentObjectGroupPython] G4_Ni  # scripted group (container) (typed FeaturePython)
  Dunit = g/cm3
  Dvalue = 8.902
  Group = -> [Ni_element001]
  conduct = 2
  density = 1
  expand = 3
  formula = Ni
  name = G4_Ni
  specific = 4
FEATURE [App::DocumentObjectGroupPython] Cu_element001  label="Cu_element : 1"  # scripted group (container) (typed FeaturePython)
  n = 1
  ref = Cu_element
FEATURE [App::DocumentObjectGroupPython] G4_Cu  # scripted group (container) (typed FeaturePython)
  Dunit = g/cm3
  Dvalue = 8.96
  Group = -> [Cu_element001]
  conduct = 2
  density = 1
  expand = 3
  formula = Cu
  name = G4_Cu
  specific = 4
FEATURE [App::DocumentObjectGroupPython] Zn_element001  label="Zn_element : 1"  # scripted group (container) (typed FeaturePython)
  n = 1
  ref = Zn_element
FEATURE [App::DocumentObjectGroupPython] G4_Zn  # scripted group (container) (typed FeaturePython)
  Dunit = g/cm3
  Dvalue = 7.133
  Group = -> [Zn_element001]
  conduct = 2
  density = 1
  expand = 3
  formula = Zn
  name = G4_Zn
  specific = 4
FEATURE [App::DocumentObjectGroupPython] Ga_element002  label="Ga_element : 002"  # scripted group (container) (typed FeaturePython)
  n = 1
  ref = Ga_element
FEATURE [App::DocumentObjectGroupPython] G4_Ga  # scripted group (container) (typed FeaturePython)
  Dunit = g/cm3
  Dvalue = 5.904
  Group = -> [Ga_element002]
  conduct = 2
  density = 1
  expand = 3
  formula = Ga
  name = G4_Ga
  specific = 4
FEATURE [App::DocumentObjectGroupPython] Ge_element002  label="Ge_element : 1"  # scripted group (container) (typed FeaturePython)
  n = 1
  ref = Ge_element
FEATURE [App::DocumentObjectGroupPython] G4_Ge  # scripted group (container) (typed FeaturePython)
  Dunit = g/cm3
  Dvalue = 5.323
  Group = -> [Ge_element002]
  conduct = 2
  density = 1
  expand = 3
  formula = Ge
  name = G4_Ge
  specific = 4
FEATURE [App::DocumentObjectGroupPython] As_element003  label="As_element : 002"  # scripted group (container) (typed FeaturePython)
  n = 1
  ref = As_element
FEATURE [App::DocumentObjectGroupPython] G4_As  # scripted group (container) (typed FeaturePython)
  Dunit = g/cm3
  Dvalue = 5.73
  Group = -> [As_element003]
  conduct = 2
  density = 1
  expand = 3
  formula = As
  name = G4_As
  specific = 4
FEATURE [App::DocumentObjectGroupPython] Se_element001  label="Se_element : 1"  # scripted group (container) (typed FeaturePython)
  n = 1
  ref = Se_element
FEATURE [App::DocumentObjectGroupPython] G4_Se  # scripted group (container) (typed FeaturePython)
  Dunit = g/cm3
  Dvalue = 4.5
  Group = -> [Se_element001]
  conduct = 2
  density = 1
  expand = 3
  formula = Se
  name = G4_Se
  specific = 4
FEATURE [App::DocumentObjectGroupPython] Br_element007  label="Br_element : 004"  # scripted group (container) (typed FeaturePython)
  n = 1
  ref = Br_element
FEATURE [App::DocumentObjectGroupPython] G4_Br  # scripted group (container) (typed FeaturePython)
  Dunit = g/cm3
  Dvalue = 0.0070721
  Group = -> [Br_element007]
  conduct = 2
  density = 1
  expand = 3
  formula = Br
  name = G4_Br
  specific = 4
FEATURE [App::DocumentObjectGroupPython] Kr_element001  label="Kr_element : 1"  # scripted group (container) (typed FeaturePython)
  n = 1
  ref = Kr_element
FEATURE [App::DocumentObjectGroupPython] G4_Kr  # scripted group (container) (typed FeaturePython)
  Dunit = g/cm3
  Dvalue = 0.00347832
  Group = -> [Kr_element001]
  conduct = 2
  density = 1
  expand = 3
  formula = Kr
  name = G4_Kr
  specific = 4
FEATURE [App::DocumentObjectGroupPython] Rb_element001  label="Rb_element : 1"  # scripted group (container) (typed FeaturePython)
  n = 1
  ref = Rb_element
FEATURE [App::DocumentObjectGroupPython] G4_Rb  # scripted group (container) (typed FeaturePython)
  Dunit = g/cm3
  Dvalue = 1.532
  Group = -> [Rb_element001]
  conduct = 2
  density = 1
  expand = 3
  formula = Rb
  name = G4_Rb
  specific = 4
FEATURE [App::DocumentObjectGroupPython] Sr_element001  label="Sr_element : 1"  # scripted group (container) (typed FeaturePython)
  n = 1
  ref = Sr_element
FEATURE [App::DocumentObjectGroupPython] G4_Sr  # scripted group (container) (typed FeaturePython)
  Dunit = g/cm3
  Dvalue = 2.54
  Group = -> [Sr_element001]
  conduct = 2
  density = 1
  expand = 3
  formula = Sr
  name = G4_Sr
  specific = 4
FEATURE [App::DocumentObjectGroupPython] Y_element001  label="Y_element : 1"  # scripted group (container) (typed FeaturePython)
  n = 1
  ref = Y_element
FEATURE [App::DocumentObjectGroupPython] G4_Y  # scripted group (container) (typed FeaturePython)
  Dunit = g/cm3
  Dvalue = 4.469
  Group = -> [Y_element001]
  conduct = 2
  density = 1
  expand = 3
  formula = Y
  name = G4_Y
  specific = 4
FEATURE [App::DocumentObjectGroupPython] Zr_element001  label="Zr_element : 1"  # scripted group (container) (typed FeaturePython)
  n = 1
  ref = Zr_element
FEATURE [App::DocumentObjectGroupPython] G4_Zr  # scripted group (container) (typed FeaturePython)
  Dunit = g/cm3
  Dvalue = 6.506
  Group = -> [Zr_element001]
  conduct = 2
  density = 1
  expand = 3
  formula = Zr
  name = G4_Zr
  specific = 4
FEATURE [App::DocumentObjectGroupPython] Nb_element001  label="Nb_element : 1"  # scripted group (container) (typed FeaturePython)
  n = 1
  ref = Nb_element
FEATURE [App::DocumentObjectGroupPython] G4_Nb  # scripted group (container) (typed FeaturePython)
  Dunit = g/cm3
  Dvalue = 8.57
  Group = -> [Nb_element001]
  conduct = 2
  density = 1
  expand = 3
  formula = Nb
  name = G4_Nb
  specific = 4
FEATURE [App::DocumentObjectGroupPython] Mo_element001  label="Mo_element : 1"  # scripted group (container) (typed FeaturePython)
  n = 1
  ref = Mo_element
FEATURE [App::DocumentObjectGroupPython] G4_Mo  # scripted group (container) (typed FeaturePython)
  Dunit = g/cm3
  Dvalue = 10.22
  Group = -> [Mo_element001]
  conduct = 2
  density = 1
  expand = 3
  formula = Mo
  name = G4_Mo
  specific = 4
FEATURE [App::DocumentObjectGroupPython] Tc_element001  label="Tc_element : 1"  # scripted group (container) (typed FeaturePython)
  n = 1
  ref = Tc_element
FEATURE [App::DocumentObjectGroupPython] G4_Tc  # scripted group (container) (typed FeaturePython)
  Dunit = g/cm3
  Dvalue = 11.5
  Group = -> [Tc_element001]
  conduct = 2
  density = 1
  expand = 3
  formula = Tc
  name = G4_Tc
  specific = 4
FEATURE [App::DocumentObjectGroupPython] Ru_element001  label="Ru_element : 1"  # scripted group (container) (typed FeaturePython)
  n = 1
  ref = Ru_element
FEATURE [App::DocumentObjectGroupPython] G4_Ru  # scripted group (container) (typed FeaturePython)
  Dunit = g/cm3
  Dvalue = 12.41
  Group = -> [Ru_element001]
  conduct = 2
  density = 1
  expand = 3
  formula = Ru
  name = G4_Ru
  specific = 4
FEATURE [App::DocumentObjectGroupPython] Rh_element001  label="Rh_element : 1"  # scripted group (container) (typed FeaturePython)
  n = 1
  ref = Rh_element
FEATURE [App::DocumentObjectGroupPython] G4_Rh  # scripted group (container) (typed FeaturePython)
  Dunit = g/cm3
  Dvalue = 12.41
  Group = -> [Rh_element001]
  conduct = 2
  density = 1
  expand = 3
  formula = Rh
  name = G4_Rh
  specific = 4
FEATURE [App::DocumentObjectGroupPython] Pd_element001  label="Pd_element : 1"  # scripted group (container) (typed FeaturePython)
  n = 1
  ref = Pd_element
FEATURE [App::DocumentObjectGroupPython] G4_Pd  # scripted group (container) (typed FeaturePython)
  Dunit = g/cm3
  Dvalue = 12.02
  Group = -> [Pd_element001]
  conduct = 2
  density = 1
  expand = 3
  formula = Pd
  name = G4_Pd
  specific = 4
FEATURE [App::DocumentObjectGroupPython] Ag_element006  label="Ag_element : 004"  # scripted group (container) (typed FeaturePython)
  n = 1
  ref = Ag_element
FEATURE [App::DocumentObjectGroupPython] G4_Ag  # scripted group (container) (typed FeaturePython)
  Dunit = g/cm3
  Dvalue = 10.5
  Group = -> [Ag_element006]
  conduct = 2
  density = 1
  expand = 3
  formula = Ag
  name = G4_Ag
  specific = 4
FEATURE [App::DocumentObjectGroupPython] Cd_element003  label="Cd_element : 003"  # scripted group (container) (typed FeaturePython)
  n = 1
  ref = Cd_element
FEATURE [App::DocumentObjectGroupPython] G4_Cd  # scripted group (container) (typed FeaturePython)
  Dunit = g/cm3
  Dvalue = 8.65
  Group = -> [Cd_element003]
  conduct = 2
  density = 1
  expand = 3
  formula = Cd
  name = G4_Cd
  specific = 4
FEATURE [App::DocumentObjectGroupPython] In_element001  label="In_element : 1"  # scripted group (container) (typed FeaturePython)
  n = 1
  ref = In_element
FEATURE [App::DocumentObjectGroupPython] G4_In  # scripted group (container) (typed FeaturePython)
  Dunit = g/cm3
  Dvalue = 7.31
  Group = -> [In_element001]
  conduct = 2
  density = 1
  expand = 3
  formula = In
  name = G4_In
  specific = 4
FEATURE [App::DocumentObjectGroupPython] Sn_element001  label="Sn_element : 1"  # scripted group (container) (typed FeaturePython)
  n = 1
  ref = Sn_element
FEATURE [App::DocumentObjectGroupPython] G4_Sn  # scripted group (container) (typed FeaturePython)
  Dunit = g/cm3
  Dvalue = 7.31
  Group = -> [Sn_element001]
  conduct = 2
  density = 1
  expand = 3
  formula = Sn
  name = G4_Sn
  specific = 4
FEATURE [App::DocumentObjectGroupPython] Sb_element001  label="Sb_element : 1"  # scripted group (container) (typed FeaturePython)
  n = 1
  ref = Sb_element
FEATURE [App::DocumentObjectGroupPython] G4_Sb  # scripted group (container) (typed FeaturePython)
  Dunit = g/cm3
  Dvalue = 6.691
  Group = -> [Sb_element001]
  conduct = 2
  density = 1
  expand = 3
  formula = Sb
  name = G4_Sb
  specific = 4
FEATURE [App::DocumentObjectGroupPython] Te_element002  label="Te_element : 002"  # scripted group (container) (typed FeaturePython)
  n = 1
  ref = Te_element
FEATURE [App::DocumentObjectGroupPython] G4_Te  # scripted group (container) (typed FeaturePython)
  Dunit = g/cm3
  Dvalue = 6.24
  Group = -> [Te_element002]
  conduct = 2
  density = 1
  expand = 3
  formula = Te
  name = G4_Te
  specific = 4
FEATURE [App::DocumentObjectGroupPython] I_element010  label="I_element : 006"  # scripted group (container) (typed FeaturePython)
  n = 1
  ref = I_element
FEATURE [App::DocumentObjectGroupPython] G4_I  # scripted group (container) (typed FeaturePython)
  Dunit = g/cm3
  Dvalue = 4.93
  Group = -> [I_element010]
  conduct = 2
  density = 1
  expand = 3
  formula = I
  name = G4_I
  specific = 4
FEATURE [App::DocumentObjectGroupPython] Xe_element001  label="Xe_element : 1"  # scripted group (container) (typed FeaturePython)
  n = 1
  ref = Xe_element
FEATURE [App::DocumentObjectGroupPython] G4_Xe  # scripted group (container) (typed FeaturePython)
  Dunit = g/cm3
  Dvalue = 0.00548536
  Group = -> [Xe_element001]
  conduct = 2
  density = 1
  expand = 3
  formula = Xe
  name = G4_Xe
  specific = 4
FEATURE [App::DocumentObjectGroupPython] Cs_element003  label="Cs_element : 003"  # scripted group (container) (typed FeaturePython)
  n = 1
  ref = Cs_element
FEATURE [App::DocumentObjectGroupPython] G4_Cs  # scripted group (container) (typed FeaturePython)
  Dunit = g/cm3
  Dvalue = 1.873
  Group = -> [Cs_element003]
  conduct = 2
  density = 1
  expand = 3
  formula = Cs
  name = G4_Cs
  specific = 4
FEATURE [App::DocumentObjectGroupPython] Ba_element003  label="Ba_element : 003"  # scripted group (container) (typed FeaturePython)
  n = 1
  ref = Ba_element
FEATURE [App::DocumentObjectGroupPython] G4_Ba  # scripted group (container) (typed FeaturePython)
  Dunit = g/cm3
  Dvalue = 3.5
  Group = -> [Ba_element003]
  conduct = 2
  density = 1
  expand = 3
  formula = Ba
  name = G4_Ba
  specific = 4
FEATURE [App::DocumentObjectGroupPython] La_element003  label="La_element : 003"  # scripted group (container) (typed FeaturePython)
  n = 1
  ref = La_element
FEATURE [App::DocumentObjectGroupPython] G4_La  # scripted group (container) (typed FeaturePython)
  Dunit = g/cm3
  Dvalue = 6.154
  Group = -> [La_element003]
  conduct = 2
  density = 1
  expand = 3
  formula = La
  name = G4_La
  specific = 4
FEATURE [App::DocumentObjectGroupPython] Ce_element002  label="Ce_element : 1"  # scripted group (container) (typed FeaturePython)
  n = 1
  ref = Ce_element
FEATURE [App::DocumentObjectGroupPython] G4_Ce  # scripted group (container) (typed FeaturePython)
  Dunit = g/cm3
  Dvalue = 6.657
  Group = -> [Ce_element002]
  conduct = 2
  density = 1
  expand = 3
  formula = Ce
  name = G4_Ce
  specific = 4
FEATURE [App::DocumentObjectGroupPython] Pr_element001  label="Pr_element : 1"  # scripted group (container) (typed FeaturePython)
  n = 1
  ref = Pr_element
FEATURE [App::DocumentObjectGroupPython] G4_Pr  # scripted group (container) (typed FeaturePython)
  Dunit = g/cm3
  Dvalue = 6.71
  Group = -> [Pr_element001]
  conduct = 2
  density = 1
  expand = 3
  formula = Pr
  name = G4_Pr
  specific = 4
FEATURE [App::DocumentObjectGroupPython] Nd_element001  label="Nd_element : 1"  # scripted group (container) (typed FeaturePython)
  n = 1
  ref = Nd_element
FEATURE [App::DocumentObjectGroupPython] G4_Nd  # scripted group (container) (typed FeaturePython)
  Dunit = g/cm3
  Dvalue = 6.9
  Group = -> [Nd_element001]
  conduct = 2
  density = 1
  expand = 3
  formula = Nd
  name = G4_Nd
  specific = 4
FEATURE [App::DocumentObjectGroupPython] Pm_element001  label="Pm_element : 1"  # scripted group (container) (typed FeaturePython)
  n = 1
  ref = Pm_element
FEATURE [App::DocumentObjectGroupPython] G4_Pm  # scripted group (container) (typed FeaturePython)
  Dunit = g/cm3
  Dvalue = 7.22
  Group = -> [Pm_element001]
  conduct = 2
  density = 1
  expand = 3
  formula = Pm
  name = G4_Pm
  specific = 4
FEATURE [App::DocumentObjectGroupPython] Sm_element001  label="Sm_element : 1"  # scripted group (container) (typed FeaturePython)
  n = 1
  ref = Sm_element
FEATURE [App::DocumentObjectGroupPython] G4_Sm  # scripted group (container) (typed FeaturePython)
  Dunit = g/cm3
  Dvalue = 7.46
  Group = -> [Sm_element001]
  conduct = 2
  density = 1
  expand = 3
  formula = Sm
  name = G4_Sm
  specific = 4
FEATURE [App::DocumentObjectGroupPython] Eu_element001  label="Eu_element : 1"  # scripted group (container) (typed FeaturePython)
  n = 1
  ref = Eu_element
FEATURE [App::DocumentObjectGroupPython] G4_Eu  # scripted group (container) (typed FeaturePython)
  Dunit = g/cm3
  Dvalue = 5.243
  Group = -> [Eu_element001]
  conduct = 2
  density = 1
  expand = 3
  formula = Eu
  name = G4_Eu
  specific = 4
FEATURE [App::DocumentObjectGroupPython] Gd_element002  label="Gd_element : 1"  # scripted group (container) (typed FeaturePython)
  n = 1
  ref = Gd_element
FEATURE [App::DocumentObjectGroupPython] G4_Gd  # scripted group (container) (typed FeaturePython)
  Dunit = g/cm3
  Dvalue = 7.9004
  Group = -> [Gd_element002]
  conduct = 2
  density = 1
  expand = 3
  formula = Gd
  name = G4_Gd
  specific = 4
FEATURE [App::DocumentObjectGroupPython] Tb_element001  label="Tb_element : 1"  # scripted group (container) (typed FeaturePython)
  n = 1
  ref = Tb_element
FEATURE [App::DocumentObjectGroupPython] G4_Tb  # scripted group (container) (typed FeaturePython)
  Dunit = g/cm3
  Dvalue = 8.229
  Group = -> [Tb_element001]
  conduct = 2
  density = 1
  expand = 3
  formula = Tb
  name = G4_Tb
  specific = 4
FEATURE [App::DocumentObjectGroupPython] Dy_element001  label="Dy_element : 1"  # scripted group (container) (typed FeaturePython)
  n = 1
  ref = Dy_element
FEATURE [App::DocumentObjectGroupPython] G4_Dy  # scripted group (container) (typed FeaturePython)
  Dunit = g/cm3
  Dvalue = 8.55
  Group = -> [Dy_element001]
  conduct = 2
  density = 1
  expand = 3
  formula = Dy
  name = G4_Dy
  specific = 4
FEATURE [App::DocumentObjectGroupPython] Ho_element001  label="Ho_element : 1"  # scripted group (container) (typed FeaturePython)
  n = 1
  ref = Ho_element
FEATURE [App::DocumentObjectGroupPython] G4_Ho  # scripted group (container) (typed FeaturePython)
  Dunit = g/cm3
  Dvalue = 8.795
  Group = -> [Ho_element001]
  conduct = 2
  density = 1
  expand = 3
  formula = Ho
  name = G4_Ho
  specific = 4
FEATURE [App::DocumentObjectGroupPython] Er_element001  label="Er_element : 1"  # scripted group (container) (typed FeaturePython)
  n = 1
  ref = Er_element
FEATURE [App::DocumentObjectGroupPython] G4_Er  # scripted group (container) (typed FeaturePython)
  Dunit = g/cm3
  Dvalue = 9.066
  Group = -> [Er_element001]
  conduct = 2
  density = 1
  expand = 3
  formula = Er
  name = G4_Er
  specific = 4
FEATURE [App::DocumentObjectGroupPython] Tm_element001  label="Tm_element : 1"  # scripted group (container) (typed FeaturePython)
  n = 1
  ref = Tm_element
FEATURE [App::DocumentObjectGroupPython] G4_Tm  # scripted group (container) (typed FeaturePython)
  Dunit = g/cm3
  Dvalue = 9.321
  Group = -> [Tm_element001]
  conduct = 2
  density = 1
  expand = 3
  formula = Tm
  name = G4_Tm
  specific = 4
FEATURE [App::DocumentObjectGroupPython] Yb_element001  label="Yb_element : 1"  # scripted group (container) (typed FeaturePython)
  n = 1
  ref = Yb_element
FEATURE [App::DocumentObjectGroupPython] G4_Yb  # scripted group (container) (typed FeaturePython)
  Dunit = g/cm3
  Dvalue = 6.73
  Group = -> [Yb_element001]
  conduct = 2
  density = 1
  expand = 3
  formula = Yb
  name = G4_Yb
  specific = 4
FEATURE [App::DocumentObjectGroupPython] Lu_element001  label="Lu_element : 1"  # scripted group (container) (typed FeaturePython)
  n = 1
  ref = Lu_element
FEATURE [App::DocumentObjectGroupPython] G4_Lu  # scripted group (container) (typed FeaturePython)
  Dunit = g/cm3
  Dvalue = 9.84
  Group = -> [Lu_element001]
  conduct = 2
  density = 1
  expand = 3
  formula = Lu
  name = G4_Lu
  specific = 4
FEATURE [App::DocumentObjectGroupPython] Hf_element001  label="Hf_element : 1"  # scripted group (container) (typed FeaturePython)
  n = 1
  ref = Hf_element
FEATURE [App::DocumentObjectGroupPython] G4_Hf  # scripted group (container) (typed FeaturePython)
  Dunit = g/cm3
  Dvalue = 13.31
  Group = -> [Hf_element001]
  conduct = 2
  density = 1
  expand = 3
  formula = Hf
  name = G4_Hf
  specific = 4
FEATURE [App::DocumentObjectGroupPython] Ta_element001  label="Ta_element : 1"  # scripted group (container) (typed FeaturePython)
  n = 1
  ref = Ta_element
FEATURE [App::DocumentObjectGroupPython] G4_Ta  # scripted group (container) (typed FeaturePython)
  Dunit = g/cm3
  Dvalue = 16.654
  Group = -> [Ta_element001]
  conduct = 2
  density = 1
  expand = 3
  formula = Ta
  name = G4_Ta
  specific = 4
FEATURE [App::DocumentObjectGroupPython] W_element004  label="W_element : 004"  # scripted group (container) (typed FeaturePython)
  n = 1
  ref = W_element
FEATURE [App::DocumentObjectGroupPython] G4_W  # scripted group (container) (typed FeaturePython)
  Dunit = g/cm3
  Dvalue = 19.3
  Group = -> [W_element004]
  conduct = 2
  density = 1
  expand = 3
  formula = W
  name = G4_W
  specific = 4
FEATURE [App::DocumentObjectGroupPython] Re_element001  label="Re_element : 1"  # scripted group (container) (typed FeaturePython)
  n = 1
  ref = Re_element
FEATURE [App::DocumentObjectGroupPython] G4_Re  # scripted group (container) (typed FeaturePython)
  Dunit = g/cm3
  Dvalue = 21.02
  Group = -> [Re_element001]
  conduct = 2
  density = 1
  expand = 3
  formula = Re
  name = G4_Re
  specific = 4
FEATURE [App::DocumentObjectGroupPython] Os_element001  label="Os_element : 1"  # scripted group (container) (typed FeaturePython)
  n = 1
  ref = Os_element
FEATURE [App::DocumentObjectGroupPython] G4_Os  # scripted group (container) (typed FeaturePython)
  Dunit = g/cm3
  Dvalue = 22.57
  Group = -> [Os_element001]
  conduct = 2
  density = 1
  expand = 3
  formula = Os
  name = G4_Os
  specific = 4
FEATURE [App::DocumentObjectGroupPython] Ir_element001  label="Ir_element : 1"  # scripted group (container) (typed FeaturePython)
  n = 1
  ref = Ir_element
FEATURE [App::DocumentObjectGroupPython] G4_Ir  # scripted group (container) (typed FeaturePython)
  Dunit = g/cm3
  Dvalue = 22.42
  Group = -> [Ir_element001]
  conduct = 2
  density = 1
  expand = 3
  formula = Ir
  name = G4_Ir
  specific = 4
FEATURE [App::DocumentObjectGroupPython] Pt_element001  label="Pt_element : 1"  # scripted group (container) (typed FeaturePython)
  n = 1
  ref = Pt_element
FEATURE [App::DocumentObjectGroupPython] G4_Pt  # scripted group (container) (typed FeaturePython)
  Dunit = g/cm3
  Dvalue = 21.45
  Group = -> [Pt_element001]
  conduct = 2
  density = 1
  expand = 3
  formula = Pt
  name = G4_Pt
  specific = 4
FEATURE [App::DocumentObjectGroupPython] Au_element001  label="Au_element : 1"  # scripted group (container) (typed FeaturePython)
  n = 1
  ref = Au_element
FEATURE [App::DocumentObjectGroupPython] G4_Au  # scripted group (container) (typed FeaturePython)
  Dunit = g/cm3
  Dvalue = 19.32
  Group = -> [Au_element001]
  conduct = 2
  density = 1
  expand = 3
  formula = Au
  name = G4_Au
  specific = 4
FEATURE [App::DocumentObjectGroupPython] Hg_element002  label="Hg_element : 002"  # scripted group (container) (typed FeaturePython)
  n = 1
  ref = Hg_element
FEATURE [App::DocumentObjectGroupPython] G4_Hg  # scripted group (container) (typed FeaturePython)
  Dunit = g/cm3
  Dvalue = 13.546
  Group = -> [Hg_element002]
  conduct = 2
  density = 1
  expand = 3
  formula = Hg
  name = G4_Hg
  specific = 4
FEATURE [App::DocumentObjectGroupPython] Tl_element002  label="Tl_element : 002"  # scripted group (container) (typed FeaturePython)
  n = 1
  ref = Tl_element
FEATURE [App::DocumentObjectGroupPython] G4_Tl  # scripted group (container) (typed FeaturePython)
  Dunit = g/cm3
  Dvalue = 11.72
  Group = -> [Tl_element002]
  conduct = 2
  density = 1
  expand = 3
  formula = Tl
  name = G4_Tl
  specific = 4
FEATURE [App::DocumentObjectGroupPython] Pb_element003  label="Pb_element : 1"  # scripted group (container) (typed FeaturePython)
  n = 1
  ref = Pb_element
FEATURE [App::DocumentObjectGroupPython] G4_Pb  # scripted group (container) (typed FeaturePython)
  Dunit = g/cm3
  Dvalue = 11.35
  Group = -> [Pb_element003]
  conduct = 2
  density = 1
  expand = 3
  formula = Pb
  name = G4_Pb
  specific = 4
FEATURE [App::DocumentObjectGroupPython] Bi_element002  label="Bi_element : 1"  # scripted group (container) (typed FeaturePython)
  n = 1
  ref = Bi_element
FEATURE [App::DocumentObjectGroupPython] G4_Bi  # scripted group (container) (typed FeaturePython)
  Dunit = g/cm3
  Dvalue = 9.747
  Group = -> [Bi_element002]
  conduct = 2
  density = 1
  expand = 3
  formula = Bi
  name = G4_Bi
  specific = 4
FEATURE [App::DocumentObjectGroupPython] Po_element001  label="Po_element : 1"  # scripted group (container) (typed FeaturePython)
  n = 1
  ref = Po_element
FEATURE [App::DocumentObjectGroupPython] G4_Po  # scripted group (container) (typed FeaturePython)
  Dunit = g/cm3
  Dvalue = 9.32
  Group = -> [Po_element001]
  conduct = 2
  density = 1
  expand = 3
  formula = Po
  name = G4_Po
  specific = 4
FEATURE [App::DocumentObjectGroupPython] At_element001  label="At_element : 1"  # scripted group (container) (typed FeaturePython)
  n = 1
  ref = At_element
FEATURE [App::DocumentObjectGroupPython] G4_At  # scripted group (container) (typed FeaturePython)
  Dunit = g/cm3
  Dvalue = 9.32
  Group = -> [At_element001]
  conduct = 2
  density = 1
  expand = 3
  formula = At
  name = G4_At
  specific = 4
FEATURE [App::DocumentObjectGroupPython] Rn_element001  label="Rn_element : 1"  # scripted group (container) (typed FeaturePython)
  n = 1
  ref = Rn_element
FEATURE [App::DocumentObjectGroupPython] G4_Rn  # scripted group (container) (typed FeaturePython)
  Dunit = g/cm3
  Dvalue = 0.00900662
  Group = -> [Rn_element001]
  conduct = 2
  density = 1
  expand = 3
  formula = Rn
  name = G4_Rn
  specific = 4
FEATURE [App::DocumentObjectGroupPython] Fr_element001  label="Fr_element : 1"  # scripted group (container) (typed FeaturePython)
  n = 1
  ref = Fr_element
FEATURE [App::DocumentObjectGroupPython] G4_Fr  # scripted group (container) (typed FeaturePython)
  Dunit = g/cm3
  Dvalue = 1
  Group = -> [Fr_element001]
  conduct = 2
  density = 1
  expand = 3
  formula = Fr
  name = G4_Fr
  specific = 4
FEATURE [App::DocumentObjectGroupPython] Ra_element001  label="Ra_element : 1"  # scripted group (container) (typed FeaturePython)
  n = 1
  ref = Ra_element
FEATURE [App::DocumentObjectGroupPython] G4_Ra  # scripted group (container) (typed FeaturePython)
  Dunit = g/cm3
  Dvalue = 5
  Group = -> [Ra_element001]
  conduct = 2
  density = 1
  expand = 3
  formula = Ra
  name = G4_Ra
  specific = 4
FEATURE [App::DocumentObjectGroupPython] Ac_element001  label="Ac_element : 1"  # scripted group (container) (typed FeaturePython)
  n = 1
  ref = Ac_element
FEATURE [App::DocumentObjectGroupPython] G4_Ac  # scripted group (container) (typed FeaturePython)
  Dunit = g/cm3
  Dvalue = 10.07
  Group = -> [Ac_element001]
  conduct = 2
  density = 1
  expand = 3
  formula = Ac
  name = G4_Ac
  specific = 4
FEATURE [App::DocumentObjectGroupPython] Th_element001  label="Th_element : 1"  # scripted group (container) (typed FeaturePython)
  n = 1
  ref = Th_element
FEATURE [App::DocumentObjectGroupPython] G4_Th  # scripted group (container) (typed FeaturePython)
  Dunit = g/cm3
  Dvalue = 11.72
  Group = -> [Th_element001]
  conduct = 2
  density = 1
  expand = 3
  formula = Th
  name = G4_Th
  specific = 4
FEATURE [App::DocumentObjectGroupPython] Pa_element001  label="Pa_element : 1"  # scripted group (container) (typed FeaturePython)
  n = 1
  ref = Pa_element
FEATURE [App::DocumentObjectGroupPython] G4_Pa  # scripted group (container) (typed FeaturePython)
  Dunit = g/cm3
  Dvalue = 15.37
  Group = -> [Pa_element001]
  conduct = 2
  density = 1
  expand = 3
  formula = Pa
  name = G4_Pa
  specific = 4
FEATURE [App::DocumentObjectGroupPython] U_element004  label="U_element : 004"  # scripted group (container) (typed FeaturePython)
  n = 1
  ref = U_element
FEATURE [App::DocumentObjectGroupPython] G4_U  # scripted group (container) (typed FeaturePython)
  Dunit = g/cm3
  Dvalue = 18.95
  Group = -> [U_element004]
  conduct = 2
  density = 1
  expand = 3
  formula = U
  name = G4_U
  specific = 4
FEATURE [App::DocumentObjectGroupPython] Np_element001  label="Np_element : 1"  # scripted group (container) (typed FeaturePython)
  n = 1
  ref = Np_element
FEATURE [App::DocumentObjectGroupPython] G4_Np  # scripted group (container) (typed FeaturePython)
  Dunit = g/cm3
  Dvalue = 20.25
  Group = -> [Np_element001]
  conduct = 2
  density = 1
  expand = 3
  formula = Np
  name = G4_Np
  specific = 4
FEATURE [App::DocumentObjectGroupPython] Pu_element002  label="Pu_element : 002"  # scripted group (container) (typed FeaturePython)
  n = 1
  ref = Pu_element
FEATURE [App::DocumentObjectGroupPython] G4_Pu  # scripted group (container) (typed FeaturePython)
  Dunit = g/cm3
  Dvalue = 19.84
  Group = -> [Pu_element002]
  conduct = 2
  density = 1
  expand = 3
  formula = Pu
  name = G4_Pu
  specific = 4
FEATURE [App::DocumentObjectGroupPython] Am_element001  label="Am_element : 1"  # scripted group (container) (typed FeaturePython)
  n = 1
  ref = Am_element
FEATURE [App::DocumentObjectGroupPython] G4_Am  # scripted group (container) (typed FeaturePython)
  Dunit = g/cm3
  Dvalue = 13.67
  Group = -> [Am_element001]
  conduct = 2
  density = 1
  expand = 3
  formula = Am
  name = G4_Am
  specific = 4
FEATURE [App::DocumentObjectGroupPython] Cm_element001  label="Cm_element : 1"  # scripted group (container) (typed FeaturePython)
  n = 1
  ref = Cm_element
FEATURE [App::DocumentObjectGroupPython] G4_Cm  # scripted group (container) (typed FeaturePython)
  Dunit = g/cm3
  Dvalue = 13.51
  Group = -> [Cm_element001]
  conduct = 2
  density = 1
  expand = 3
  formula = Cm
  name = G4_Cm
  specific = 4
FEATURE [App::DocumentObjectGroupPython] Bk_element001  label="Bk_element : 1"  # scripted group (container) (typed FeaturePython)
  n = 1
  ref = Bk_element
FEATURE [App::DocumentObjectGroupPython] G4_Bk  # scripted group (container) (typed FeaturePython)
  Dunit = g/cm3
  Dvalue = 14
  Group = -> [Bk_element001]
  conduct = 2
  density = 1
  expand = 3
  formula = Bk
  name = G4_Bk
  specific = 4
FEATURE [App::DocumentObjectGroupPython] Cf_element001  label="Cf_element : 1"  # scripted group (container) (typed FeaturePython)
  n = 1
  ref = Cf_element
FEATURE [App::DocumentObjectGroupPython] G4_Cf  # scripted group (container) (typed FeaturePython)
  Dunit = g/cm3
  Dvalue = 10
  Group = -> [Cf_element001]
  conduct = 2
  density = 1
  expand = 3
  formula = Cf
  name = G4_Cf
  specific = 4
FEATURE [App::DocumentObjectGroupPython] Element  # scripted group (container) (typed FeaturePython)
  Group = -> [G4_H,G4_He,G4_Li,G4_Be,G4_B,G4_C,G4_N,G4_O,G4_F,G4_Ne,G4_Na,G4_Mg,G4_Al,G4_Si,G4_P,G4_S,G4_Cl,G4_Ar,G4_K,G4_Ca,G4_Sc,G4_Ti,G4_V,G4_Cr,G4_Mn,G4_Fe,G4_Co,G4_Ni,G4_Cu,G4_Zn,G4_Ga,G4_Ge,G4_As,G4_Se,G4_Br,G4_Kr,G4_Rb,G4_Sr,G4_Y,G4_Zr,G4_Nb,G4_Mo,G4_Tc,G4_Ru,G4_Rh,G4_Pd,G4_Ag,G4_Cd,G4_In,G4_Sn,G4_Sb,G4_Te,G4_I,G4_Xe,G4_Cs,G4_Ba,G4_La,G4_Ce,G4_Pr,G4_Nd,G4_Pm,G4_Sm,G4_Eu,G4_Gd,G4_Tb,G4_Dy,G4_Ho,G4_Er,+30 more]
FEATURE [App::DocumentObjectGroupPython] H_element114  label="H_element : 063"  # scripted group (container) (typed FeaturePython)
  n = 2
  ref = H_element
FEATURE [App::DocumentObjectGroupPython] G4_lH2  # scripted group (container) (typed FeaturePython)
  Dunit = g/cm3
  Dvalue = 0.0708
  Group = -> [H_element114]
  conduct = 2
  density = 1
  expand = 3
  formula = G4_lH2
  name = G4_lH2
  specific = 4
FEATURE [App::DocumentObjectGroupPython] N_element049  label="N_element : 022"  # scripted group (container) (typed FeaturePython)
  n = 2
  ref = N_element
FEATURE [App::DocumentObjectGroupPython] G4_lN2  # scripted group (container) (typed FeaturePython)
  Dunit = g/cm3
  Dvalue = 0.807
  Group = -> [N_element049]
  conduct = 2
  density = 1
  expand = 3
  formula = G4_lN2
  name = G4_lN2
  specific = 4
FEATURE [App::DocumentObjectGroupPython] O_element106  label="O_element : 060"  # scripted group (container) (typed FeaturePython)
  n = 2
  ref = O_element
FEATURE [App::DocumentObjectGroupPython] G4_lO2  # scripted group (container) (typed FeaturePython)
  Dunit = g/cm3
  Dvalue = 1.141
  Group = -> [O_element106]
  conduct = 2
  density = 1
  expand = 3
  formula = G4_lO2
  name = G4_lO2
  specific = 4
FEATURE [App::DocumentObjectGroupPython] Ar  label="Ar : 1"  # scripted group (container) (typed FeaturePython)
  n = 1
  ref = Ar
FEATURE [App::DocumentObjectGroupPython] G4_lAr  # scripted group (container) (typed FeaturePython)
  Dunit = g/cm3
  Dvalue = 1.396
  Group = -> [Ar]
  conduct = 2
  density = 1
  expand = 3
  formula = G4_lAr
  name = G4_lAr
  specific = 4
FEATURE [App::DocumentObjectGroupPython] Br  label="Br : 1"  # scripted group (container) (typed FeaturePython)
  n = 1
  ref = Br
FEATURE [App::DocumentObjectGroupPython] G4_lBr  # scripted group (container) (typed FeaturePython)
  Dunit = g/cm3
  Dvalue = 3.1028
  Group = -> [Br]
  conduct = 2
  density = 1
  expand = 3
  formula = G4_lBr
  name = G4_lBr
  specific = 4
FEATURE [App::DocumentObjectGroupPython] Kr  label="Kr : 1"  # scripted group (container) (typed FeaturePython)
  n = 1
  ref = Kr
FEATURE [App::DocumentObjectGroupPython] G4_lKr  # scripted group (container) (typed FeaturePython)
  Dunit = g/cm3
  Dvalue = 2.418
  Group = -> [Kr]
  conduct = 2
  density = 1
  expand = 3
  formula = G4_lKr
  name = G4_lKr
  specific = 4
FEATURE [App::DocumentObjectGroupPython] Xe  label="Xe : 1"  # scripted group (container) (typed FeaturePython)
  n = 1
  ref = Xe
FEATURE [App::DocumentObjectGroupPython] G4_lXe  # scripted group (container) (typed FeaturePython)
  Dunit = g/cm3
  Dvalue = 2.953
  Group = -> [Xe]
  conduct = 2
  density = 1
  expand = 3
  formula = G4_lXe
  name = G4_lXe
  specific = 4
FEATURE [App::DocumentObjectGroupPython] O_element107  label="O_element : 061"  # scripted group (container) (typed FeaturePython)
  n = 4
  ref = O_element
FEATURE [App::DocumentObjectGroupPython] Pb_element004  label="Pb_element : 002"  # scripted group (container) (typed FeaturePython)
  n = 1
  ref = Pb_element
FEATURE [App::DocumentObjectGroupPython] W_element005  label="W_element : 005"  # scripted group (container) (typed FeaturePython)
  n = 1
  ref = W_element
FEATURE [App::DocumentObjectGroupPython] G4_PbWO4  # scripted group (container) (typed FeaturePython)
  Dunit = g/cm3
  Dvalue = 8.28
  Group = -> [O_element107,Pb_element004,W_element005]
  conduct = 2
  density = 1
  expand = 3
  formula = G4_PbWO4
  name = G4_PbWO4
  specific = 4
FEATURE [App::DocumentObjectGroupPython] alactic  label="alactic : 1"  # scripted group (container) (typed FeaturePython)
  n = 1
  ref = alactic
FEATURE [App::DocumentObjectGroupPython] G4_Galactic  # scripted group (container) (typed FeaturePython)
  Dunit = g/cm3
  Dvalue = 0
  Group = -> [alactic]
  conduct = 2
  density = 1
  expand = 3
  formula = G4_Galactic
  name = G4_Galactic
  specific = 4
FEATURE [App::DocumentObjectGroupPython] RAPHITE_POROUS  label="RAPHITE_POROUS : 1"  # scripted group (container) (typed FeaturePython)
  n = 1
  ref = RAPHITE_POROUS
FEATURE [App::DocumentObjectGroupPython] G4_GRAPHITE_POROUS  # scripted group (container) (typed FeaturePython)
  Dunit = g/cm3
  Dvalue = 1.7
  Group = -> [RAPHITE_POROUS]
  conduct = 2
  density = 1
  expand = 3
  formula = G4_GRAPHITE_POROUS
  name = G4_GRAPHITE_POROUS
  specific = 4
FEATURE [App::DocumentObjectGroupPython] H_element115  label="H_element : 0.150"  # scripted group (container) (typed FeaturePython)
  n = 0.080538
FEATURE [App::DocumentObjectGroupPython] C_element125  label="C_element : 0.600"  # scripted group (container) (typed FeaturePython)
  n = 0.599848
FEATURE [App::DocumentObjectGroupPython] O_element108  label="O_element : 0.320"  # scripted group (container) (typed FeaturePython)
  n = 0.319614
FEATURE [App::DocumentObjectGroupPython] G4_LUCITE  # scripted group (container) (typed FeaturePython)
  Dunit = g/cm3
  Dvalue = 1.19
  Group = -> [H_element115,C_element125,O_element108]
  conduct = 2
  density = 1
  expand = 3
  formula = G4_LUCITE
  name = G4_LUCITE
  specific = 4
FEATURE [App::DocumentObjectGroupPython] Cu_element002  label="Cu_element : 62"  # scripted group (container) (typed FeaturePython)
  n = 62
  ref = Cu_element
FEATURE [App::DocumentObjectGroupPython] Zn_element002  label="Zn_element : 35"  # scripted group (container) (typed FeaturePython)
  n = 35
  ref = Zn_element
FEATURE [App::DocumentObjectGroupPython] Pb_element005  label="Pb_element : 3"  # scripted group (container) (typed FeaturePython)
  n = 3
  ref = Pb_element
FEATURE [App::DocumentObjectGroupPython] G4_BRASS  # scripted group (container) (typed FeaturePython)
  Dunit = g/cm3
  Dvalue = 8.52
  Group = -> [Cu_element002,Zn_element002,Pb_element005]
  conduct = 2
  density = 1
  expand = 3
  formula = G4_BRASS
  name = G4_BRASS
  specific = 4
FEATURE [App::DocumentObjectGroupPython] Cu_element003  label="Cu_element : 89"  # scripted group (container) (typed FeaturePython)
  n = 89
  ref = Cu_element
FEATURE [App::DocumentObjectGroupPython] Zn_element003  label="Zn_element : 9"  # scripted group (container) (typed FeaturePython)
  n = 9
  ref = Zn_element
FEATURE [App::DocumentObjectGroupPython] Pb_element006  label="Pb_element : 2"  # scripted group (container) (typed FeaturePython)
  n = 2
  ref = Pb_element
FEATURE [App::DocumentObjectGroupPython] G4_BRONZE  # scripted group (container) (typed FeaturePython)
  Dunit = g/cm3
  Dvalue = 8.82
  Group = -> [Cu_element003,Zn_element003,Pb_element006]
  conduct = 2
  density = 1
  expand = 3
  formula = G4_BRONZE
  name = G4_BRONZE
  specific = 4
FEATURE [App::DocumentObjectGroupPython] Fe_element008  label="Fe_element : 74"  # scripted group (container) (typed FeaturePython)
  n = 74
  ref = Fe_element
FEATURE [App::DocumentObjectGroupPython] Cr_element002  label="Cr_element : 18"  # scripted group (container) (typed FeaturePython)
  n = 18
  ref = Cr_element
FEATURE [App::DocumentObjectGroupPython] Ni_element002  label="Ni_element : 8"  # scripted group (container) (typed FeaturePython)
  n = 8
  ref = Ni_element
FEATURE [App::DocumentObjectGroupPython] G4_STAINLESS_STEEL  label="G4_STAINLESS-STEEL"  # scripted group (container) (typed FeaturePython)
  Dunit = g/cm3
  Dvalue = 8
  Group = -> [Fe_element008,Cr_element002,Ni_element002]
  conduct = 2
  density = 1
  expand = 3
  formula = G4_STAINLESS-STEEL
  name = G4_STAINLESS-STEEL
  specific = 4
FEATURE [App::DocumentObjectGroupPython] H_element116  label="H_element : 064"  # scripted group (container) (typed FeaturePython)
  n = 18
  ref = H_element
FEATURE [App::DocumentObjectGroupPython] C_element126  label="C_element : 071"  # scripted group (container) (typed FeaturePython)
  n = 12
  ref = C_element
FEATURE [App::DocumentObjectGroupPython] O_element109  label="O_element : 062"  # scripted group (container) (typed FeaturePython)
  n = 7
  ref = O_element
FEATURE [App::DocumentObjectGroupPython] G4_CR39  # scripted group (container) (typed FeaturePython)
  Dunit = g/cm3
  Dvalue = 1.32
  Group = -> [H_element116,C_element126,O_element109]
  conduct = 2
  density = 1
  expand = 3
  formula = G4_CR39
  name = G4_CR39
  specific = 4
FEATURE [App::DocumentObjectGroupPython] H_element117  label="H_element : 38"  # scripted group (container) (typed FeaturePython)
  n = 38
  ref = H_element
FEATURE [App::DocumentObjectGroupPython] C_element127  label="C_element : 072"  # scripted group (container) (typed FeaturePython)
  n = 18
  ref = C_element
FEATURE [App::DocumentObjectGroupPython] O_element110  label="O_element : 063"  # scripted group (container) (typed FeaturePython)
  n = 1
  ref = O_element
FEATURE [App::DocumentObjectGroupPython] G4_OCTADECANOL  # scripted group (container) (typed FeaturePython)
  Dunit = g/cm3
  Dvalue = 0.812
  Group = -> [H_element117,C_element127,O_element110]
  conduct = 2
  density = 1
  expand = 3
  formula = G4_OCTADECANOL
  name = G4_OCTADECANOL
  specific = 4
FEATURE [App::DocumentObjectGroupPython] HEP  # scripted group (container) (typed FeaturePython)
  Group = -> [G4_lH2,G4_lN2,G4_lO2,G4_lAr,G4_lBr,G4_lKr,G4_lXe,G4_PbWO4,G4_Galactic,G4_GRAPHITE_POROUS,G4_LUCITE,G4_BRASS,G4_BRONZE,G4_STAINLESS_STEEL,G4_CR39,G4_OCTADECANOL]
FEATURE [App::DocumentObjectGroupPython] C_element128  label="C_element : 073"  # scripted group (container) (typed FeaturePython)
  n = 14
  ref = C_element
FEATURE [App::DocumentObjectGroupPython] H_element118  label="H_element : 065"  # scripted group (container) (typed FeaturePython)
  n = 10
  ref = H_element
FEATURE [App::DocumentObjectGroupPython] O_element111  label="O_element : 064"  # scripted group (container) (typed FeaturePython)
  n = 2
  ref = O_element
FEATURE [App::DocumentObjectGroupPython] N_element050  label="N_element : 023"  # scripted group (container) (typed FeaturePython)
  n = 2
  ref = N_element
FEATURE [App::DocumentObjectGroupPython] G4_KEVLAR  # scripted group (container) (typed FeaturePython)
  Dunit = g/cm3
  Dvalue = 1.44
  Group = -> [C_element128,H_element118,O_element111,N_element050]
  conduct = 2
  density = 1
  expand = 3
  formula = G4_KEVLAR
  name = G4_KEVLAR
  specific = 4
FEATURE [App::DocumentObjectGroupPython] C_element129  label="C_element : 074"  # scripted group (container) (typed FeaturePython)
  n = 10
  ref = C_element
FEATURE [App::DocumentObjectGroupPython] H_element119  label="H_element : 066"  # scripted group (container) (typed FeaturePython)
  n = 8
  ref = H_element
FEATURE [App::DocumentObjectGroupPython] O_element112  label="O_element : 065"  # scripted group (container) (typed FeaturePython)
  n = 4
  ref = O_element
FEATURE [App::DocumentObjectGroupPython] G4_DACRON  # scripted group (container) (typed FeaturePython)
  Dunit = g/cm3
  Dvalue = 1.4
  Group = -> [C_element129,H_element119,O_element112]
  conduct = 2
  density = 1
  expand = 3
  formula = G4_DACRON
  name = G4_DACRON
  specific = 4
FEATURE [App::DocumentObjectGroupPython] C_element130  label="C_element : 075"  # scripted group (container) (typed FeaturePython)
  n = 4
  ref = C_element
FEATURE [App::DocumentObjectGroupPython] H_element120  label="H_element : 067"  # scripted group (container) (typed FeaturePython)
  n = 5
  ref = H_element
FEATURE [App::DocumentObjectGroupPython] Cl_element030  label="Cl_element : 016"  # scripted group (container) (typed FeaturePython)
  n = 1
  ref = Cl_element
FEATURE [App::DocumentObjectGroupPython] G4_NEOPRENE  # scripted group (container) (typed FeaturePython)
  Dunit = g/cm3
  Dvalue = 1.23
  Group = -> [C_element130,H_element120,Cl_element030]
  conduct = 2
  density = 1
  expand = 3
  formula = G4_NEOPRENE
  name = G4_NEOPRENE
  specific = 4
FEATURE [App::DocumentObjectGroupPython] Space  # scripted group (container) (typed FeaturePython)
  Group = -> [G4_KEVLAR,G4_DACRON,G4_NEOPRENE]
FEATURE [App::DocumentObjectGroupPython] H_element121  label="H_element : 068"  # scripted group (container) (typed FeaturePython)
  n = 5
  ref = H_element
FEATURE [App::DocumentObjectGroupPython] C_element131  label="C_element : 076"  # scripted group (container) (typed FeaturePython)
  n = 4
  ref = C_element
FEATURE [App::DocumentObjectGroupPython] N_element051  label="N_element : 3"  # scripted group (container) (typed FeaturePython)
  n = 3
  ref = N_element
FEATURE [App::DocumentObjectGroupPython] O_element113  label="O_element : 066"  # scripted group (container) (typed FeaturePython)
  n = 1
  ref = O_element
FEATURE [App::DocumentObjectGroupPython] G4_CYTOSINE  # scripted group (container) (typed FeaturePython)
  Dunit = g/cm3
  Dvalue = 1.55
  Group = -> [H_element121,C_element131,N_element051,O_element113]
  conduct = 2
  density = 1
  expand = 3
  formula = G4_CYTOSINE
  name = G4_CYTOSINE
  specific = 4
FEATURE [App::DocumentObjectGroupPython] H_element122  label="H_element : 069"  # scripted group (container) (typed FeaturePython)
  n = 6
  ref = H_element
FEATURE [App::DocumentObjectGroupPython] C_element132  label="C_element : 077"  # scripted group (container) (typed FeaturePython)
  n = 5
  ref = C_element
FEATURE [App::DocumentObjectGroupPython] N_element052  label="N_element : 024"  # scripted group (container) (typed FeaturePython)
  n = 2
  ref = N_element
FEATURE [App::DocumentObjectGroupPython] O_element114  label="O_element : 067"  # scripted group (container) (typed FeaturePython)
  n = 2
  ref = O_element
FEATURE [App::DocumentObjectGroupPython] G4_THYMINE  # scripted group (container) (typed FeaturePython)
  Dunit = g/cm3
  Dvalue = 1.23
  Group = -> [H_element122,C_element132,N_element052,O_element114]
  conduct = 2
  density = 1
  expand = 3
  formula = G4_THYMINE
  name = G4_THYMINE
  specific = 4
FEATURE [App::DocumentObjectGroupPython] H_element123  label="H_element : 070"  # scripted group (container) (typed FeaturePython)
  n = 4
  ref = H_element
FEATURE [App::DocumentObjectGroupPython] C_element133  label="C_element : 078"  # scripted group (container) (typed FeaturePython)
  n = 4
  ref = C_element
FEATURE [App::DocumentObjectGroupPython] N_element053  label="N_element : 025"  # scripted group (container) (typed FeaturePython)
  n = 2
  ref = N_element
FEATURE [App::DocumentObjectGroupPython] O_element115  label="O_element : 068"  # scripted group (container) (typed FeaturePython)
  n = 2
  ref = O_element
FEATURE [App::DocumentObjectGroupPython] G4_URACIL  # scripted group (container) (typed FeaturePython)
  Dunit = g/cm3
  Dvalue = 1.32
  Group = -> [H_element123,C_element133,N_element053,O_element115]
  conduct = 2
  density = 1
  expand = 3
  formula = G4_URACIL
  name = G4_URACIL
  specific = 4
FEATURE [App::DocumentObjectGroupPython] H_element124  label="H_element : 071"  # scripted group (container) (typed FeaturePython)
  n = 4
  ref = H_element
FEATURE [App::DocumentObjectGroupPython] C_element134  label="C_element : 079"  # scripted group (container) (typed FeaturePython)
  n = 5
  ref = C_element
FEATURE [App::DocumentObjectGroupPython] N_element054  label="N_element : 026"  # scripted group (container) (typed FeaturePython)
  n = 5
  ref = N_element
FEATURE [App::DocumentObjectGroupPython] G4_DNA_ADENINE  # scripted group (container) (typed FeaturePython)
  Dunit = g/cm3
  Dvalue = 1
  Group = -> [H_element124,C_element134,N_element054]
  conduct = 2
  density = 1
  expand = 3
  formula = G4_DNA_ADENINE
  name = G4_DNA_ADENINE
  specific = 4
FEATURE [App::DocumentObjectGroupPython] H_element125  label="H_element : 072"  # scripted group (container) (typed FeaturePython)
  n = 4
  ref = H_element
FEATURE [App::DocumentObjectGroupPython] C_element135  label="C_element : 080"  # scripted group (container) (typed FeaturePython)
  n = 5
  ref = C_element
FEATURE [App::DocumentObjectGroupPython] N_element055  label="N_element : 027"  # scripted group (container) (typed FeaturePython)
  n = 5
  ref = N_element
FEATURE [App::DocumentObjectGroupPython] O_element116  label="O_element : 069"  # scripted group (container) (typed FeaturePython)
  n = 1
  ref = O_element
FEATURE [App::DocumentObjectGroupPython] G4_DNA_GUANINE  # scripted group (container) (typed FeaturePython)
  Dunit = g/cm3
  Dvalue = 1
  Group = -> [H_element125,C_element135,N_element055,O_element116]
  conduct = 2
  density = 1
  expand = 3
  formula = G4_DNA_GUANINE
  name = G4_DNA_GUANINE
  specific = 4
FEATURE [App::DocumentObjectGroupPython] H_element126  label="H_element : 073"  # scripted group (container) (typed FeaturePython)
  n = 4
  ref = H_element
FEATURE [App::DocumentObjectGroupPython] C_element136  label="C_element : 081"  # scripted group (container) (typed FeaturePython)
  n = 4
  ref = C_element
FEATURE [App::DocumentObjectGroupPython] N_element056  label="N_element : 028"  # scripted group (container) (typed FeaturePython)
  n = 3
  ref = N_element
FEATURE [App::DocumentObjectGroupPython] O_element117  label="O_element : 070"  # scripted group (container) (typed FeaturePython)
  n = 1
  ref = O_element
FEATURE [App::DocumentObjectGroupPython] G4_DNA_CYTOSINE  # scripted group (container) (typed FeaturePython)
  Dunit = g/cm3
  Dvalue = 1
  Group = -> [H_element126,C_element136,N_element056,O_element117]
  conduct = 2
  density = 1
  expand = 3
  formula = G4_DNA_CYTOSINE
  name = G4_DNA_CYTOSINE
  specific = 4
FEATURE [App::DocumentObjectGroupPython] H_element127  label="H_element : 074"  # scripted group (container) (typed FeaturePython)
  n = 5
  ref = H_element
FEATURE [App::DocumentObjectGroupPython] C_element137  label="C_element : 082"  # scripted group (container) (typed FeaturePython)
  n = 5
  ref = C_element
FEATURE [App::DocumentObjectGroupPython] N_element057  label="N_element : 029"  # scripted group (container) (typed FeaturePython)
  n = 2
  ref = N_element
FEATURE [App::DocumentObjectGroupPython] O_element118  label="O_element : 071"  # scripted group (container) (typed FeaturePython)
  n = 2
  ref = O_element
FEATURE [App::DocumentObjectGroupPython] G4_DNA_THYMINE  # scripted group (container) (typed FeaturePython)
  Dunit = g/cm3
  Dvalue = 1
  Group = -> [H_element127,C_element137,N_element057,O_element118]
  conduct = 2
  density = 1
  expand = 3
  formula = G4_DNA_THYMINE
  name = G4_DNA_THYMINE
  specific = 4
FEATURE [App::DocumentObjectGroupPython] H_element128  label="H_element : 075"  # scripted group (container) (typed FeaturePython)
  n = 3
  ref = H_element
FEATURE [App::DocumentObjectGroupPython] C_element138  label="C_element : 083"  # scripted group (container) (typed FeaturePython)
  n = 4
  ref = C_element
FEATURE [App::DocumentObjectGroupPython] N_element058  label="N_element : 030"  # scripted group (container) (typed FeaturePython)
  n = 2
  ref = N_element
FEATURE [App::DocumentObjectGroupPython] O_element119  label="O_element : 072"  # scripted group (container) (typed FeaturePython)
  n = 2
  ref = O_element
FEATURE [App::DocumentObjectGroupPython] G4_DNA_URACIL  # scripted group (container) (typed FeaturePython)
  Dunit = g/cm3
  Dvalue = 1
  Group = -> [H_element128,C_element138,N_element058,O_element119]
  conduct = 2
  density = 1
  expand = 3
  formula = G4_DNA_URACIL
  name = G4_DNA_URACIL
  specific = 4
FEATURE [App::DocumentObjectGroupPython] H_element129  label="H_element : 076"  # scripted group (container) (typed FeaturePython)
  n = 10
  ref = H_element
FEATURE [App::DocumentObjectGroupPython] C_element139  label="C_element : 084"  # scripted group (container) (typed FeaturePython)
  n = 10
  ref = C_element
FEATURE [App::DocumentObjectGroupPython] N_element059  label="N_element : 031"  # scripted group (container) (typed FeaturePython)
  n = 5
  ref = N_element
FEATURE [App::DocumentObjectGroupPython] O_element120  label="O_element : 073"  # scripted group (container) (typed FeaturePython)
  n = 4
  ref = O_element
FEATURE [App::DocumentObjectGroupPython] G4_DNA_ADENOSINE  # scripted group (container) (typed FeaturePython)
  Dunit = g/cm3
  Dvalue = 1
  Group = -> [H_element129,C_element139,N_element059,O_element120]
  conduct = 2
  density = 1
  expand = 3
  formula = G4_DNA_ADENOSINE
  name = G4_DNA_ADENOSINE
  specific = 4
FEATURE [App::DocumentObjectGroupPython] H_element130  label="H_element : 077"  # scripted group (container) (typed FeaturePython)
  n = 10
  ref = H_element
FEATURE [App::DocumentObjectGroupPython] C_element140  label="C_element : 085"  # scripted group (container) (typed FeaturePython)
  n = 10
  ref = C_element
FEATURE [App::DocumentObjectGroupPython] N_element060  label="N_element : 032"  # scripted group (container) (typed FeaturePython)
  n = 5
  ref = N_element
FEATURE [App::DocumentObjectGroupPython] O_element121  label="O_element : 074"  # scripted group (container) (typed FeaturePython)
  n = 5
  ref = O_element
FEATURE [App::DocumentObjectGroupPython] G4_DNA_GUANOSINE  # scripted group (container) (typed FeaturePython)
  Dunit = g/cm3
  Dvalue = 1
  Group = -> [H_element130,C_element140,N_element060,O_element121]
  conduct = 2
  density = 1
  expand = 3
  formula = G4_DNA_GUANOSINE
  name = G4_DNA_GUANOSINE
  specific = 4
FEATURE [App::DocumentObjectGroupPython] H_element131  label="H_element : 078"  # scripted group (container) (typed FeaturePython)
  n = 10
  ref = H_element
FEATURE [App::DocumentObjectGroupPython] C_element141  label="C_element : 086"  # scripted group (container) (typed FeaturePython)
  n = 9
  ref = C_element
FEATURE [App::DocumentObjectGroupPython] N_element061  label="N_element : 033"  # scripted group (container) (typed FeaturePython)
  n = 3
  ref = N_element
FEATURE [App::DocumentObjectGroupPython] O_element122  label="O_element : 075"  # scripted group (container) (typed FeaturePython)
  n = 5
  ref = O_element
FEATURE [App::DocumentObjectGroupPython] G4_DNA_CYTIDINE  # scripted group (container) (typed FeaturePython)
  Dunit = g/cm3
  Dvalue = 1
  Group = -> [H_element131,C_element141,N_element061,O_element122]
  conduct = 2
  density = 1
  expand = 3
  formula = G4_DNA_CYTIDINE
  name = G4_DNA_CYTIDINE
  specific = 4
FEATURE [App::DocumentObjectGroupPython] H_element132  label="H_element : 079"  # scripted group (container) (typed FeaturePython)
  n = 9
  ref = H_element
FEATURE [App::DocumentObjectGroupPython] C_element142  label="C_element : 087"  # scripted group (container) (typed FeaturePython)
  n = 9
  ref = C_element
FEATURE [App::DocumentObjectGroupPython] N_element062  label="N_element : 034"  # scripted group (container) (typed FeaturePython)
  n = 2
  ref = N_element
FEATURE [App::DocumentObjectGroupPython] O_element123  label="O_element : 076"  # scripted group (container) (typed FeaturePython)
  n = 6
  ref = O_element
FEATURE [App::DocumentObjectGroupPython] G4_DNA_URIDINE  # scripted group (container) (typed FeaturePython)
  Dunit = g/cm3
  Dvalue = 1
  Group = -> [H_element132,C_element142,N_element062,O_element123]
  conduct = 2
  density = 1
  expand = 3
  formula = G4_DNA_URIDINE
  name = G4_DNA_URIDINE
  specific = 4
FEATURE [App::DocumentObjectGroupPython] H_element133  label="H_element : 080"  # scripted group (container) (typed FeaturePython)
  n = 11
  ref = H_element
FEATURE [App::DocumentObjectGroupPython] C_element143  label="C_element : 088"  # scripted group (container) (typed FeaturePython)
  n = 10
  ref = C_element
FEATURE [App::DocumentObjectGroupPython] N_element063  label="N_element : 035"  # scripted group (container) (typed FeaturePython)
  n = 2
  ref = N_element
FEATURE [App::DocumentObjectGroupPython] O_element124  label="O_element : 077"  # scripted group (container) (typed FeaturePython)
  n = 6
  ref = O_element
FEATURE [App::DocumentObjectGroupPython] G4_DNA_METHYLURIDINE  # scripted group (container) (typed FeaturePython)
  Dunit = g/cm3
  Dvalue = 1
  Group = -> [H_element133,C_element143,N_element063,O_element124]
  conduct = 2
  density = 1
  expand = 3
  formula = G4_DNA_METHYLURIDINE
  name = G4_DNA_METHYLURIDINE
  specific = 4
FEATURE [App::DocumentObjectGroupPython] P_element014  label="P_element : 003"  # scripted group (container) (typed FeaturePython)
  n = 1
  ref = P_element
FEATURE [App::DocumentObjectGroupPython] O_element125  label="O_element : 078"  # scripted group (container) (typed FeaturePython)
  n = 3
  ref = O_element
FEATURE [App::DocumentObjectGroupPython] G4_DNA_MONOPHOSPHATE  # scripted group (container) (typed FeaturePython)
  Dunit = g/cm3
  Dvalue = 1
  Group = -> [P_element014,O_element125]
  conduct = 2
  density = 1
  expand = 3
  formula = G4_DNA_MONOPHOSPHATE
  name = G4_DNA_MONOPHOSPHATE
  specific = 4
FEATURE [App::DocumentObjectGroupPython] H_element134  label="H_element : 081"  # scripted group (container) (typed FeaturePython)
  n = 10
  ref = H_element
FEATURE [App::DocumentObjectGroupPython] C_element144  label="C_element : 089"  # scripted group (container) (typed FeaturePython)
  n = 10
  ref = C_element
FEATURE [App::DocumentObjectGroupPython] N_element064  label="N_element : 036"  # scripted group (container) (typed FeaturePython)
  n = 5
  ref = N_element
FEATURE [App::DocumentObjectGroupPython] O_element126  label="O_element : 079"  # scripted group (container) (typed FeaturePython)
  n = 7
  ref = O_element
FEATURE [App::DocumentObjectGroupPython] P_element015  label="P_element : 004"  # scripted group (container) (typed FeaturePython)
  n = 1
  ref = P_element
FEATURE [App::DocumentObjectGroupPython] G4_DNA_A  # scripted group (container) (typed FeaturePython)
  Dunit = g/cm3
  Dvalue = 1
  Group = -> [H_element134,C_element144,N_element064,O_element126,P_element015]
  conduct = 2
  density = 1
  expand = 3
  formula = G4_DNA_A
  name = G4_DNA_A
  specific = 4
FEATURE [App::DocumentObjectGroupPython] H_element135  label="H_element : 082"  # scripted group (container) (typed FeaturePython)
  n = 10
  ref = H_element
FEATURE [App::DocumentObjectGroupPython] C_element145  label="C_element : 090"  # scripted group (container) (typed FeaturePython)
  n = 10
  ref = C_element
FEATURE [App::DocumentObjectGroupPython] N_element065  label="N_element : 037"  # scripted group (container) (typed FeaturePython)
  n = 5
  ref = N_element
FEATURE [App::DocumentObjectGroupPython] O_element127  label="O_element : 8"  # scripted group (container) (typed FeaturePython)
  n = 8
  ref = O_element
FEATURE [App::DocumentObjectGroupPython] P_element016  label="P_element : 005"  # scripted group (container) (typed FeaturePython)
  n = 1
  ref = P_element
FEATURE [App::DocumentObjectGroupPython] G4_DNA_G  # scripted group (container) (typed FeaturePython)
  Dunit = g/cm3
  Dvalue = 1
  Group = -> [H_element135,C_element145,N_element065,O_element127,P_element016]
  conduct = 2
  density = 1
  expand = 3
  formula = G4_DNA_G
  name = G4_DNA_G
  specific = 4
FEATURE [App::DocumentObjectGroupPython] H_element136  label="H_element : 083"  # scripted group (container) (typed FeaturePython)
  n = 10
  ref = H_element
FEATURE [App::DocumentObjectGroupPython] C_element146  label="C_element : 091"  # scripted group (container) (typed FeaturePython)
  n = 9
  ref = C_element
FEATURE [App::DocumentObjectGroupPython] N_element066  label="N_element : 038"  # scripted group (container) (typed FeaturePython)
  n = 3
  ref = N_element
FEATURE [App::DocumentObjectGroupPython] O_element128  label="O_element : 080"  # scripted group (container) (typed FeaturePython)
  n = 8
  ref = O_element
FEATURE [App::DocumentObjectGroupPython] P_element017  label="P_element : 006"  # scripted group (container) (typed FeaturePython)
  n = 1
  ref = P_element
FEATURE [App::DocumentObjectGroupPython] G4_DNA_C  # scripted group (container) (typed FeaturePython)
  Dunit = g/cm3
  Dvalue = 1
  Group = -> [H_element136,C_element146,N_element066,O_element128,P_element017]
  conduct = 2
  density = 1
  expand = 3
  formula = G4_DNA_C
  name = G4_DNA_C
  specific = 4
FEATURE [App::DocumentObjectGroupPython] H_element137  label="H_element : 084"  # scripted group (container) (typed FeaturePython)
  n = 9
  ref = H_element
FEATURE [App::DocumentObjectGroupPython] C_element147  label="C_element : 092"  # scripted group (container) (typed FeaturePython)
  n = 9
  ref = C_element
FEATURE [App::DocumentObjectGroupPython] N_element067  label="N_element : 039"  # scripted group (container) (typed FeaturePython)
  n = 2
  ref = N_element
FEATURE [App::DocumentObjectGroupPython] O_element129  label="O_element : 9"  # scripted group (container) (typed FeaturePython)
  n = 9
  ref = O_element
FEATURE [App::DocumentObjectGroupPython] P_element018  label="P_element : 007"  # scripted group (container) (typed FeaturePython)
  n = 1
  ref = P_element
FEATURE [App::DocumentObjectGroupPython] G4_DNA_U  # scripted group (container) (typed FeaturePython)
  Dunit = g/cm3
  Dvalue = 1
  Group = -> [H_element137,C_element147,N_element067,O_element129,P_element018]
  conduct = 2
  density = 1
  expand = 3
  formula = G4_DNA_U
  name = G4_DNA_U
  specific = 4
FEATURE [App::DocumentObjectGroupPython] H_element138  label="H_element : 085"  # scripted group (container) (typed FeaturePython)
  n = 11
  ref = H_element
FEATURE [App::DocumentObjectGroupPython] C_element148  label="C_element : 093"  # scripted group (container) (typed FeaturePython)
  n = 10
  ref = C_element
FEATURE [App::DocumentObjectGroupPython] N_element068  label="N_element : 040"  # scripted group (container) (typed FeaturePython)
  n = 2
  ref = N_element
FEATURE [App::DocumentObjectGroupPython] O_element130  label="O_element : 081"  # scripted group (container) (typed FeaturePython)
  n = 9
  ref = O_element
FEATURE [App::DocumentObjectGroupPython] P_element019  label="P_element : 008"  # scripted group (container) (typed FeaturePython)
  n = 1
  ref = P_element
FEATURE [App::DocumentObjectGroupPython] G4_DNA_MU  # scripted group (container) (typed FeaturePython)
  Dunit = g/cm3
  Dvalue = 1
  Group = -> [H_element138,C_element148,N_element068,O_element130,P_element019]
  conduct = 2
  density = 1
  expand = 3
  formula = G4_DNA_MU
  name = G4_DNA_MU
  specific = 4
FEATURE [App::DocumentObjectGroupPython] BioChemical  # scripted group (container) (typed FeaturePython)
  Group = -> [G4_CYTOSINE,G4_THYMINE,G4_URACIL,G4_DNA_ADENINE,G4_DNA_GUANINE,G4_DNA_CYTOSINE,G4_DNA_THYMINE,G4_DNA_URACIL,G4_DNA_ADENOSINE,G4_DNA_GUANOSINE,G4_DNA_CYTIDINE,G4_DNA_URIDINE,G4_DNA_METHYLURIDINE,G4_DNA_MONOPHOSPHATE,G4_DNA_A,G4_DNA_G,G4_DNA_C,G4_DNA_U,G4_DNA_MU]
FEATURE [App::DocumentObjectGroupPython] G4Materials  # scripted group (container) (typed FeaturePython)
  Group = -> [NIST,Element,HEP,Space,BioChemical]
  version = 1
FEATURE [App::DocumentObjectGroupPython] Geant4  # scripted group (container) (typed FeaturePython)
  Group = -> [G4Isotopes,G4Elements,G4Materials]
FEATURE [Part::FeaturePython] GDMLBox_WorldBox  # WARN: FeaturePython — macro-defined, semantics opaque (R4)
  lunit = 2
  material = 8
  x = 114.01
  y = 147.706
  z = 147.706
FEATURE [App::DocumentObjectGroupPython] G4_Pyrex_Glass001  label="G4_Pyrex_Glass : 1.000"  # scripted group (container) (typed FeaturePython)
  n = 1
FEATURE [App::DocumentObjectGroupPython] Glass  # scripted group (container) (typed FeaturePython)
  Dunit = g/cm3
  Dvalue = 1.032
  Group = -> [G4_Pyrex_Glass001]
  RINDEX = RINDEXLAR
  conduct = 2
  density = 1
  expand = 3
  name = Glass
  specific = 4
FEATURE [App::DocumentObjectGroupPython] G4_CESIUM_IODIDE  label="G4_CESIUM_IODIDE : 1.000"  # scripted group (container) (typed FeaturePython)
  n = 1
FEATURE [App::DocumentObjectGroupPython] LYSO  # scripted group (container) (typed FeaturePython)
  ABSLENGTH = ABSLENGTHLAR
  Dunit = g/cm3
  Dvalue = 7.1
  FASTCOMPONENT = SCINTLAR
  FASTTIMECONSTANT = FTC
  Group = -> [G4_CESIUM_IODIDE]
  RAYLEIGH = RAYLEIGHLAR
  REEMISSIONPROB = SCINTLAR
  RESOLUTIONSCALE = RS
  RINDEX = RINDEXLAR
  SCINTILLATIONYIELD = SY
  SLOWCOMPONENT = SCINTLAR
  SLOWTIMECONSTANT = STC
  YIELDRATIO = YR
  conduct = 2
  density = 1
  expand = 3
  name = LYSO
  specific = 4
FEATURE [App::DocumentObjectGroupPython] Materials  # scripted group (container) (typed FeaturePython)
  Group = -> [Air,Geant4,Glass,LYSO]
FEATURE [Part::FeaturePython] GDMLSphere_Sphere  # WARN: FeaturePython — macro-defined, semantics opaque (R4)
  aunit = 1
  deltaphi = 360
  deltatheta = 180
  lunit = 2
  material = 164
  rmax = 5
  rmin = 0
  startphi = 0
  starttheta = 0
FEATURE [App::Part] LV_Sphere
  Group = -> [GDMLSphere_Sphere]
  Origin = -> Origin004
FEATURE [App::FeaturePython] ScintWrap1  # WARN: FeaturePython — macro-defined, semantics opaque (R4)
  PV1 = Part001
  PV2 = LV_Sphere
  Surface = ScintWrap
FEATURE [Part::FeaturePython] GDMLBox_Box004  # WARN: FeaturePython — macro-defined, semantics opaque (R4)
  CopyNumber = 1
  Placement = pos=(0,0,37.85) rot=(0,0,1;0rad)
  lunit = 2
  material = 1
  x = 27.8
  y = 27.8
  z = 8
FEATURE [App::Link] Link_GDMLBox_Box004
  CopyNumber = 2
  LinkPlacement = pos=(26.764,0,26.764) rot=(0,1,0;0.785398rad)
  LinkedObject = -> GDMLBox_Box004
  Placement = pos=(26.764,0,26.764) rot=(0,1,0;0.785398rad)
FEATURE [App::Link] Link_GDMLBox_Box004001
  CopyNumber = 3
  LinkPlacement = pos=(37.85,0,7.1e-15) rot=(0,1,0;1.5708rad)
  LinkedObject = -> GDMLBox_Box004
  Placement = pos=(37.85,0,7.1e-15) rot=(0,1,0;1.5708rad)
FEATURE [App::Link] Link_GDMLBox_Box004002
  CopyNumber = 4
  LinkPlacement = pos=(26.764,0,-26.764) rot=(0,1,0;2.35619rad)
  LinkedObject = -> GDMLBox_Box004
  Placement = pos=(26.764,0,-26.764) rot=(0,1,0;2.35619rad)
FEATURE [App::Link] Link_GDMLBox_Box004003
  CopyNumber = 5
  LinkPlacement = pos=(4.6e-15,0,-37.85) rot=(0,1,0;3.14159rad)
  LinkedObject = -> GDMLBox_Box004
  Placement = pos=(4.6e-15,0,-37.85) rot=(0,1,0;3.14159rad)
FEATURE [App::Link] Link_GDMLBox_Box004004
  CopyNumber = 6
  LinkPlacement = pos=(-26.764,0,-26.764) rot=(0,1,0;3.92699rad)
  LinkedObject = -> GDMLBox_Box004
  Placement = pos=(-26.764,0,-26.764) rot=(0,1,0;3.92699rad)
FEATURE [App::Link] Link_GDMLBox_Box004005
  CopyNumber = 7
  LinkPlacement = pos=(-37.85,0,-7.1e-15) rot=(0,1,0;4.71239rad)
  LinkedObject = -> GDMLBox_Box004
  Placement = pos=(-37.85,0,-7.1e-15) rot=(0,1,0;4.71239rad)
FEATURE [App::Link] Link_GDMLBox_Box004006
  CopyNumber = 8
  LinkPlacement = pos=(-26.764,0,26.764) rot=(0,1,0;5.49779rad)
  LinkedObject = -> GDMLBox_Box004
  Placement = pos=(-26.764,0,26.764) rot=(0,1,0;5.49779rad)
FEATURE [App::Part] Array002001
  Group = -> [GDMLBox_Box004,Link_GDMLBox_Box004,Link_GDMLBox_Box004001,Link_GDMLBox_Box004002,Link_GDMLBox_Box004003,Link_GDMLBox_Box004004,Link_GDMLBox_Box004005,Link_GDMLBox_Box004006]
  Origin = -> Origin005
FEATURE [App::Part] Part001
  Group = -> [Array002001]
  Origin = -> Origin002
  SkinSurface = 0
FEATURE [App::Link] Link_Child_Array
  CopyNumber = 10
  LinkPlacement = pos=(26.764,0,26.764) rot=(0,1,0;0.785398rad)
  LinkedObject = -> Child_Array
  Placement = pos=(26.764,0,26.764) rot=(0,1,0;0.785398rad)
FEATURE [App::Link] Link_Child_Array001
  CopyNumber = 11
  LinkPlacement = pos=(37.85,0,7.1e-15) rot=(0,1,0;1.5708rad)
  LinkedObject = -> Child_Array
  Placement = pos=(37.85,0,7.1e-15) rot=(0,1,0;1.5708rad)
FEATURE [App::Link] Link_Child_Array002
  CopyNumber = 12
  LinkPlacement = pos=(26.764,0,-26.764) rot=(0,1,0;2.35619rad)
  LinkedObject = -> Child_Array
  Placement = pos=(26.764,0,-26.764) rot=(0,1,0;2.35619rad)
FEATURE [App::Link] Link_Child_Array003
  CopyNumber = 13
  LinkPlacement = pos=(4.6e-15,0,-37.85) rot=(0,1,0;3.14159rad)
  LinkedObject = -> Child_Array
  Placement = pos=(4.6e-15,0,-37.85) rot=(0,1,0;3.14159rad)
FEATURE [App::Link] Link_Child_Array004
  CopyNumber = 14
  LinkPlacement = pos=(-26.764,0,-26.764) rot=(0,1,0;3.92699rad)
  LinkedObject = -> Child_Array
  Placement = pos=(-26.764,0,-26.764) rot=(0,1,0;3.92699rad)
FEATURE [App::Link] Link_Child_Array005
  CopyNumber = 15
  LinkPlacement = pos=(-37.85,0,-7.1e-15) rot=(0,1,0;4.71239rad)
  LinkedObject = -> Child_Array
  Placement = pos=(-37.85,0,-7.1e-15) rot=(0,1,0;4.71239rad)
FEATURE [App::Link] Link_Child_Array006
  CopyNumber = 16
  LinkPlacement = pos=(-26.764,0,26.764) rot=(0,1,0;5.49779rad)
  LinkedObject = -> Child_Array
  Placement = pos=(-26.764,0,26.764) rot=(0,1,0;5.49779rad)
FEATURE [Part::FeaturePython] GDMLBox_Box005  # WARN: FeaturePython — macro-defined, semantics opaque (R4)
  CopyNumber = 17
  Placement = pos=(-11.99,-11.99,5) rot=(0,0,1;0rad)
  lunit = 2
  material = 0
  x = 3.22
  y = 3.22
  z = 2
FEATURE [App::Link] Link_GDMLBox_Box005
  CopyNumber = 18
  LinkPlacement = pos=(-11.99,-8.59,5) rot=(0,0,1;0rad)
  LinkedObject = -> GDMLBox_Box005
  Placement = pos=(-11.99,-8.59,5) rot=(0,0,1;0rad)
FEATURE [App::Link] Link_GDMLBox_Box005001
  CopyNumber = 19
  LinkPlacement = pos=(-11.99,-5.19,5) rot=(0,0,1;0rad)
  LinkedObject = -> GDMLBox_Box005
  Placement = pos=(-11.99,-5.19,5) rot=(0,0,1;0rad)
FEATURE [App::Link] Link_GDMLBox_Box005002
  CopyNumber = 20
  LinkPlacement = pos=(-11.99,-1.79,5) rot=(0,0,1;0rad)
  LinkedObject = -> GDMLBox_Box005
  Placement = pos=(-11.99,-1.79,5) rot=(0,0,1;0rad)
FEATURE [App::Link] Link_GDMLBox_Box005003
  CopyNumber = 21
  LinkPlacement = pos=(-11.99,1.61,5) rot=(0,0,1;0rad)
  LinkedObject = -> GDMLBox_Box005
  Placement = pos=(-11.99,1.61,5) rot=(0,0,1;0rad)
FEATURE [App::Link] Link_GDMLBox_Box005004
  CopyNumber = 22
  LinkPlacement = pos=(-11.99,5.01,5) rot=(0,0,1;0rad)
  LinkedObject = -> GDMLBox_Box005
  Placement = pos=(-11.99,5.01,5) rot=(0,0,1;0rad)
FEATURE [App::Link] Link_GDMLBox_Box005005
  CopyNumber = 23
  LinkPlacement = pos=(-11.99,8.41,5) rot=(0,0,1;0rad)
  LinkedObject = -> GDMLBox_Box005
  Placement = pos=(-11.99,8.41,5) rot=(0,0,1;0rad)
FEATURE [App::Link] Link_GDMLBox_Box005006
  CopyNumber = 24
  LinkPlacement = pos=(-11.99,11.81,5) rot=(0,0,1;0rad)
  LinkedObject = -> GDMLBox_Box005
  Placement = pos=(-11.99,11.81,5) rot=(0,0,1;0rad)
FEATURE [App::Link] Link_GDMLBox_Box005007
  CopyNumber = 25
  LinkPlacement = pos=(-8.59,-11.99,5) rot=(0,0,1;0rad)
  LinkedObject = -> GDMLBox_Box005
  Placement = pos=(-8.59,-11.99,5) rot=(0,0,1;0rad)
FEATURE [App::Link] Link_GDMLBox_Box005008
  CopyNumber = 26
  LinkPlacement = pos=(-8.59,-8.59,5) rot=(0,0,1;0rad)
  LinkedObject = -> GDMLBox_Box005
  Placement = pos=(-8.59,-8.59,5) rot=(0,0,1;0rad)
FEATURE [App::Link] Link_GDMLBox_Box005009
  CopyNumber = 27
  LinkPlacement = pos=(-8.59,-5.19,5) rot=(0,0,1;0rad)
  LinkedObject = -> GDMLBox_Box005
  Placement = pos=(-8.59,-5.19,5) rot=(0,0,1;0rad)
FEATURE [App::Link] Link_GDMLBox_Box005010
  CopyNumber = 28
  LinkPlacement = pos=(-8.59,-1.79,5) rot=(0,0,1;0rad)
  LinkedObject = -> GDMLBox_Box005
  Placement = pos=(-8.59,-1.79,5) rot=(0,0,1;0rad)
FEATURE [App::Link] Link_GDMLBox_Box005011
  CopyNumber = 29
  LinkPlacement = pos=(-8.59,1.61,5) rot=(0,0,1;0rad)
  LinkedObject = -> GDMLBox_Box005
  Placement = pos=(-8.59,1.61,5) rot=(0,0,1;0rad)
FEATURE [App::Link] Link_GDMLBox_Box005012
  CopyNumber = 30
  LinkPlacement = pos=(-8.59,5.01,5) rot=(0,0,1;0rad)
  LinkedObject = -> GDMLBox_Box005
  Placement = pos=(-8.59,5.01,5) rot=(0,0,1;0rad)
FEATURE [App::Link] Link_GDMLBox_Box005013
  CopyNumber = 31
  LinkPlacement = pos=(-8.59,8.41,5) rot=(0,0,1;0rad)
  LinkedObject = -> GDMLBox_Box005
  Placement = pos=(-8.59,8.41,5) rot=(0,0,1;0rad)
FEATURE [App::Link] Link_GDMLBox_Box005014
  CopyNumber = 32
  LinkPlacement = pos=(-8.59,11.81,5) rot=(0,0,1;0rad)
  LinkedObject = -> GDMLBox_Box005
  Placement = pos=(-8.59,11.81,5) rot=(0,0,1;0rad)
FEATURE [App::Link] Link_GDMLBox_Box005015
  CopyNumber = 33
  LinkPlacement = pos=(-5.19,-11.99,5) rot=(0,0,1;0rad)
  LinkedObject = -> GDMLBox_Box005
  Placement = pos=(-5.19,-11.99,5) rot=(0,0,1;0rad)
FEATURE [App::Link] Link_GDMLBox_Box005016
  CopyNumber = 34
  LinkPlacement = pos=(-5.19,-8.59,5) rot=(0,0,1;0rad)
  LinkedObject = -> GDMLBox_Box005
  Placement = pos=(-5.19,-8.59,5) rot=(0,0,1;0rad)
FEATURE [App::Link] Link_GDMLBox_Box005017
  CopyNumber = 35
  LinkPlacement = pos=(-5.19,-5.19,5) rot=(0,0,1;0rad)
  LinkedObject = -> GDMLBox_Box005
  Placement = pos=(-5.19,-5.19,5) rot=(0,0,1;0rad)
FEATURE [App::Link] Link_GDMLBox_Box005018
  CopyNumber = 36
  LinkPlacement = pos=(-5.19,-1.79,5) rot=(0,0,1;0rad)
  LinkedObject = -> GDMLBox_Box005
  Placement = pos=(-5.19,-1.79,5) rot=(0,0,1;0rad)
FEATURE [App::Link] Link_GDMLBox_Box005019
  CopyNumber = 37
  LinkPlacement = pos=(-5.19,1.61,5) rot=(0,0,1;0rad)
  LinkedObject = -> GDMLBox_Box005
  Placement = pos=(-5.19,1.61,5) rot=(0,0,1;0rad)
FEATURE [App::Link] Link_GDMLBox_Box005020
  CopyNumber = 38
  LinkPlacement = pos=(-5.19,5.01,5) rot=(0,0,1;0rad)
  LinkedObject = -> GDMLBox_Box005
  Placement = pos=(-5.19,5.01,5) rot=(0,0,1;0rad)
FEATURE [App::Link] Link_GDMLBox_Box005021
  CopyNumber = 39
  LinkPlacement = pos=(-5.19,8.41,5) rot=(0,0,1;0rad)
  LinkedObject = -> GDMLBox_Box005
  Placement = pos=(-5.19,8.41,5) rot=(0,0,1;0rad)
FEATURE [App::Link] Link_GDMLBox_Box005022
  CopyNumber = 40
  LinkPlacement = pos=(-5.19,11.81,5) rot=(0,0,1;0rad)
  LinkedObject = -> GDMLBox_Box005
  Placement = pos=(-5.19,11.81,5) rot=(0,0,1;0rad)
FEATURE [App::Link] Link_GDMLBox_Box005023
  CopyNumber = 41
  LinkPlacement = pos=(-1.79,-11.99,5) rot=(0,0,1;0rad)
  LinkedObject = -> GDMLBox_Box005
  Placement = pos=(-1.79,-11.99,5) rot=(0,0,1;0rad)
FEATURE [App::Link] Link_GDMLBox_Box005024
  CopyNumber = 42
  LinkPlacement = pos=(-1.79,-8.59,5) rot=(0,0,1;0rad)
  LinkedObject = -> GDMLBox_Box005
  Placement = pos=(-1.79,-8.59,5) rot=(0,0,1;0rad)
FEATURE [App::Link] Link_GDMLBox_Box005025
  CopyNumber = 43
  LinkPlacement = pos=(-1.79,-5.19,5) rot=(0,0,1;0rad)
  LinkedObject = -> GDMLBox_Box005
  Placement = pos=(-1.79,-5.19,5) rot=(0,0,1;0rad)
FEATURE [App::Link] Link_GDMLBox_Box005026
  CopyNumber = 44
  LinkPlacement = pos=(-1.79,-1.79,5) rot=(0,0,1;0rad)
  LinkedObject = -> GDMLBox_Box005
  Placement = pos=(-1.79,-1.79,5) rot=(0,0,1;0rad)
FEATURE [App::Link] Link_GDMLBox_Box005027
  CopyNumber = 45
  LinkPlacement = pos=(-1.79,1.61,5) rot=(0,0,1;0rad)
  LinkedObject = -> GDMLBox_Box005
  Placement = pos=(-1.79,1.61,5) rot=(0,0,1;0rad)
FEATURE [App::Link] Link_GDMLBox_Box005028
  CopyNumber = 46
  LinkPlacement = pos=(-1.79,5.01,5) rot=(0,0,1;0rad)
  LinkedObject = -> GDMLBox_Box005
  Placement = pos=(-1.79,5.01,5) rot=(0,0,1;0rad)
FEATURE [App::Link] Link_GDMLBox_Box005029
  CopyNumber = 47
  LinkPlacement = pos=(-1.79,8.41,5) rot=(0,0,1;0rad)
  LinkedObject = -> GDMLBox_Box005
  Placement = pos=(-1.79,8.41,5) rot=(0,0,1;0rad)
FEATURE [App::Link] Link_GDMLBox_Box005030
  CopyNumber = 48
  LinkPlacement = pos=(-1.79,11.81,5) rot=(0,0,1;0rad)
  LinkedObject = -> GDMLBox_Box005
  Placement = pos=(-1.79,11.81,5) rot=(0,0,1;0rad)
FEATURE [App::Link] Link_GDMLBox_Box005031
  CopyNumber = 49
  LinkPlacement = pos=(1.61,-11.99,5) rot=(0,0,1;0rad)
  LinkedObject = -> GDMLBox_Box005
  Placement = pos=(1.61,-11.99,5) rot=(0,0,1;0rad)
FEATURE [App::Link] Link_GDMLBox_Box005032
  CopyNumber = 50
  LinkPlacement = pos=(1.61,-8.59,5) rot=(0,0,1;0rad)
  LinkedObject = -> GDMLBox_Box005
  Placement = pos=(1.61,-8.59,5) rot=(0,0,1;0rad)
FEATURE [App::Link] Link_GDMLBox_Box005033
  CopyNumber = 51
  LinkPlacement = pos=(1.61,-5.19,5) rot=(0,0,1;0rad)
  LinkedObject = -> GDMLBox_Box005
  Placement = pos=(1.61,-5.19,5) rot=(0,0,1;0rad)
FEATURE [App::Link] Link_GDMLBox_Box005034
  CopyNumber = 52
  LinkPlacement = pos=(1.61,-1.79,5) rot=(0,0,1;0rad)
  LinkedObject = -> GDMLBox_Box005
  Placement = pos=(1.61,-1.79,5) rot=(0,0,1;0rad)
FEATURE [App::Link] Link_GDMLBox_Box005035
  CopyNumber = 53
  LinkPlacement = pos=(1.61,1.61,5) rot=(0,0,1;0rad)
  LinkedObject = -> GDMLBox_Box005
  Placement = pos=(1.61,1.61,5) rot=(0,0,1;0rad)
FEATURE [App::Link] Link_GDMLBox_Box005036
  CopyNumber = 54
  LinkPlacement = pos=(1.61,5.01,5) rot=(0,0,1;0rad)
  LinkedObject = -> GDMLBox_Box005
  Placement = pos=(1.61,5.01,5) rot=(0,0,1;0rad)
FEATURE [App::Link] Link_GDMLBox_Box005037
  CopyNumber = 55
  LinkPlacement = pos=(1.61,8.41,5) rot=(0,0,1;0rad)
  LinkedObject = -> GDMLBox_Box005
  Placement = pos=(1.61,8.41,5) rot=(0,0,1;0rad)
FEATURE [App::Link] Link_GDMLBox_Box005038
  CopyNumber = 56
  LinkPlacement = pos=(1.61,11.81,5) rot=(0,0,1;0rad)
  LinkedObject = -> GDMLBox_Box005
  Placement = pos=(1.61,11.81,5) rot=(0,0,1;0rad)
FEATURE [App::Link] Link_GDMLBox_Box005039
  CopyNumber = 57
  LinkPlacement = pos=(5.01,-11.99,5) rot=(0,0,1;0rad)
  LinkedObject = -> GDMLBox_Box005
  Placement = pos=(5.01,-11.99,5) rot=(0,0,1;0rad)
FEATURE [App::Link] Link_GDMLBox_Box005040
  CopyNumber = 58
  LinkPlacement = pos=(5.01,-8.59,5) rot=(0,0,1;0rad)
  LinkedObject = -> GDMLBox_Box005
  Placement = pos=(5.01,-8.59,5) rot=(0,0,1;0rad)
FEATURE [App::Link] Link_GDMLBox_Box005041
  CopyNumber = 59
  LinkPlacement = pos=(5.01,-5.19,5) rot=(0,0,1;0rad)
  LinkedObject = -> GDMLBox_Box005
  Placement = pos=(5.01,-5.19,5) rot=(0,0,1;0rad)
FEATURE [App::Link] Link_GDMLBox_Box005042
  CopyNumber = 60
  LinkPlacement = pos=(5.01,-1.79,5) rot=(0,0,1;0rad)
  LinkedObject = -> GDMLBox_Box005
  Placement = pos=(5.01,-1.79,5) rot=(0,0,1;0rad)
FEATURE [App::Link] Link_GDMLBox_Box005043
  CopyNumber = 61
  LinkPlacement = pos=(5.01,1.61,5) rot=(0,0,1;0rad)
  LinkedObject = -> GDMLBox_Box005
  Placement = pos=(5.01,1.61,5) rot=(0,0,1;0rad)
FEATURE [App::Link] Link_GDMLBox_Box005044
  CopyNumber = 62
  LinkPlacement = pos=(5.01,5.01,5) rot=(0,0,1;0rad)
  LinkedObject = -> GDMLBox_Box005
  Placement = pos=(5.01,5.01,5) rot=(0,0,1;0rad)
FEATURE [App::Link] Link_GDMLBox_Box005045
  CopyNumber = 63
  LinkPlacement = pos=(5.01,8.41,5) rot=(0,0,1;0rad)
  LinkedObject = -> GDMLBox_Box005
  Placement = pos=(5.01,8.41,5) rot=(0,0,1;0rad)
FEATURE [App::Link] Link_GDMLBox_Box005046
  CopyNumber = 64
  LinkPlacement = pos=(5.01,11.81,5) rot=(0,0,1;0rad)
  LinkedObject = -> GDMLBox_Box005
  Placement = pos=(5.01,11.81,5) rot=(0,0,1;0rad)
FEATURE [App::Link] Link_GDMLBox_Box005047
  CopyNumber = 65
  LinkPlacement = pos=(8.41,-11.99,5) rot=(0,0,1;0rad)
  LinkedObject = -> GDMLBox_Box005
  Placement = pos=(8.41,-11.99,5) rot=(0,0,1;0rad)
FEATURE [App::Link] Link_GDMLBox_Box005048
  CopyNumber = 66
  LinkPlacement = pos=(8.41,-8.59,5) rot=(0,0,1;0rad)
  LinkedObject = -> GDMLBox_Box005
  Placement = pos=(8.41,-8.59,5) rot=(0,0,1;0rad)
FEATURE [App::Link] Link_GDMLBox_Box005049
  CopyNumber = 67
  LinkPlacement = pos=(8.41,-5.19,5) rot=(0,0,1;0rad)
  LinkedObject = -> GDMLBox_Box005
  Placement = pos=(8.41,-5.19,5) rot=(0,0,1;0rad)
FEATURE [App::Link] Link_GDMLBox_Box005050
  CopyNumber = 68
  LinkPlacement = pos=(8.41,-1.79,5) rot=(0,0,1;0rad)
  LinkedObject = -> GDMLBox_Box005
  Placement = pos=(8.41,-1.79,5) rot=(0,0,1;0rad)
FEATURE [App::Link] Link_GDMLBox_Box005051
  CopyNumber = 69
  LinkPlacement = pos=(8.41,1.61,5) rot=(0,0,1;0rad)
  LinkedObject = -> GDMLBox_Box005
  Placement = pos=(8.41,1.61,5) rot=(0,0,1;0rad)
FEATURE [App::Link] Link_GDMLBox_Box005052
  CopyNumber = 70
  LinkPlacement = pos=(8.41,5.01,5) rot=(0,0,1;0rad)
  LinkedObject = -> GDMLBox_Box005
  Placement = pos=(8.41,5.01,5) rot=(0,0,1;0rad)
FEATURE [App::Link] Link_GDMLBox_Box005053
  CopyNumber = 71
  LinkPlacement = pos=(8.41,8.41,5) rot=(0,0,1;0rad)
  LinkedObject = -> GDMLBox_Box005
  Placement = pos=(8.41,8.41,5) rot=(0,0,1;0rad)
FEATURE [App::Link] Link_GDMLBox_Box005054
  CopyNumber = 72
  LinkPlacement = pos=(8.41,11.81,5) rot=(0,0,1;0rad)
  LinkedObject = -> GDMLBox_Box005
  Placement = pos=(8.41,11.81,5) rot=(0,0,1;0rad)
FEATURE [App::Link] Link_GDMLBox_Box005055
  CopyNumber = 73
  LinkPlacement = pos=(11.81,-11.99,5) rot=(0,0,1;0rad)
  LinkedObject = -> GDMLBox_Box005
  Placement = pos=(11.81,-11.99,5) rot=(0,0,1;0rad)
FEATURE [App::Link] Link_GDMLBox_Box005056
  CopyNumber = 74
  LinkPlacement = pos=(11.81,-8.59,5) rot=(0,0,1;0rad)
  LinkedObject = -> GDMLBox_Box005
  Placement = pos=(11.81,-8.59,5) rot=(0,0,1;0rad)
FEATURE [App::Link] Link_GDMLBox_Box005057
  CopyNumber = 75
  LinkPlacement = pos=(11.81,-5.19,5) rot=(0,0,1;0rad)
  LinkedObject = -> GDMLBox_Box005
  Placement = pos=(11.81,-5.19,5) rot=(0,0,1;0rad)
FEATURE [App::Link] Link_GDMLBox_Box005058
  CopyNumber = 76
  LinkPlacement = pos=(11.81,-1.79,5) rot=(0,0,1;0rad)
  LinkedObject = -> GDMLBox_Box005
  Placement = pos=(11.81,-1.79,5) rot=(0,0,1;0rad)
FEATURE [App::Link] Link_GDMLBox_Box005059
  CopyNumber = 77
  LinkPlacement = pos=(11.81,1.61,5) rot=(0,0,1;0rad)
  LinkedObject = -> GDMLBox_Box005
  Placement = pos=(11.81,1.61,5) rot=(0,0,1;0rad)
FEATURE [App::Link] Link_GDMLBox_Box005060
  CopyNumber = 78
  LinkPlacement = pos=(11.81,5.01,5) rot=(0,0,1;0rad)
  LinkedObject = -> GDMLBox_Box005
  Placement = pos=(11.81,5.01,5) rot=(0,0,1;0rad)
FEATURE [App::Link] Link_GDMLBox_Box005061
  CopyNumber = 79
  LinkPlacement = pos=(11.81,8.41,5) rot=(0,0,1;0rad)
  LinkedObject = -> GDMLBox_Box005
  Placement = pos=(11.81,8.41,5) rot=(0,0,1;0rad)
FEATURE [App::Link] Link_GDMLBox_Box005062
  CopyNumber = 80
  LinkPlacement = pos=(11.81,11.81,5) rot=(0,0,1;0rad)
  LinkedObject = -> GDMLBox_Box005
  Placement = pos=(11.81,11.81,5) rot=(0,0,1;0rad)
FEATURE [App::Part] Child_Array  label="Child_Array001"
  CopyNumber = 9
  Group = -> [GDMLBox_Box005,Link_GDMLBox_Box005,Link_GDMLBox_Box005001,Link_GDMLBox_Box005002,Link_GDMLBox_Box005003,Link_GDMLBox_Box005004,Link_GDMLBox_Box005005,Link_GDMLBox_Box005006,Link_GDMLBox_Box005007,Link_GDMLBox_Box005008,Link_GDMLBox_Box005009,Link_GDMLBox_Box005010,Link_GDMLBox_Box005011,Link_GDMLBox_Box005012,Link_GDMLBox_Box005013,Link_GDMLBox_Box005014,Link_GDMLBox_Box005015,+47 more]
  Origin = -> Origin007
  Placement = pos=(0,0,37.85) rot=(0,0,1;0rad)
FEATURE [App::Part] Parent_Array  label="Parent_Array001"
  Group = -> [Child_Array,Link_Child_Array,Link_Child_Array001,Link_Child_Array002,Link_Child_Array003,Link_Child_Array004,Link_Child_Array005,Link_Child_Array006]
  Origin = -> Origin006
FEATURE [App::Part] Part
  Group = -> [Parent_Array]
  Origin = -> Origin003
FEATURE [App::Part] worldVOL
  Group = -> [GDMLBox_WorldBox,Part001,Part,LV_Sphere]
  Origin = -> Origin
